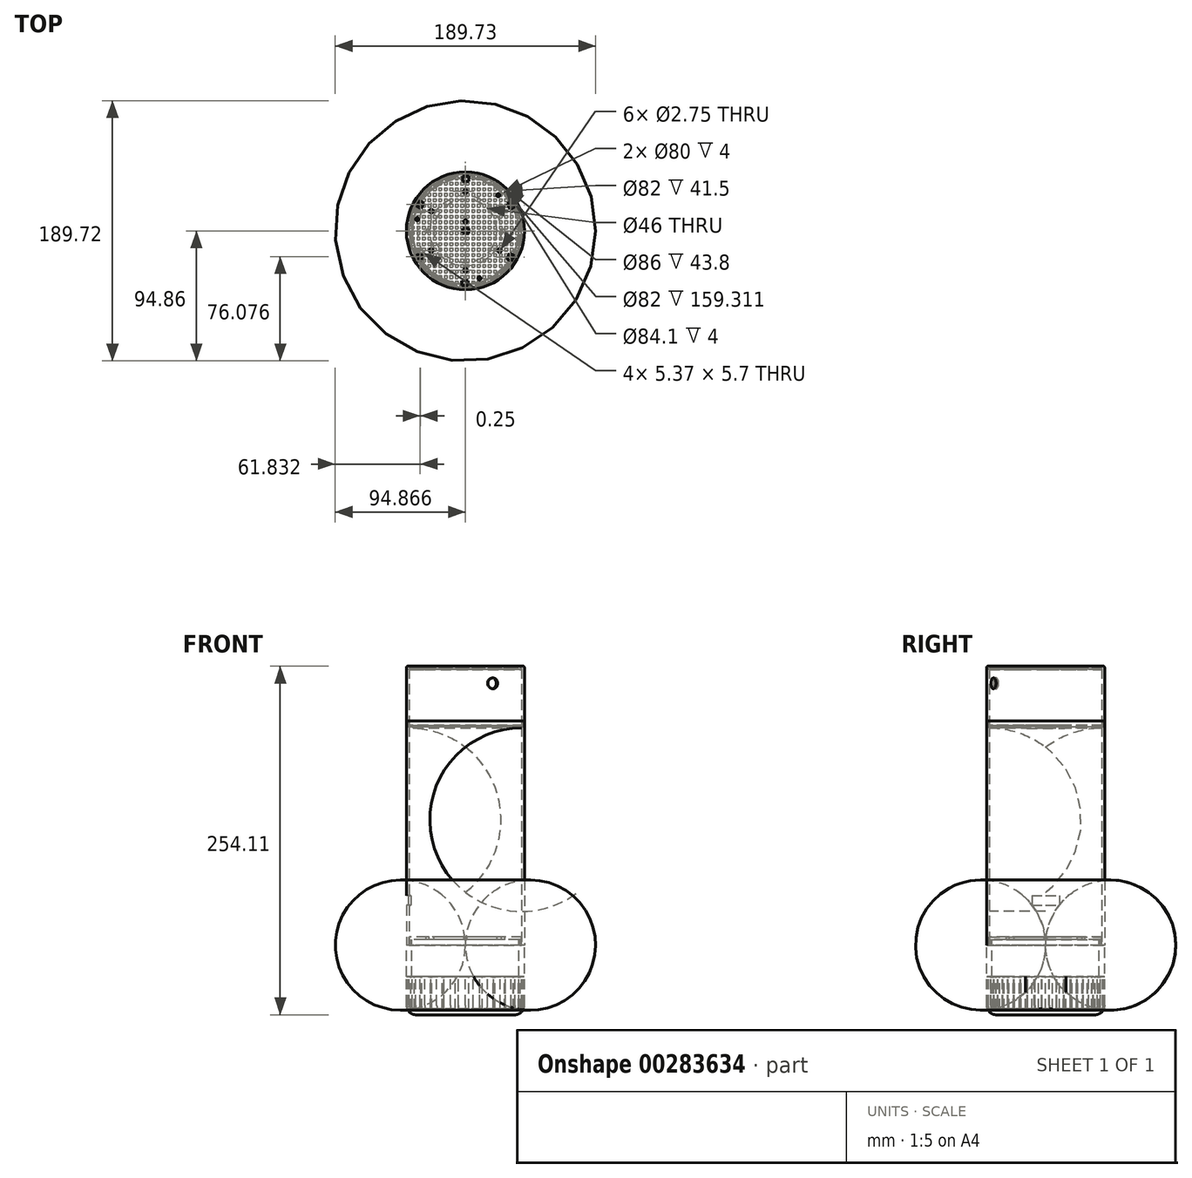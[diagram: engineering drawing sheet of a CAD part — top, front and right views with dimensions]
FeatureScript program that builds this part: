
annotation { "Feature Type Name" : "Feature", "Feature Type Description" : "" }
export const myFeature = defineFeature(function(context is Context, id is Id, definition is map)
    precondition{}
    {
        {
            var Q0;
            Q0=qCreatedBy(makeId("Front.planeOp"),FACE);
            var sketch = newSketch(context, id + "F0", { "sketchPlane" : qUnion([Q0])});
            skLineSegment(sketch, "E0", {"start": v(-50.53, -12.24) * mm, "end": v(-47.53, -12.24) * mm});
            skLineSegment(sketch, "E1", {"start": v(-50.53, 151.07) * mm, "end": v(-50.53, -2.93) * mm});
            skLineSegment(sketch, "E2", {"start": v(-7.53, -12.24) * mm, "end": v(-7.53, -63.04) * mm});
            skLineSegment(sketch, "E3", {"start": v(-50.53, -12.24) * mm, "end": v(-50.53, -56.04) * mm});
            skLineSegment(sketch, "E4", {"start": v(-7.53, -63.04) * mm, "end": v(-37.53, -63.04) * mm});
            skPoint(sketch, "E5.visualSharp", {"position": v(-50.53, -63.04) * mm});
            skArc(sketch, "E5.filletArc", {"start": v(-50.53, -56.04) * mm, "mid": v(-48.48, -61) * mm, "end": v(-43.53, -63.04) * mm});
            skLineSegment(sketch, "E6", {"start": v(-40.53, -63.04) * mm, "end": v(-37.53, -63.04) * mm});
            skLineSegment(sketch, "E7", {"start": v(-7.53, -63.04) * mm, "end": v(-7.53, -61.54) * mm});
            skLineSegment(sketch, "E8", {"start": v(-47.53, -12.24) * mm, "end": v(-47.53, -54.54) * mm});
            skLineSegment(sketch, "E9", {"start": v(-7.53, -61.54) * mm, "end": v(-40.53, -61.54) * mm});
            skPoint(sketch, "E10", {"position": v(-50.53, -34.14) * mm});
            skLineSegment(sketch, "E11", {"start": v(-50.53, -34.14) * mm, "end": v(-50.53, -47.14) * mm, "construction": true});
            skPoint(sketch, "E12", {"position": v(-50.53, -47.14) * mm});
            skLineSegment(sketch, "E13", {"start": v(-7.53, -63.04) * mm, "end": v(-7.53, 112.76) * mm, "construction": true});
            skLineSegment(sketch, "E14", {"start": v(-7.53, -8.24) * mm, "end": v(-7.53, -6.24) * mm});
            skLineSegment(sketch, "E15", {"start": v(-7.53, -59.5) * mm, "end": v(-7.53, -52.5) * mm});
            skLineSegment(sketch, "E16", {"start": v(-43.53, -63.04) * mm, "end": v(-40.53, -63.04) * mm});
            skLineSegment(sketch, "E17", {"start": v(-50.53, 151.07) * mm, "end": v(-49.58, 151.07) * mm});
            skLineSegment(sketch, "E18", {"start": v(-49.58, 151.07) * mm, "end": v(-49.58, 147.07) * mm});
            skLineSegment(sketch, "E19", {"start": v(-49.53, 148.07) * mm, "end": v(-49.53, 151.07) * mm});
            skLineSegment(sketch, "E20", {"start": v(-49.53, 151.07) * mm, "end": v(-50.53, 151.07) * mm});
            skLineSegment(sketch, "E21", {"start": v(-49.53, 148.07) * mm, "end": v(-48.53, 148.07) * mm});
            skLineSegment(sketch, "E22", {"start": v(-48.53, 148.07) * mm, "end": v(-48.53, 151.07) * mm});
            skLineSegment(sketch, "E23", {"start": v(-50.53, 191.07) * mm, "end": v(-7.53, 191.07) * mm});
            skLineSegment(sketch, "E24", {"start": v(-7.53, 191.07) * mm, "end": v(-7.53, 189.57) * mm});
            skPoint(sketch, "E25", {"position": v(-50.53, 181.57) * mm});
            skPoint(sketch, "E26", {"position": v(-47.73, 181.57) * mm});
            skLineSegment(sketch, "E27", {"start": v(-48.53, 151.07) * mm, "end": v(-48.53, 189.57) * mm});
            skLineSegment(sketch, "E28", {"start": v(-7.53, 191.07) * mm, "end": v(-7.53, 112.76) * mm, "construction": true});
            skPoint(sketch, "E29.end.orphan", {"position": v(-50.53, -2.93) * mm});
            skLineSegment(sketch, "E30", {"start": v(-50.53, -2.93) * mm, "end": v(-50.53, -12.24) * mm});
            skLineSegment(sketch, "E31", {"start": v(-48.53, -6.24) * mm, "end": v(-48.53, -12.24) * mm});
            skLineSegment(sketch, "E32", {"start": v(-47.53, -12.24) * mm, "end": v(-46.53, -12.24) * mm});
            skLineSegment(sketch, "E33", {"start": v(-48.53, -12.24) * mm, "end": v(-48.48, -12.24) * mm});
            skLineSegment(sketch, "E34", {"start": v(-48.48, -12.24) * mm, "end": v(-48.48, -6.24) * mm});
            skLineSegment(sketch, "E35", {"start": v(-48.48, -6.24) * mm, "end": v(-47.53, -6.24) * mm});
            skLineSegment(sketch, "E36", {"start": v(-47.53, -6.24) * mm, "end": v(-47.53, -12.24) * mm});
            skLineSegment(sketch, "E37", {"start": v(-7.53, -6.24) * mm, "end": v(-48.48, -6.24) * mm});
            skLineSegment(sketch, "E38", {"start": v(-7.53, -8.24) * mm, "end": v(-47.53, -8.24) * mm});
            skLineSegment(sketch, "E39", {"start": v(-47.53, -12.24) * mm, "end": v(-47.48, -12.24) * mm});
            skLineSegment(sketch, "E40", {"start": v(-47.48, -12.24) * mm, "end": v(-47.48, -8.24) * mm});
            skLineSegment(sketch, "E41", {"start": v(-47.48, -8.24) * mm, "end": v(-46.53, -8.24) * mm});
            skLineSegment(sketch, "E42", {"start": v(-46.53, -8.24) * mm, "end": v(-46.53, -12.24) * mm});
            skLineSegment(sketch, "E43", {"start": v(-46.53, -12.24) * mm, "end": v(-46.53, -58.92) * mm});
            skArc(sketch, "E44", {"start": v(-46.53, -58.92) * mm, "mid": v(-43.86, -60.98) * mm, "end": v(-40.53, -61.54) * mm});
            skArc(sketch, "E45", {"start": v(-46.53, -58.92) * mm, "mid": v(-18.57, -42.66) * mm, "end": v(-7.53, -12.24) * mm});
            skLineSegment(sketch, "E46", {"start": v(-49.58, 147.07) * mm, "end": v(-50.53, 147.07) * mm, "construction": true});
            skLineSegment(sketch, "E47", {"start": v(-49.53, 148.07) * mm, "end": v(-49.53, 147.07) * mm});
            skLineSegment(sketch, "E48", {"start": v(-49.53, 147.07) * mm, "end": v(-7.53, 147.07) * mm});
            skLineSegment(sketch, "E49", {"start": v(-48.53, 148.07) * mm, "end": v(-7.53, 148.07) * mm});
            skLineSegment(sketch, "E50", {"start": v(-7.53, 148.07) * mm, "end": v(-7.53, 147.07) * mm});
            skLineSegment(sketch, "E51", {"start": v(-49.58, 147.07) * mm, "end": v(-48.53, 147.07) * mm});
            skLineSegment(sketch, "E52", {"start": v(-48.53, 147.07) * mm, "end": v(-48.53, -6.24) * mm});
            skLineSegment(sketch, "E53", {"start": v(-48.53, -6.24) * mm, "end": v(-47.53, -6.24) * mm, "construction": true});
            skLineSegment(sketch, "E54", {"start": v(-48.53, 147.07) * mm, "end": v(-48.48, 147.07) * mm});
            skLineSegment(sketch, "E55", {"start": v(-48.48, 147.07) * mm, "end": v(-48.48, 146.07) * mm});
            skLineSegment(sketch, "E56", {"start": v(-7.53, 147.07) * mm, "end": v(-7.53, 132.07) * mm});
            skLineSegment(sketch, "E57", {"start": v(-48.48, 146.07) * mm, "end": v(-7.53, 146.07) * mm, "construction": true});
            skArc(sketch, "E58", {"start": v(-7.53, 132.07) * mm, "mid": v(-26.85, 142.47) * mm, "end": v(-48.48, 146.07) * mm});
            skLineSegment(sketch, "E59", {"start": v(-48.48, -6.24) * mm, "end": v(-48.53, 10.54) * mm, "construction": true});
            skLineSegment(sketch, "E60", {"start": v(-48.48, -6.24) * mm, "end": v(-48.53, 23.76) * mm, "construction": true});
            skPoint(sketch, "E61", {"position": v(-48.53, 23.76) * mm});
            skLineSegment(sketch, "E62", {"start": v(-50.53, 151.07) * mm, "end": v(-50.53, 191.07) * mm});
            skLineSegment(sketch, "E63", {"start": v(-48.53, 148.07) * mm, "end": v(-48.53, 147.07) * mm, "construction": true});
            skLineSegment(sketch, "E64", {"start": v(-48.53, 189.57) * mm, "end": v(-7.53, 189.57) * mm});
            skSolve(sketch);
        }
        {
            var Q0;
            {var subQ1=sQuery(id+"F0.wireOp",EDGE,"E0");Q0=makeQuery(id+"F0.imprint","IMPRINT",FACE,{"disambiguationData":[TD([[makeQuery(id+"F0.imprint","IMPRINT",EDGE,{"derivedFrom":subQ1}),-1.0]])]});}
            var Q1;
            Q1=makeQuery(id+"F0.imprint","IMPRINT",FACE,{"disambiguationData":[TD([[makeQuery(id+"F0.imprint","IMPRINT",EDGE,{"derivedFrom":sQuery(id+"F0.wireOp",EDGE,"E2")}),-1.0]])]});
            var Q2;
            Q2=makeQuery(id+"F0.imprint","IMPRINT",FACE,{"disambiguationData":[TD([[makeQuery(id+"F0.imprint","IMPRINT",EDGE,{"derivedFrom":sQuery(id+"F0.wireOp",EDGE,"E32")}),1.0]])]});
            var Q3;
            Q3=sQuery(id+"F0.wireOp",EDGE,"E2");
            revolve(context, id + "F1", {"entities" : qUnion([Q0, Q1, Q2]), "axis" : qUnion([Q3]), "revolveType" : RevolveType.FULL});
        }
        {
            var Q0;
            Q0=sQuery(id+"F0.wireOp",EDGE,"E3");
            var Q1;
            Q1=sQuery(id+"F0.wireOp",VERTEX,"E12");
            cPlane(context, id + "F2", {"entities" : qUnion([Q0, Q1]), "cplaneType" : CPlaneType.LINE_POINT, "offset" : 0 * mm, "width" : 150 * mm, "height" : 150 * mm});
        }
        {
            var Q0;
            Q0=qCreatedBy(id+"F2.planeOp",FACE);
            var sketch = newSketch(context, id + "F3", { "sketchPlane" : qUnion([Q0])});
            skLineSegment(sketch, "E65", {"start": v(-50.53, 0) * mm, "end": v(-46.03, 0) * mm, "construction": true});
            skLineSegment(sketch, "E66", {"start": v(-46.03, 0) * mm, "end": v(-46.03, 2.5) * mm, "construction": true});
            skLineSegment(sketch, "E67", {"start": v(-46.03, 2.5) * mm, "end": v(-50.53, 2.5) * mm});
            skLineSegment(sketch, "E68", {"start": v(-50.53, 2.5) * mm, "end": v(-50.53, -2.5) * mm});
            skLineSegment(sketch, "E69", {"start": v(-50.53, -2.5) * mm, "end": v(-46.03, -2.5) * mm});
            skLineSegment(sketch, "E70", {"start": v(-46.03, -2.5) * mm, "end": v(-46.03, 2.5) * mm});
            skLineSegment(sketch, "E71", {"start": v(-46.03, -6.5) * mm, "end": v(-46.03, -2.5) * mm});
            skLineSegment(sketch, "E72.MirrorCS", {"start": v(-46.03, 6.5) * mm, "end": v(-46.03, 2.5) * mm});
            skLineSegment(sketch, "E73", {"start": v(-46.03, -2.5) * mm, "end": v(-47.13, -2.5) * mm, "construction": true});
            skLineSegment(sketch, "E74", {"start": v(-47.13, -2.5) * mm, "end": v(-47.13, -5.3) * mm, "construction": true});
            skArc(sketch, "E75", {"start": v(-47.13, -5.3) * mm, "mid": v(-48.33, -3.3) * mm, "end": v(-50.53, -2.5) * mm});
            skArc(sketch, "E76", {"start": v(-47.13, -5.3) * mm, "mid": v(-46.82, -6.11) * mm, "end": v(-46.03, -6.5) * mm});
            skArc(sketch, "E77.MirrorCS", {"start": v(-47.13, 5.3) * mm, "mid": v(-48.33, 3.3) * mm, "end": v(-50.53, 2.5) * mm});
            skArc(sketch, "E78.MirrorCS", {"start": v(-47.13, 5.3) * mm, "mid": v(-46.82, 6.11) * mm, "end": v(-46.03, 6.5) * mm});
            skSolve(sketch);
        }
        {
            var Q0;
            Q0=qSketchRegion(id+"F3",true);
            extrude(context, id + "F4", {"entities" : qUnion([Q0]), "endBound" : BoundingType.SYMMETRIC, "depth" : 23.8 * mm});
        }
        {
            var Q0;
            Q0=makeQuery(id+"F4.opExtrude","SWEPT_BODY",BODY,{"disambiguationData":[OSD([sQuery(id+"F3.wireOp",EDGE,"E67"),sQuery(id+"F3.wireOp",EDGE,"E68"),sQuery(id+"F3.wireOp",EDGE,"E69"),sQuery(id+"F3.wireOp",EDGE,"E70")])]});
            var Q1;
            Q1=sQuery(id+"F0.wireOp",EDGE,"E2");
            circularPattern(context, id + "F5", {"operationType" : NewBodyOperationType.REMOVE, "entities" : qUnion([Q0]), "axis" : qUnion([Q1]), "angle" : 360 * degree, "instanceCount" : 25, "equalSpace" : true});
        }
        {
            var Q0;
            {var subQ4=sQuery(id+"F0.wireOp",EDGE,"E34");Q0=makeQuery(id+"F0.imprint","IMPRINT",FACE,{"disambiguationData":[TD([[makeQuery(id+"F0.imprint","IMPRINT",EDGE,{"derivedFrom":subQ4}),-1.0]])]});}
            var Q1;
            {var subQ1=sQuery(id+"F0.wireOp",EDGE,"E14");Q1=makeQuery(id+"F0.imprint","IMPRINT",FACE,{"disambiguationData":[TD([[makeQuery(id+"F0.imprint","IMPRINT",EDGE,{"derivedFrom":subQ1}),1.0]])]});}
            var Q2;
            Q2=sQuery(id+"F0.wireOp",EDGE,"E2");
            revolve(context, id + "F6", {"entities" : qUnion([Q0, Q1]), "axis" : qUnion([Q2]), "revolveType" : RevolveType.FULL});
        }
        {
            var Q0;
            {var subQ1=sQuery(id+"F0.wireOp",EDGE,"E1");Q0=makeQuery(id+"F0.imprint","IMPRINT",FACE,{"disambiguationData":[TD([[makeQuery(id+"F0.imprint","IMPRINT",EDGE,{"derivedFrom":subQ1}),1.0]])]});}
            var Q1;
            Q1=sQuery(id+"F0.wireOp",EDGE,"E13");
            revolve(context, id + "F7", {"entities" : qUnion([Q0]), "axis" : qUnion([Q1]), "revolveType" : RevolveType.FULL});
        }
        {
            var Q0;
            Q0=makeQuery(id+"F0.imprint","IMPRINT",FACE,{"disambiguationData":[TD([[makeQuery(id+"F0.imprint","IMPRINT",EDGE,{"derivedFrom":sQuery(id+"F0.wireOp",EDGE,"E21")}),-1.0]])]});
            var Q1;
            Q1=makeQuery(id+"F0.imprint","IMPRINT",FACE,{"disambiguationData":[TD([[makeQuery(id+"F0.imprint","IMPRINT",EDGE,{"derivedFrom":sQuery(id+"F0.wireOp",EDGE,"E48")}),-1.0]])]});
            var Q2;
            Q2=sQuery(id+"F0.wireOp",EDGE,"E56");
            revolve(context, id + "F8", {"entities" : qUnion([Q0, Q1]), "axis" : qUnion([Q2]), "revolveType" : RevolveType.FULL});
        }
        {
            var Q0;
            {var subQ5=sQuery(id+"F0.wireOp",EDGE,"E19");Q0=makeQuery(id+"F0.imprint","IMPRINT",FACE,{"disambiguationData":[TD([[makeQuery(id+"F0.imprint","IMPRINT",EDGE,{"derivedFrom":subQ5}),-1.0]])]});}
            var Q1;
            Q1=sQuery(id+"F0.wireOp",EDGE,"E13");
            revolve(context, id + "F9", {"entities" : qUnion([Q0]), "axis" : qUnion([Q1]), "revolveType" : RevolveType.FULL});
        }
        {
            var Q0;
            Q0=makeQuery(id+"F9.opRevolve","SWEPT_EDGE",EDGE,{"disambiguationData":[OSD([sQuery(id+"F0.wireOp",EDGE,"f6rtj6dZ-6JDe-umgd-hrW0-nHuk5Vi6zJmO"),sQuery(id+"F0.wireOp",EDGE,"E23")])]});
            fillet(context, id + "F10", {"entities" : qUnion([Q0]), "radius" : 1 * mm, "tangentPropagation" : true, "allowEdgeOverflow" : false});
        }
        {
            var Q0;
            Q0=makeQuery(id+"F9.opRevolve","SWEPT_FACE",FACE,{"disambiguationData":[OSD([sQuery(id+"F0.wireOp",EDGE,"E23")])]});
            var sketch = newSketch(context, id + "F11", { "sketchPlane" : qUnion([Q0])});
            skPoint(sketch, "E79", {"position": v(-7.53, 0) * mm});
            skCircle(sketch, "E80", {"center": v(-7.53, 0) * mm, "radius": 40 * mm, "construction": true});
            skLineSegment(sketch, "E81", {"start": v(-7.53, 0) * mm, "end": v(-7.53, -40) * mm, "construction": true});
            skLineSegment(sketch, "E82.1.0", {"start": v(-7.53, 0) * mm, "end": v(27.1, -20) * mm, "construction": true});
            skLineSegment(sketch, "E82.2.0", {"start": v(-7.53, 0) * mm, "end": v(27.1, 20) * mm, "construction": true});
            skLineSegment(sketch, "E82.3.0", {"start": v(-7.53, 0) * mm, "end": v(-7.53, 40) * mm, "construction": true});
            skLineSegment(sketch, "E82.4.0", {"start": v(-7.53, 0) * mm, "end": v(-42.18, 20) * mm, "construction": true});
            skLineSegment(sketch, "E82.5.0", {"start": v(-7.53, 0) * mm, "end": v(-42.18, -20) * mm, "construction": true});
            skLineSegment(sketch, "E83", {"start": v(-7.53, -40) * mm, "end": v(-7.53, -38) * mm, "construction": true});
            skPoint(sketch, "E84", {"position": v(-7.53, -38) * mm});
            skLineSegment(sketch, "E85", {"start": v(-7.53, -38) * mm, "end": v(-5.53, -38) * mm, "construction": true});
            skLineSegment(sketch, "E86", {"start": v(-7.53, -38) * mm, "end": v(-10.03, -38) * mm, "construction": true});
            skLineSegment(sketch, "E87", {"start": v(-7.53, -38) * mm, "end": v(-7.53, -39.8) * mm, "construction": true});
            skLineSegment(sketch, "E88", {"start": v(-7.53, -38) * mm, "end": v(-7.53, -36.2) * mm, "construction": true});
            skLineSegment(sketch, "E89", {"start": v(-7.53, -36.2) * mm, "end": v(-5.53, -36.2) * mm});
            skLineSegment(sketch, "E90", {"start": v(-5.53, -36.2) * mm, "end": v(-5.53, -39.8) * mm});
            skLineSegment(sketch, "E91", {"start": v(-5.53, -39.8) * mm, "end": v(-10.03, -39.8) * mm});
            skLineSegment(sketch, "E92", {"start": v(-10.03, -39.8) * mm, "end": v(-10.03, -36.2) * mm});
            skLineSegment(sketch, "E93", {"start": v(-10.03, -36.2) * mm, "end": v(-7.53, -36.2) * mm});
            skLineSegment(sketch, "E94", {"start": v(-7.53, -38) * mm, "end": v(-7.53, -28.7) * mm, "construction": true});
            skCircle(sketch, "E95", {"center": v(-7.53, -28.7) * mm, "radius": 1.37 * mm});
            skCircle(sketch, "E96.1.0", {"center": v(17.32, -14.35) * mm, "radius": 1.37 * mm});
            skLineSegment(sketch, "E96.1.1", {"start": v(23.82, -18.1) * mm, "end": v(24.82, -16.37) * mm});
            skLineSegment(sketch, "E96.1.2", {"start": v(22.57, -20.27) * mm, "end": v(23.82, -18.1) * mm});
            skLineSegment(sketch, "E96.1.3", {"start": v(25.68, -22.07) * mm, "end": v(22.57, -20.27) * mm});
            skLineSegment(sketch, "E96.1.4", {"start": v(24.82, -16.37) * mm, "end": v(27.93, -18.17) * mm});
            skLineSegment(sketch, "E96.1.5", {"start": v(27.93, -18.17) * mm, "end": v(25.68, -22.07) * mm});
            skCircle(sketch, "E96.2.0", {"center": v(17.32, 14.35) * mm, "radius": 1.37 * mm});
            skLineSegment(sketch, "E96.2.1", {"start": v(23.82, 18.1) * mm, "end": v(22.82, 19.83) * mm});
            skLineSegment(sketch, "E96.2.2", {"start": v(25.07, 15.93) * mm, "end": v(23.82, 18.1) * mm});
            skLineSegment(sketch, "E96.2.3", {"start": v(28.18, 17.73) * mm, "end": v(25.07, 15.93) * mm});
            skLineSegment(sketch, "E96.2.4", {"start": v(22.82, 19.83) * mm, "end": v(25.93, 21.63) * mm});
            skLineSegment(sketch, "E96.2.5", {"start": v(25.93, 21.63) * mm, "end": v(28.18, 17.73) * mm});
            skCircle(sketch, "E96.3.0", {"center": v(-7.53, 28.7) * mm, "radius": 1.37 * mm});
            skLineSegment(sketch, "E96.3.1", {"start": v(-7.53, 36.2) * mm, "end": v(-9.53, 36.2) * mm});
            skLineSegment(sketch, "E96.3.2", {"start": v(-5.03, 36.2) * mm, "end": v(-7.53, 36.2) * mm});
            skLineSegment(sketch, "E96.3.3", {"start": v(-5.03, 39.8) * mm, "end": v(-5.03, 36.2) * mm});
            skLineSegment(sketch, "E96.3.4", {"start": v(-9.53, 36.2) * mm, "end": v(-9.53, 39.8) * mm});
            skLineSegment(sketch, "E96.3.5", {"start": v(-9.53, 39.8) * mm, "end": v(-5.03, 39.8) * mm});
            skCircle(sketch, "E96.4.0", {"center": v(-32.39, 14.35) * mm, "radius": 1.37 * mm});
            skLineSegment(sketch, "E96.4.1", {"start": v(-38.88, 18.1) * mm, "end": v(-39.88, 16.37) * mm});
            skLineSegment(sketch, "E96.4.2", {"start": v(-37.63, 20.27) * mm, "end": v(-38.88, 18.1) * mm});
            skLineSegment(sketch, "E96.4.3", {"start": v(-40.75, 22.07) * mm, "end": v(-37.63, 20.27) * mm});
            skLineSegment(sketch, "E96.4.4", {"start": v(-39.88, 16.37) * mm, "end": v(-43, 18.17) * mm});
            skLineSegment(sketch, "E96.4.5", {"start": v(-43, 18.17) * mm, "end": v(-40.75, 22.07) * mm});
            skCircle(sketch, "E96.5.0", {"center": v(-32.39, -14.35) * mm, "radius": 1.37 * mm});
            skLineSegment(sketch, "E96.5.1", {"start": v(-38.88, -18.1) * mm, "end": v(-37.88, -19.83) * mm});
            skLineSegment(sketch, "E96.5.2", {"start": v(-40.13, -15.93) * mm, "end": v(-38.88, -18.1) * mm});
            skLineSegment(sketch, "E96.5.3", {"start": v(-43.25, -17.73) * mm, "end": v(-40.13, -15.93) * mm});
            skLineSegment(sketch, "E96.5.4", {"start": v(-37.88, -19.83) * mm, "end": v(-41, -21.63) * mm});
            skLineSegment(sketch, "E96.5.5", {"start": v(-41, -21.63) * mm, "end": v(-43.25, -17.73) * mm});
            skLineSegment(sketch, "E97", {"start": v(-7.53, 0) * mm, "end": v(-7.53, 1.8) * mm, "construction": true});
            skLineSegment(sketch, "E98", {"start": v(-7.53, 1.8) * mm, "end": v(-9.53, 1.8) * mm, "construction": true});
            skLineSegment(sketch, "E99.bottom", {"start": v(-9.53, 1.8) * mm, "end": v(-5.03, 1.8) * mm});
            skLineSegment(sketch, "E99.top", {"start": v(-9.53, -1.8) * mm, "end": v(-5.03, -1.8) * mm});
            skLineSegment(sketch, "E99.left", {"start": v(-9.53, 1.8) * mm, "end": v(-9.53, -1.8) * mm});
            skLineSegment(sketch, "E99.right", {"start": v(-5.03, 1.8) * mm, "end": v(-5.03, -1.8) * mm});
            skLineSegment(sketch, "E100", {"start": v(-7.53, 0) * mm, "end": v(-7.53, 6.8) * mm, "construction": true});
            skCircle(sketch, "E101", {"center": v(-7.53, 6.8) * mm, "radius": 1.25 * mm});
            skLineSegment(sketch, "E102", {"start": v(-7.53, -38) * mm, "end": v(2.64, -34.68) * mm, "construction": true});
            skLineSegment(sketch, "E103", {"start": v(2.64, -38.68) * mm, "end": v(2.64, -34.68) * mm, "construction": true});
            skCircle(sketch, "E104", {"center": v(2.64, -34.68) * mm, "radius": 1.15 * mm});
            skCircle(sketch, "E105.1.0", {"center": v(16.43, 25.99) * mm, "radius": 1.15 * mm});
            skCircle(sketch, "E105.2.0", {"center": v(-42.66, 8.53) * mm, "radius": 1.15 * mm});
            skLineSegment(sketch, "E106", {"start": v(2.64, -34.68) * mm, "end": v(25.68, -22.07) * mm, "construction": true});
            skLineSegment(sketch, "E107", {"start": v(2.64, -34.68) * mm, "end": v(9.66, -30.84) * mm, "construction": true});
            skLineSegment(sketch, "E108", {"start": v(9.66, -30.84) * mm, "end": v(13.35, -37.59) * mm, "construction": true});
            skPoint(sketch, "E109", {"position": v(13.35, -37.59) * mm});
            skCircle(sketch, "E110.0", {"center": v(-7.53, 0) * mm, "radius": 41 * mm, "construction": true});
            skSolve(sketch);
        }
        {
            var Q0;
            Q0 = qSketchRegion(id + "F11", true);
            extrude(context, id + "F12", {"entities" : qUnion([Q0]), "operationType" : NewBodyOperationType.REMOVE, "endBound" : BoundingType.UP_TO_NEXT, "oppositeDirection" : true, "depth" : 25 * mm});
        }
        {
            var Q0;
            Q0=sQuery(id+"F11.wireOp",VERTEX,"E109");
            var Q1;
            Q1=sQuery(id+"F11.wireOp",EDGE,"E108");
            cPlane(context, id + "F13", {"entities" : qUnion([Q0, Q1]), "cplaneType" : CPlaneType.LINE_POINT, "offset" : 25 * mm, "width" : 150 * mm, "height" : 150 * mm});
        }
        {
            var Q0;
            Q0=qCreatedBy(id+"F13.planeOp",FACE);
            var sketch = newSketch(context, id + "F14", { "sketchPlane" : qUnion([Q0])});
            skLineSegment(sketch, "E111", {"start": v(-7.34, 191.07) * mm, "end": v(-7.34, 178.57) * mm, "construction": true});
            skCircle(sketch, "E112", {"center": v(-7.34, 178.57) * mm, "radius": 4 * mm});
            skLineSegment(sketch, "E113", {"start": v(-48.6, 191.07) * mm, "end": v(35.4, 191.07) * mm});
            skSolve(sketch);
        }
        {
            var Q0;
            Q0 = qSketchRegion(id + "F14", true);
            extrude(context, id + "F15", {"entities" : qUnion([Q0]), "operationType" : NewBodyOperationType.REMOVE, "endBound" : BoundingType.SYMMETRIC, "oppositeDirection" : true, "depth" : 7 * mm});
        }
        {
            var Q0;
            Q0=makeQuery(id+"F8.opRevolve","SWEPT_FACE",FACE,{"disambiguationData":[OSD([sQuery(id+"F0.wireOp",EDGE,"E21"),sQuery(id+"F0.wireOp",EDGE,"E49")])]});
            var sketch = newSketch(context, id + "F16", { "sketchPlane" : qUnion([Q0])});
            skCircle(sketch, "E114.0", {"center": v(-7.53, 0) * mm, "radius": 42 * mm, "construction": true});
            skLineSegment(sketch, "E115", {"start": v(-49.53, 0) * mm, "end": v(-48.48, 0) * mm, "construction": true});
            skCircle(sketch, "E116.0", {"center": v(-7.53, 0) * mm, "radius": 40.95 * mm});
            skLineSegment(sketch, "E117", {"start": v(-48.48, 0) * mm, "end": v(-45.74, 14.75) * mm, "construction": true});
            skLineSegment(sketch, "E118.MirrorCS", {"start": v(-48.48, 0) * mm, "end": v(-45.74, -14.75) * mm, "construction": true});
            skCircle(sketch, "E119.0", {"center": v(-7.53, 0) * mm, "radius": 34.95 * mm});
            skLineSegment(sketch, "E120", {"start": v(-45.74, 14.75) * mm, "end": v(-39.72, 13.63) * mm});
            skLineSegment(sketch, "E121.MirrorCS", {"start": v(-45.74, -14.75) * mm, "end": v(-39.72, -13.63) * mm});
            skSolve(sketch);
        }
        {
            var Q0;
            {var subQ0=sQuery(id+"F16.wireOp",EDGE,"E120");Q0=makeQuery(id+"F16.imprint","IMPRINT",FACE,{"disambiguationData":[TD([[makeQuery(id+"F16.imprint","IMPRINT",EDGE,{"derivedFrom":subQ0}),-1.0]])]});}
            extrude(context, id + "F17", {"entities" : qUnion([Q0]), "operationType" : NewBodyOperationType.REMOVE, "endBound" : BoundingType.UP_TO_NEXT, "oppositeDirection" : true, "depth" : 25 * mm});
        }
        {
            var Q0;
            Q0=sQuery(id+"F0.wireOp",EDGE,"E52");
            cPlane(context, id + "F18", {"entities" : qUnion([Q0]), "cplaneType" : CPlaneType.LINE_ANGLE, "offset" : 25 * mm, "angle" : 0 * degree, "width" : 150 * mm, "height" : 150 * mm});
        }
        {
            var Q0;
            Q0=qCreatedBy(id+"F18.planeOp",FACE);
            var sketch = newSketch(context, id + "F19", { "sketchPlane" : qUnion([Q0])});
            skPoint(sketch, "E122.0", {"position": v(0, 23.76) * mm});
            skLineSegment(sketch, "E123", {"start": v(0, 23.76) * mm, "end": v(10, 23.76) * mm});
            skLineSegment(sketch, "E124", {"start": v(10, 23.76) * mm, "end": v(-10, 23.76) * mm});
            skPoint(sketch, "E124.endSnap0", {"position": v(5, 23.76) * mm});
            skLineSegment(sketch, "E125", {"start": v(-10, 23.76) * mm, "end": v(-10, 16.76) * mm});
            skLineSegment(sketch, "E126", {"start": v(-10, 16.76) * mm, "end": v(10, 16.76) * mm});
            skLineSegment(sketch, "E127", {"start": v(10, 16.76) * mm, "end": v(10, 23.76) * mm});
            skSolve(sketch);
        }
        {
            var Q0;
            Q0 = qSketchRegion(id + "F19", true);
            extrude(context, id + "F20", {"entities" : qUnion([Q0]), "operationType" : NewBodyOperationType.REMOVE, "endBound" : BoundingType.SYMMETRIC, "oppositeDirection" : true, "depth" : 5 * mm});
        }
        {
            var Q0;
            Q0=makeQuery(id+"F9.opRevolve","SWEPT_FACE",FACE,{"disambiguationData":[OSD([sQuery(id+"F0.wireOp",EDGE,"E64")])]});
            var sketch = newSketch(context, id + "F21", { "sketchPlane" : qUnion([Q0])});
            skCircle(sketch, "E128.0", {"center": v(-7.53, 0) * mm, "radius": 41 * mm, "construction": true});
            skCircle(sketch, "E129.0", {"center": v(-7.53, 0) * mm, "radius": 40.98 * mm});
            skLineSegment(sketch, "E130.0", {"start": v(-5.53, 39.8) * mm, "end": v(-5.53, 36.2) * mm});
            skLineSegment(sketch, "E131.0", {"start": v(-10.03, 39.8) * mm, "end": v(-5.53, 39.8) * mm});
            skLineSegment(sketch, "E132.0", {"start": v(-10.03, 36.2) * mm, "end": v(-10.03, 39.8) * mm});
            skLineSegment(sketch, "E133.0", {"start": v(-5.53, 36.2) * mm, "end": v(-10.03, 36.2) * mm});
            skCircle(sketch, "E134.0", {"center": v(2.64, 34.68) * mm, "radius": 1.15 * mm});
            skCircle(sketch, "E135.0", {"center": v(17.32, 14.35) * mm, "radius": 1.37 * mm});
            skCircle(sketch, "E136.0", {"center": v(17.32, -14.35) * mm, "radius": 1.37 * mm});
            skCircle(sketch, "E137.0", {"center": v(-7.53, -28.7) * mm, "radius": 1.37 * mm});
            skCircle(sketch, "E138.0", {"center": v(-32.39, -14.35) * mm, "radius": 1.37 * mm});
            skCircle(sketch, "E139.0", {"center": v(-42.66, -8.53) * mm, "radius": 1.15 * mm});
            skCircle(sketch, "E140.0", {"center": v(-32.39, 14.35) * mm, "radius": 1.37 * mm});
            skCircle(sketch, "E141.0", {"center": v(-7.53, 28.7) * mm, "radius": 1.37 * mm});
            skCircle(sketch, "E142.0", {"center": v(-7.53, -6.8) * mm, "radius": 1.25 * mm});
            skCircle(sketch, "E143.0", {"center": v(16.43, -25.99) * mm, "radius": 1.15 * mm});
            skLineSegment(sketch, "E144.0", {"start": v(22.57, 20.27) * mm, "end": v(25.68, 22.07) * mm});
            skLineSegment(sketch, "E145.0", {"start": v(25.68, 22.07) * mm, "end": v(27.93, 18.17) * mm});
            skLineSegment(sketch, "E146.0", {"start": v(27.93, 18.17) * mm, "end": v(24.82, 16.37) * mm});
            skLineSegment(sketch, "E147.0", {"start": v(24.82, 16.37) * mm, "end": v(22.57, 20.27) * mm});
            skLineSegment(sketch, "E148.0", {"start": v(25.07, -15.93) * mm, "end": v(28.18, -17.73) * mm});
            skLineSegment(sketch, "E149.0", {"start": v(28.18, -17.73) * mm, "end": v(25.93, -21.63) * mm});
            skLineSegment(sketch, "E150.0", {"start": v(25.93, -21.63) * mm, "end": v(22.82, -19.83) * mm});
            skLineSegment(sketch, "E151.0", {"start": v(22.82, -19.83) * mm, "end": v(25.07, -15.93) * mm});
            skLineSegment(sketch, "E152.0", {"start": v(-5.03, -36.2) * mm, "end": v(-5.03, -39.8) * mm});
            skLineSegment(sketch, "E153.0", {"start": v(-9.53, -36.2) * mm, "end": v(-5.03, -36.2) * mm});
            skLineSegment(sketch, "E154.0", {"start": v(-9.53, -39.8) * mm, "end": v(-9.53, -36.2) * mm});
            skLineSegment(sketch, "E155.0", {"start": v(-5.03, -39.8) * mm, "end": v(-9.53, -39.8) * mm});
            skLineSegment(sketch, "E156.0", {"start": v(-39.88, -16.37) * mm, "end": v(-37.63, -20.27) * mm});
            skLineSegment(sketch, "E157.0", {"start": v(-37.63, -20.27) * mm, "end": v(-40.75, -22.07) * mm});
            skLineSegment(sketch, "E158.0", {"start": v(-40.75, -22.07) * mm, "end": v(-43, -18.17) * mm});
            skLineSegment(sketch, "E159.0", {"start": v(-43, -18.17) * mm, "end": v(-39.88, -16.37) * mm});
            skLineSegment(sketch, "E160.0", {"start": v(-41, 21.63) * mm, "end": v(-37.88, 19.83) * mm});
            skLineSegment(sketch, "E161.0", {"start": v(-37.88, 19.83) * mm, "end": v(-40.13, 15.93) * mm});
            skLineSegment(sketch, "E162.0", {"start": v(-40.13, 15.93) * mm, "end": v(-43.25, 17.73) * mm});
            skLineSegment(sketch, "E163.0", {"start": v(-43.25, 17.73) * mm, "end": v(-41, 21.63) * mm});
            skLineSegment(sketch, "E164.0", {"start": v(-5.03, 1.8) * mm, "end": v(-5.03, -1.8) * mm});
            skLineSegment(sketch, "E165.0", {"start": v(-5.03, -1.8) * mm, "end": v(-9.53, -1.8) * mm});
            skLineSegment(sketch, "E166.0", {"start": v(-5.03, 1.8) * mm, "end": v(-9.53, 1.8) * mm});
            skLineSegment(sketch, "E167.0", {"start": v(-9.53, 1.8) * mm, "end": v(-9.53, -1.8) * mm});
            skSolve(sketch);
        }
        {
            var Q0;
            Q0 = qSketchRegion(id + "F21", true);
            var Q1;
            Q1=makeQuery(id+"F21.imprint","IMPRINT",FACE,{"disambiguationData":[TD([[makeQuery(id+"F21.imprint","IMPRINT",EDGE,{"derivedFrom":sQuery(id+"F21.wireOp",EDGE,"6cf842b4-8cee-4f3a-be1a-66a8b3b2ef9b.0")}),1.0]])]});
            extrude(context, id + "F22", {"entities" : qUnion([Q0, Q1]), "depth" : 1 * mm});
        }
        {
            var Q0;
            Q0=makeQuery(id+"F22.opExtrude","CAP_FACE",FACE,{"disambiguationData":[OSD([sQuery(id+"F21.wireOp",EDGE,"E129.0"),sQuery(id+"F21.wireOp",EDGE,"E130.0"),sQuery(id+"F21.wireOp",EDGE,"E131.0"),sQuery(id+"F21.wireOp",EDGE,"E132.0"),sQuery(id+"F21.wireOp",EDGE,"E133.0"),sQuery(id+"F21.wireOp",EDGE,"E134.0"),sQuery(id+"F21.wireOp",EDGE,"E135.0"),sQuery(id+"F21.wireOp",EDGE,"E136.0"),sQuery(id+"F21.wireOp",EDGE,"E137.0"),sQuery(id+"F21.wireOp",EDGE,"E138.0"),sQuery(id+"F21.wireOp",EDGE,"E139.0"),sQuery(id+"F21.wireOp",EDGE,"E140.0"),sQuery(id+"F21.wireOp",EDGE,"E141.0"),sQuery(id+"F21.wireOp",EDGE,"E142.0"),sQuery(id+"F21.wireOp",EDGE,"E143.0"),sQuery(id+"F21.wireOp",EDGE,"E144.0"),sQuery(id+"F21.wireOp",EDGE,"E145.0"),sQuery(id+"F21.wireOp",EDGE,"E146.0"),sQuery(id+"F21.wireOp",EDGE,"E147.0"),sQuery(id+"F21.wireOp",EDGE,"E148.0"),sQuery(id+"F21.wireOp",EDGE,"E149.0"),sQuery(id+"F21.wireOp",EDGE,"E150.0"),sQuery(id+"F21.wireOp",EDGE,"E151.0"),sQuery(id+"F21.wireOp",EDGE,"E152.0"),sQuery(id+"F21.wireOp",EDGE,"E153.0"),sQuery(id+"F21.wireOp",EDGE,"E154.0"),sQuery(id+"F21.wireOp",EDGE,"E155.0"),sQuery(id+"F21.wireOp",EDGE,"E156.0"),sQuery(id+"F21.wireOp",EDGE,"E157.0"),sQuery(id+"F21.wireOp",EDGE,"E158.0"),sQuery(id+"F21.wireOp",EDGE,"E159.0"),sQuery(id+"F21.wireOp",EDGE,"E160.0"),sQuery(id+"F21.wireOp",EDGE,"E161.0"),sQuery(id+"F21.wireOp",EDGE,"E162.0"),sQuery(id+"F21.wireOp",EDGE,"E163.0"),sQuery(id+"F21.wireOp",EDGE,"E164.0"),sQuery(id+"F21.wireOp",EDGE,"E165.0"),sQuery(id+"F21.wireOp",EDGE,"E166.0"),sQuery(id+"F21.wireOp",EDGE,"E167.0")])],"isStart":true});
            var sketch = newSketch(context, id + "F23", { "sketchPlane" : qUnion([Q0])});
            skLineSegment(sketch, "E168.0", {"start": v(22.57, -20.27) * mm, "end": v(25.68, -22.07) * mm});
            skLineSegment(sketch, "E169.0", {"start": v(25.68, -22.07) * mm, "end": v(27.93, -18.17) * mm});
            skLineSegment(sketch, "E170.0", {"start": v(27.93, -18.17) * mm, "end": v(24.82, -16.37) * mm});
            skLineSegment(sketch, "E171.0", {"start": v(24.82, -16.37) * mm, "end": v(22.57, -20.27) * mm});
            skCircle(sketch, "E172.0", {"center": v(-7.53, -28.7) * mm, "radius": 1.37 * mm});
            skLineSegment(sketch, "E173.0", {"start": v(-5.53, -36.2) * mm, "end": v(-10.03, -36.2) * mm});
            skLineSegment(sketch, "E174.0", {"start": v(-5.53, -39.8) * mm, "end": v(-5.53, -36.2) * mm});
            skLineSegment(sketch, "E175.0", {"start": v(-10.03, -39.8) * mm, "end": v(-5.53, -39.8) * mm});
            skPoint(sketch, "E176.0", {"position": v(-10.03, -38) * mm});
            skLineSegment(sketch, "E177.0", {"start": v(-10.03, -36.2) * mm, "end": v(-10.03, -39.8) * mm});
            skLineSegment(sketch, "E178.0", {"start": v(-41, -21.63) * mm, "end": v(-37.88, -19.83) * mm});
            skLineSegment(sketch, "E179.0", {"start": v(-43.25, -17.73) * mm, "end": v(-41, -21.63) * mm});
            skLineSegment(sketch, "E180.0", {"start": v(-40.13, -15.93) * mm, "end": v(-43.25, -17.73) * mm});
            skLineSegment(sketch, "E181.0", {"start": v(-37.88, -19.83) * mm, "end": v(-40.13, -15.93) * mm});
            skLineSegment(sketch, "E182.0", {"start": v(-43, 18.17) * mm, "end": v(-39.88, 16.37) * mm});
            skLineSegment(sketch, "E183.0", {"start": v(-39.88, 16.37) * mm, "end": v(-37.63, 20.27) * mm});
            skLineSegment(sketch, "E184.0", {"start": v(-37.63, 20.27) * mm, "end": v(-40.75, 22.07) * mm});
            skLineSegment(sketch, "E185.0", {"start": v(-40.75, 22.07) * mm, "end": v(-43, 18.17) * mm});
            skLineSegment(sketch, "E186.0", {"start": v(-9.53, 36.2) * mm, "end": v(-5.03, 36.2) * mm});
            skLineSegment(sketch, "E187.0", {"start": v(-9.53, 39.8) * mm, "end": v(-9.53, 36.2) * mm});
            skLineSegment(sketch, "E188.0", {"start": v(-5.03, 39.8) * mm, "end": v(-9.53, 39.8) * mm});
            skLineSegment(sketch, "E189.0", {"start": v(-5.03, 36.2) * mm, "end": v(-5.03, 39.8) * mm});
            skLineSegment(sketch, "E190.0", {"start": v(25.07, 15.93) * mm, "end": v(28.18, 17.73) * mm});
            skLineSegment(sketch, "E191.0", {"start": v(22.82, 19.83) * mm, "end": v(25.07, 15.93) * mm});
            skLineSegment(sketch, "E192.0", {"start": v(25.93, 21.63) * mm, "end": v(22.82, 19.83) * mm});
            skLineSegment(sketch, "E193.0", {"start": v(28.18, 17.73) * mm, "end": v(25.93, 21.63) * mm});
            skLineSegment(sketch, "E194.0", {"start": v(-5.03, -1.8) * mm, "end": v(-9.53, -1.8) * mm});
            skLineSegment(sketch, "E195.0", {"start": v(-5.03, -1.8) * mm, "end": v(-5.03, 1.8) * mm});
            skLineSegment(sketch, "E196.0", {"start": v(-5.03, 1.8) * mm, "end": v(-9.53, 1.8) * mm});
            skLineSegment(sketch, "E197.0", {"start": v(-9.53, -1.8) * mm, "end": v(-9.53, 1.8) * mm});
            skCircle(sketch, "E198.0", {"center": v(2.64, -34.68) * mm, "radius": 1.15 * mm});
            skCircle(sketch, "E199.0", {"center": v(-32.39, -14.35) * mm, "radius": 1.37 * mm});
            skCircle(sketch, "E200.0", {"center": v(-42.66, 8.53) * mm, "radius": 1.15 * mm});
            skCircle(sketch, "E201.0", {"center": v(-7.53, 6.8) * mm, "radius": 1.25 * mm});
            skCircle(sketch, "E202.0", {"center": v(-32.39, 14.35) * mm, "radius": 1.37 * mm});
            skCircle(sketch, "E203.0", {"center": v(-7.53, 28.7) * mm, "radius": 1.37 * mm});
            skCircle(sketch, "E204.0", {"center": v(16.43, 25.99) * mm, "radius": 1.15 * mm});
            skCircle(sketch, "E205.0", {"center": v(17.32, 14.35) * mm, "radius": 1.37 * mm});
            skCircle(sketch, "E206.0", {"center": v(17.32, -14.35) * mm, "radius": 1.37 * mm});
            skLineSegment(sketch, "E207.bottom", {"start": v(-50.95, 43.44) * mm, "end": v(-48.95, 43.44) * mm});
            skLineSegment(sketch, "E207.top", {"start": v(-50.95, 41.44) * mm, "end": v(-48.95, 41.44) * mm});
            skLineSegment(sketch, "E207.left", {"start": v(-50.95, 43.44) * mm, "end": v(-50.95, 41.44) * mm});
            skLineSegment(sketch, "E207.right", {"start": v(-48.95, 43.44) * mm, "end": v(-48.95, 41.44) * mm});
            skLineSegment(sketch, "E208.0.1.0", {"start": v(-50.95, 39.44) * mm, "end": v(-48.95, 39.44) * mm});
            skLineSegment(sketch, "E208.0.1.1", {"start": v(-50.95, 39.44) * mm, "end": v(-50.95, 37.44) * mm});
            skLineSegment(sketch, "E208.0.1.2", {"start": v(-50.95, 37.44) * mm, "end": v(-48.95, 37.44) * mm});
            skLineSegment(sketch, "E208.0.1.3", {"start": v(-48.95, 39.44) * mm, "end": v(-48.95, 37.44) * mm});
            skLineSegment(sketch, "E208.0.2.0", {"start": v(-50.95, 35.44) * mm, "end": v(-48.95, 35.44) * mm});
            skLineSegment(sketch, "E208.0.2.1", {"start": v(-50.95, 35.44) * mm, "end": v(-50.95, 33.44) * mm});
            skLineSegment(sketch, "E208.0.2.2", {"start": v(-50.95, 33.44) * mm, "end": v(-48.95, 33.44) * mm});
            skLineSegment(sketch, "E208.0.2.3", {"start": v(-48.95, 35.44) * mm, "end": v(-48.95, 33.44) * mm});
            skLineSegment(sketch, "E208.0.3.0", {"start": v(-50.95, 31.44) * mm, "end": v(-48.95, 31.44) * mm});
            skLineSegment(sketch, "E208.0.3.1", {"start": v(-50.95, 31.44) * mm, "end": v(-50.95, 29.44) * mm});
            skLineSegment(sketch, "E208.0.3.2", {"start": v(-50.95, 29.44) * mm, "end": v(-48.95, 29.44) * mm});
            skLineSegment(sketch, "E208.0.3.3", {"start": v(-48.95, 31.44) * mm, "end": v(-48.95, 29.44) * mm});
            skLineSegment(sketch, "E208.0.4.0", {"start": v(-50.95, 27.44) * mm, "end": v(-48.95, 27.44) * mm});
            skLineSegment(sketch, "E208.0.4.1", {"start": v(-50.95, 27.44) * mm, "end": v(-50.95, 25.44) * mm});
            skLineSegment(sketch, "E208.0.4.2", {"start": v(-50.95, 25.44) * mm, "end": v(-48.95, 25.44) * mm});
            skLineSegment(sketch, "E208.0.4.3", {"start": v(-48.95, 27.44) * mm, "end": v(-48.95, 25.44) * mm});
            skLineSegment(sketch, "E208.0.5.0", {"start": v(-50.95, 23.44) * mm, "end": v(-48.95, 23.44) * mm});
            skLineSegment(sketch, "E208.0.5.1", {"start": v(-50.95, 23.44) * mm, "end": v(-50.95, 21.44) * mm});
            skLineSegment(sketch, "E208.0.5.2", {"start": v(-50.95, 21.44) * mm, "end": v(-48.95, 21.44) * mm});
            skLineSegment(sketch, "E208.0.5.3", {"start": v(-48.95, 23.44) * mm, "end": v(-48.95, 21.44) * mm});
            skLineSegment(sketch, "E208.0.6.0", {"start": v(-50.95, 19.44) * mm, "end": v(-48.95, 19.44) * mm});
            skLineSegment(sketch, "E208.0.6.1", {"start": v(-50.95, 19.44) * mm, "end": v(-50.95, 17.44) * mm});
            skLineSegment(sketch, "E208.0.6.2", {"start": v(-50.95, 17.44) * mm, "end": v(-48.95, 17.44) * mm});
            skLineSegment(sketch, "E208.0.6.3", {"start": v(-48.95, 19.44) * mm, "end": v(-48.95, 17.44) * mm});
            skLineSegment(sketch, "E208.0.7.0", {"start": v(-50.95, 15.44) * mm, "end": v(-48.95, 15.44) * mm});
            skLineSegment(sketch, "E208.0.7.1", {"start": v(-50.95, 15.44) * mm, "end": v(-50.95, 13.44) * mm});
            skLineSegment(sketch, "E208.0.7.2", {"start": v(-50.95, 13.44) * mm, "end": v(-48.95, 13.44) * mm});
            skLineSegment(sketch, "E208.0.7.3", {"start": v(-48.95, 15.44) * mm, "end": v(-48.95, 13.44) * mm});
            skLineSegment(sketch, "E208.0.8.0", {"start": v(-50.95, 11.44) * mm, "end": v(-48.95, 11.44) * mm});
            skLineSegment(sketch, "E208.0.8.1", {"start": v(-50.95, 11.44) * mm, "end": v(-50.95, 9.44) * mm});
            skLineSegment(sketch, "E208.0.8.2", {"start": v(-50.95, 9.44) * mm, "end": v(-48.95, 9.44) * mm});
            skLineSegment(sketch, "E208.0.8.3", {"start": v(-48.95, 11.44) * mm, "end": v(-48.95, 9.44) * mm});
            skLineSegment(sketch, "E208.0.9.0", {"start": v(-50.95, 7.44) * mm, "end": v(-48.95, 7.44) * mm});
            skLineSegment(sketch, "E208.0.9.1", {"start": v(-50.95, 7.44) * mm, "end": v(-50.95, 5.44) * mm});
            skLineSegment(sketch, "E208.0.9.2", {"start": v(-50.95, 5.44) * mm, "end": v(-48.95, 5.44) * mm});
            skLineSegment(sketch, "E208.0.9.3", {"start": v(-48.95, 7.44) * mm, "end": v(-48.95, 5.44) * mm});
            skLineSegment(sketch, "E208.0.10.0", {"start": v(-50.95, 3.44) * mm, "end": v(-48.95, 3.44) * mm});
            skLineSegment(sketch, "E208.0.10.1", {"start": v(-50.95, 3.44) * mm, "end": v(-50.95, 1.44) * mm});
            skLineSegment(sketch, "E208.0.10.2", {"start": v(-50.95, 1.44) * mm, "end": v(-48.95, 1.44) * mm});
            skLineSegment(sketch, "E208.0.10.3", {"start": v(-48.95, 3.44) * mm, "end": v(-48.95, 1.44) * mm});
            skLineSegment(sketch, "E208.0.11.0", {"start": v(-50.95, -0.56) * mm, "end": v(-48.95, -0.56) * mm});
            skLineSegment(sketch, "E208.0.11.1", {"start": v(-50.95, -0.56) * mm, "end": v(-50.95, -2.56) * mm});
            skLineSegment(sketch, "E208.0.11.2", {"start": v(-50.95, -2.56) * mm, "end": v(-48.95, -2.56) * mm});
            skLineSegment(sketch, "E208.0.11.3", {"start": v(-48.95, -0.56) * mm, "end": v(-48.95, -2.56) * mm});
            skLineSegment(sketch, "E208.0.12.0", {"start": v(-50.95, -4.56) * mm, "end": v(-48.95, -4.56) * mm});
            skLineSegment(sketch, "E208.0.12.1", {"start": v(-50.95, -4.56) * mm, "end": v(-50.95, -6.56) * mm});
            skLineSegment(sketch, "E208.0.12.2", {"start": v(-50.95, -6.56) * mm, "end": v(-48.95, -6.56) * mm});
            skLineSegment(sketch, "E208.0.12.3", {"start": v(-48.95, -4.56) * mm, "end": v(-48.95, -6.56) * mm});
            skLineSegment(sketch, "E208.0.13.0", {"start": v(-50.95, -8.56) * mm, "end": v(-48.95, -8.56) * mm});
            skLineSegment(sketch, "E208.0.13.1", {"start": v(-50.95, -8.56) * mm, "end": v(-50.95, -10.56) * mm});
            skLineSegment(sketch, "E208.0.13.2", {"start": v(-50.95, -10.56) * mm, "end": v(-48.95, -10.56) * mm});
            skLineSegment(sketch, "E208.0.13.3", {"start": v(-48.95, -8.56) * mm, "end": v(-48.95, -10.56) * mm});
            skLineSegment(sketch, "E208.0.14.0", {"start": v(-50.95, -12.56) * mm, "end": v(-48.95, -12.56) * mm});
            skLineSegment(sketch, "E208.0.14.1", {"start": v(-50.95, -12.56) * mm, "end": v(-50.95, -14.56) * mm});
            skLineSegment(sketch, "E208.0.14.2", {"start": v(-50.95, -14.56) * mm, "end": v(-48.95, -14.56) * mm});
            skLineSegment(sketch, "E208.0.14.3", {"start": v(-48.95, -12.56) * mm, "end": v(-48.95, -14.56) * mm});
            skLineSegment(sketch, "E208.0.15.0", {"start": v(-50.95, -16.56) * mm, "end": v(-48.95, -16.56) * mm});
            skLineSegment(sketch, "E208.0.15.1", {"start": v(-50.95, -16.56) * mm, "end": v(-50.95, -18.56) * mm});
            skLineSegment(sketch, "E208.0.15.2", {"start": v(-50.95, -18.56) * mm, "end": v(-48.95, -18.56) * mm});
            skLineSegment(sketch, "E208.0.15.3", {"start": v(-48.95, -16.56) * mm, "end": v(-48.95, -18.56) * mm});
            skLineSegment(sketch, "E208.0.16.0", {"start": v(-50.95, -20.56) * mm, "end": v(-48.95, -20.56) * mm});
            skLineSegment(sketch, "E208.0.16.1", {"start": v(-50.95, -20.56) * mm, "end": v(-50.95, -22.56) * mm});
            skLineSegment(sketch, "E208.0.16.2", {"start": v(-50.95, -22.56) * mm, "end": v(-48.95, -22.56) * mm});
            skLineSegment(sketch, "E208.0.16.3", {"start": v(-48.95, -20.56) * mm, "end": v(-48.95, -22.56) * mm});
            skLineSegment(sketch, "E208.0.17.0", {"start": v(-50.95, -24.56) * mm, "end": v(-48.95, -24.56) * mm});
            skLineSegment(sketch, "E208.0.17.1", {"start": v(-50.95, -24.56) * mm, "end": v(-50.95, -26.56) * mm});
            skLineSegment(sketch, "E208.0.17.2", {"start": v(-50.95, -26.56) * mm, "end": v(-48.95, -26.56) * mm});
            skLineSegment(sketch, "E208.0.17.3", {"start": v(-48.95, -24.56) * mm, "end": v(-48.95, -26.56) * mm});
            skLineSegment(sketch, "E208.0.18.0", {"start": v(-50.95, -28.56) * mm, "end": v(-48.95, -28.56) * mm});
            skLineSegment(sketch, "E208.0.18.1", {"start": v(-50.95, -28.56) * mm, "end": v(-50.95, -30.56) * mm});
            skLineSegment(sketch, "E208.0.18.2", {"start": v(-50.95, -30.56) * mm, "end": v(-48.95, -30.56) * mm});
            skLineSegment(sketch, "E208.0.18.3", {"start": v(-48.95, -28.56) * mm, "end": v(-48.95, -30.56) * mm});
            skLineSegment(sketch, "E208.0.19.0", {"start": v(-50.95, -32.56) * mm, "end": v(-48.95, -32.56) * mm});
            skLineSegment(sketch, "E208.0.19.1", {"start": v(-50.95, -32.56) * mm, "end": v(-50.95, -34.56) * mm});
            skLineSegment(sketch, "E208.0.19.2", {"start": v(-50.95, -34.56) * mm, "end": v(-48.95, -34.56) * mm});
            skLineSegment(sketch, "E208.0.19.3", {"start": v(-48.95, -32.56) * mm, "end": v(-48.95, -34.56) * mm});
            skLineSegment(sketch, "E208.0.20.0", {"start": v(-50.95, -36.56) * mm, "end": v(-48.95, -36.56) * mm});
            skLineSegment(sketch, "E208.0.20.1", {"start": v(-50.95, -36.56) * mm, "end": v(-50.95, -38.56) * mm});
            skLineSegment(sketch, "E208.0.20.2", {"start": v(-50.95, -38.56) * mm, "end": v(-48.95, -38.56) * mm});
            skLineSegment(sketch, "E208.0.20.3", {"start": v(-48.95, -36.56) * mm, "end": v(-48.95, -38.56) * mm});
            skLineSegment(sketch, "E208.0.21.0", {"start": v(-50.95, -40.56) * mm, "end": v(-48.95, -40.56) * mm});
            skLineSegment(sketch, "E208.0.21.1", {"start": v(-50.95, -40.56) * mm, "end": v(-50.95, -42.56) * mm});
            skLineSegment(sketch, "E208.0.21.2", {"start": v(-50.95, -42.56) * mm, "end": v(-48.95, -42.56) * mm});
            skLineSegment(sketch, "E208.0.21.3", {"start": v(-48.95, -40.56) * mm, "end": v(-48.95, -42.56) * mm});
            skLineSegment(sketch, "E208.1.0.0", {"start": v(-46.95, 43.44) * mm, "end": v(-44.95, 43.44) * mm});
            skLineSegment(sketch, "E208.1.0.1", {"start": v(-46.95, 43.44) * mm, "end": v(-46.95, 41.44) * mm});
            skLineSegment(sketch, "E208.1.0.2", {"start": v(-46.95, 41.44) * mm, "end": v(-44.95, 41.44) * mm});
            skLineSegment(sketch, "E208.1.0.3", {"start": v(-44.95, 43.44) * mm, "end": v(-44.95, 41.44) * mm});
            skLineSegment(sketch, "E208.1.1.0", {"start": v(-46.95, 39.44) * mm, "end": v(-44.95, 39.44) * mm});
            skLineSegment(sketch, "E208.1.1.1", {"start": v(-46.95, 39.44) * mm, "end": v(-46.95, 37.44) * mm});
            skLineSegment(sketch, "E208.1.1.2", {"start": v(-46.95, 37.44) * mm, "end": v(-44.95, 37.44) * mm});
            skLineSegment(sketch, "E208.1.1.3", {"start": v(-44.95, 39.44) * mm, "end": v(-44.95, 37.44) * mm});
            skLineSegment(sketch, "E208.1.2.0", {"start": v(-46.95, 35.44) * mm, "end": v(-44.95, 35.44) * mm});
            skLineSegment(sketch, "E208.1.2.1", {"start": v(-46.95, 35.44) * mm, "end": v(-46.95, 33.44) * mm});
            skLineSegment(sketch, "E208.1.2.2", {"start": v(-46.95, 33.44) * mm, "end": v(-44.95, 33.44) * mm});
            skLineSegment(sketch, "E208.1.2.3", {"start": v(-44.95, 35.44) * mm, "end": v(-44.95, 33.44) * mm});
            skLineSegment(sketch, "E208.1.3.0", {"start": v(-46.95, 31.44) * mm, "end": v(-44.95, 31.44) * mm});
            skLineSegment(sketch, "E208.1.3.1", {"start": v(-46.95, 31.44) * mm, "end": v(-46.95, 29.44) * mm});
            skLineSegment(sketch, "E208.1.3.2", {"start": v(-46.95, 29.44) * mm, "end": v(-44.95, 29.44) * mm});
            skLineSegment(sketch, "E208.1.3.3", {"start": v(-44.95, 31.44) * mm, "end": v(-44.95, 29.44) * mm});
            skLineSegment(sketch, "E208.1.4.0", {"start": v(-46.95, 27.44) * mm, "end": v(-44.95, 27.44) * mm});
            skLineSegment(sketch, "E208.1.4.1", {"start": v(-46.95, 27.44) * mm, "end": v(-46.95, 25.44) * mm});
            skLineSegment(sketch, "E208.1.4.2", {"start": v(-46.95, 25.44) * mm, "end": v(-44.95, 25.44) * mm});
            skLineSegment(sketch, "E208.1.4.3", {"start": v(-44.95, 27.44) * mm, "end": v(-44.95, 25.44) * mm});
            skLineSegment(sketch, "E208.1.5.0", {"start": v(-46.95, 23.44) * mm, "end": v(-44.95, 23.44) * mm});
            skLineSegment(sketch, "E208.1.5.1", {"start": v(-46.95, 23.44) * mm, "end": v(-46.95, 21.44) * mm});
            skLineSegment(sketch, "E208.1.5.2", {"start": v(-46.95, 21.44) * mm, "end": v(-44.95, 21.44) * mm});
            skLineSegment(sketch, "E208.1.5.3", {"start": v(-44.95, 23.44) * mm, "end": v(-44.95, 21.44) * mm});
            skLineSegment(sketch, "E208.1.6.0", {"start": v(-46.95, 19.44) * mm, "end": v(-44.95, 19.44) * mm});
            skLineSegment(sketch, "E208.1.6.1", {"start": v(-46.95, 19.44) * mm, "end": v(-46.95, 17.44) * mm});
            skLineSegment(sketch, "E208.1.6.2", {"start": v(-46.95, 17.44) * mm, "end": v(-44.95, 17.44) * mm});
            skLineSegment(sketch, "E208.1.6.3", {"start": v(-44.95, 19.44) * mm, "end": v(-44.95, 17.44) * mm});
            skLineSegment(sketch, "E208.1.7.0", {"start": v(-46.95, 15.44) * mm, "end": v(-44.95, 15.44) * mm});
            skLineSegment(sketch, "E208.1.7.1", {"start": v(-46.95, 15.44) * mm, "end": v(-46.95, 13.44) * mm});
            skLineSegment(sketch, "E208.1.7.2", {"start": v(-46.95, 13.44) * mm, "end": v(-44.95, 13.44) * mm});
            skLineSegment(sketch, "E208.1.7.3", {"start": v(-44.95, 15.44) * mm, "end": v(-44.95, 13.44) * mm});
            skLineSegment(sketch, "E208.1.8.0", {"start": v(-46.95, 11.44) * mm, "end": v(-44.95, 11.44) * mm});
            skLineSegment(sketch, "E208.1.8.1", {"start": v(-46.95, 11.44) * mm, "end": v(-46.95, 9.44) * mm});
            skLineSegment(sketch, "E208.1.8.2", {"start": v(-46.95, 9.44) * mm, "end": v(-44.95, 9.44) * mm});
            skLineSegment(sketch, "E208.1.8.3", {"start": v(-44.95, 11.44) * mm, "end": v(-44.95, 9.44) * mm});
            skLineSegment(sketch, "E208.1.9.0", {"start": v(-46.95, 7.44) * mm, "end": v(-44.95, 7.44) * mm});
            skLineSegment(sketch, "E208.1.9.1", {"start": v(-46.95, 7.44) * mm, "end": v(-46.95, 5.44) * mm});
            skLineSegment(sketch, "E208.1.9.2", {"start": v(-46.95, 5.44) * mm, "end": v(-44.95, 5.44) * mm});
            skLineSegment(sketch, "E208.1.9.3", {"start": v(-44.95, 7.44) * mm, "end": v(-44.95, 5.44) * mm});
            skLineSegment(sketch, "E208.1.10.0", {"start": v(-46.95, 3.44) * mm, "end": v(-44.95, 3.44) * mm});
            skLineSegment(sketch, "E208.1.10.1", {"start": v(-46.95, 3.44) * mm, "end": v(-46.95, 1.44) * mm});
            skLineSegment(sketch, "E208.1.10.2", {"start": v(-46.95, 1.44) * mm, "end": v(-44.95, 1.44) * mm});
            skLineSegment(sketch, "E208.1.10.3", {"start": v(-44.95, 3.44) * mm, "end": v(-44.95, 1.44) * mm});
            skLineSegment(sketch, "E208.1.11.0", {"start": v(-46.95, -0.56) * mm, "end": v(-44.95, -0.56) * mm});
            skLineSegment(sketch, "E208.1.11.1", {"start": v(-46.95, -0.56) * mm, "end": v(-46.95, -2.56) * mm});
            skLineSegment(sketch, "E208.1.11.2", {"start": v(-46.95, -2.56) * mm, "end": v(-44.95, -2.56) * mm});
            skLineSegment(sketch, "E208.1.11.3", {"start": v(-44.95, -0.56) * mm, "end": v(-44.95, -2.56) * mm});
            skLineSegment(sketch, "E208.1.12.0", {"start": v(-46.95, -4.56) * mm, "end": v(-44.95, -4.56) * mm});
            skLineSegment(sketch, "E208.1.12.1", {"start": v(-46.95, -4.56) * mm, "end": v(-46.95, -6.56) * mm});
            skLineSegment(sketch, "E208.1.12.2", {"start": v(-46.95, -6.56) * mm, "end": v(-44.95, -6.56) * mm});
            skLineSegment(sketch, "E208.1.12.3", {"start": v(-44.95, -4.56) * mm, "end": v(-44.95, -6.56) * mm});
            skLineSegment(sketch, "E208.1.13.0", {"start": v(-46.95, -8.56) * mm, "end": v(-44.95, -8.56) * mm});
            skLineSegment(sketch, "E208.1.13.1", {"start": v(-46.95, -8.56) * mm, "end": v(-46.95, -10.56) * mm});
            skLineSegment(sketch, "E208.1.13.2", {"start": v(-46.95, -10.56) * mm, "end": v(-44.95, -10.56) * mm});
            skLineSegment(sketch, "E208.1.13.3", {"start": v(-44.95, -8.56) * mm, "end": v(-44.95, -10.56) * mm});
            skLineSegment(sketch, "E208.1.14.0", {"start": v(-46.95, -12.56) * mm, "end": v(-44.95, -12.56) * mm});
            skLineSegment(sketch, "E208.1.14.1", {"start": v(-46.95, -12.56) * mm, "end": v(-46.95, -14.56) * mm});
            skLineSegment(sketch, "E208.1.14.2", {"start": v(-46.95, -14.56) * mm, "end": v(-44.95, -14.56) * mm});
            skLineSegment(sketch, "E208.1.14.3", {"start": v(-44.95, -12.56) * mm, "end": v(-44.95, -14.56) * mm});
            skLineSegment(sketch, "E208.1.15.0", {"start": v(-46.95, -16.56) * mm, "end": v(-44.95, -16.56) * mm});
            skLineSegment(sketch, "E208.1.15.1", {"start": v(-46.95, -16.56) * mm, "end": v(-46.95, -18.56) * mm});
            skLineSegment(sketch, "E208.1.15.2", {"start": v(-46.95, -18.56) * mm, "end": v(-44.95, -18.56) * mm});
            skLineSegment(sketch, "E208.1.15.3", {"start": v(-44.95, -16.56) * mm, "end": v(-44.95, -18.56) * mm});
            skLineSegment(sketch, "E208.1.16.0", {"start": v(-46.95, -20.56) * mm, "end": v(-44.95, -20.56) * mm});
            skLineSegment(sketch, "E208.1.16.1", {"start": v(-46.95, -20.56) * mm, "end": v(-46.95, -22.56) * mm});
            skLineSegment(sketch, "E208.1.16.2", {"start": v(-46.95, -22.56) * mm, "end": v(-44.95, -22.56) * mm});
            skLineSegment(sketch, "E208.1.16.3", {"start": v(-44.95, -20.56) * mm, "end": v(-44.95, -22.56) * mm});
            skLineSegment(sketch, "E208.1.17.0", {"start": v(-46.95, -24.56) * mm, "end": v(-44.95, -24.56) * mm});
            skLineSegment(sketch, "E208.1.17.1", {"start": v(-46.95, -24.56) * mm, "end": v(-46.95, -26.56) * mm});
            skLineSegment(sketch, "E208.1.17.2", {"start": v(-46.95, -26.56) * mm, "end": v(-44.95, -26.56) * mm});
            skLineSegment(sketch, "E208.1.17.3", {"start": v(-44.95, -24.56) * mm, "end": v(-44.95, -26.56) * mm});
            skLineSegment(sketch, "E208.1.18.0", {"start": v(-46.95, -28.56) * mm, "end": v(-44.95, -28.56) * mm});
            skLineSegment(sketch, "E208.1.18.1", {"start": v(-46.95, -28.56) * mm, "end": v(-46.95, -30.56) * mm});
            skLineSegment(sketch, "E208.1.18.2", {"start": v(-46.95, -30.56) * mm, "end": v(-44.95, -30.56) * mm});
            skLineSegment(sketch, "E208.1.18.3", {"start": v(-44.95, -28.56) * mm, "end": v(-44.95, -30.56) * mm});
            skLineSegment(sketch, "E208.1.19.0", {"start": v(-46.95, -32.56) * mm, "end": v(-44.95, -32.56) * mm});
            skLineSegment(sketch, "E208.1.19.1", {"start": v(-46.95, -32.56) * mm, "end": v(-46.95, -34.56) * mm});
            skLineSegment(sketch, "E208.1.19.2", {"start": v(-46.95, -34.56) * mm, "end": v(-44.95, -34.56) * mm});
            skLineSegment(sketch, "E208.1.19.3", {"start": v(-44.95, -32.56) * mm, "end": v(-44.95, -34.56) * mm});
            skLineSegment(sketch, "E208.1.20.0", {"start": v(-46.95, -36.56) * mm, "end": v(-44.95, -36.56) * mm});
            skLineSegment(sketch, "E208.1.20.1", {"start": v(-46.95, -36.56) * mm, "end": v(-46.95, -38.56) * mm});
            skLineSegment(sketch, "E208.1.20.2", {"start": v(-46.95, -38.56) * mm, "end": v(-44.95, -38.56) * mm});
            skLineSegment(sketch, "E208.1.20.3", {"start": v(-44.95, -36.56) * mm, "end": v(-44.95, -38.56) * mm});
            skLineSegment(sketch, "E208.1.21.0", {"start": v(-46.95, -40.56) * mm, "end": v(-44.95, -40.56) * mm});
            skLineSegment(sketch, "E208.1.21.1", {"start": v(-46.95, -40.56) * mm, "end": v(-46.95, -42.56) * mm});
            skLineSegment(sketch, "E208.1.21.2", {"start": v(-46.95, -42.56) * mm, "end": v(-44.95, -42.56) * mm});
            skLineSegment(sketch, "E208.1.21.3", {"start": v(-44.95, -40.56) * mm, "end": v(-44.95, -42.56) * mm});
            skLineSegment(sketch, "E208.2.0.0", {"start": v(-42.95, 43.44) * mm, "end": v(-40.95, 43.44) * mm});
            skLineSegment(sketch, "E208.2.0.1", {"start": v(-42.95, 43.44) * mm, "end": v(-42.95, 41.44) * mm});
            skLineSegment(sketch, "E208.2.0.2", {"start": v(-42.95, 41.44) * mm, "end": v(-40.95, 41.44) * mm});
            skLineSegment(sketch, "E208.2.0.3", {"start": v(-40.95, 43.44) * mm, "end": v(-40.95, 41.44) * mm});
            skLineSegment(sketch, "E208.2.1.0", {"start": v(-42.95, 39.44) * mm, "end": v(-40.95, 39.44) * mm});
            skLineSegment(sketch, "E208.2.1.1", {"start": v(-42.95, 39.44) * mm, "end": v(-42.95, 37.44) * mm});
            skLineSegment(sketch, "E208.2.1.2", {"start": v(-42.95, 37.44) * mm, "end": v(-40.95, 37.44) * mm});
            skLineSegment(sketch, "E208.2.1.3", {"start": v(-40.95, 39.44) * mm, "end": v(-40.95, 37.44) * mm});
            skLineSegment(sketch, "E208.2.2.0", {"start": v(-42.95, 35.44) * mm, "end": v(-40.95, 35.44) * mm});
            skLineSegment(sketch, "E208.2.2.1", {"start": v(-42.95, 35.44) * mm, "end": v(-42.95, 33.44) * mm});
            skLineSegment(sketch, "E208.2.2.2", {"start": v(-42.95, 33.44) * mm, "end": v(-40.95, 33.44) * mm});
            skLineSegment(sketch, "E208.2.2.3", {"start": v(-40.95, 35.44) * mm, "end": v(-40.95, 33.44) * mm});
            skLineSegment(sketch, "E208.2.3.0", {"start": v(-42.95, 31.44) * mm, "end": v(-40.95, 31.44) * mm});
            skLineSegment(sketch, "E208.2.3.1", {"start": v(-42.95, 31.44) * mm, "end": v(-42.95, 29.44) * mm});
            skLineSegment(sketch, "E208.2.3.2", {"start": v(-42.95, 29.44) * mm, "end": v(-40.95, 29.44) * mm});
            skLineSegment(sketch, "E208.2.3.3", {"start": v(-40.95, 31.44) * mm, "end": v(-40.95, 29.44) * mm});
            skLineSegment(sketch, "E208.2.4.0", {"start": v(-42.95, 27.44) * mm, "end": v(-40.95, 27.44) * mm});
            skLineSegment(sketch, "E208.2.4.1", {"start": v(-42.95, 27.44) * mm, "end": v(-42.95, 25.44) * mm});
            skLineSegment(sketch, "E208.2.4.2", {"start": v(-42.95, 25.44) * mm, "end": v(-40.95, 25.44) * mm});
            skLineSegment(sketch, "E208.2.4.3", {"start": v(-40.95, 27.44) * mm, "end": v(-40.95, 25.44) * mm});
            skLineSegment(sketch, "E208.2.5.0", {"start": v(-42.95, 23.44) * mm, "end": v(-40.95, 23.44) * mm});
            skLineSegment(sketch, "E208.2.5.1", {"start": v(-42.95, 23.44) * mm, "end": v(-42.95, 21.44) * mm});
            skLineSegment(sketch, "E208.2.5.2", {"start": v(-42.95, 21.44) * mm, "end": v(-40.95, 21.44) * mm});
            skLineSegment(sketch, "E208.2.5.3", {"start": v(-40.95, 23.44) * mm, "end": v(-40.95, 21.44) * mm});
            skLineSegment(sketch, "E208.2.6.0", {"start": v(-42.95, 19.44) * mm, "end": v(-40.95, 19.44) * mm});
            skLineSegment(sketch, "E208.2.6.1", {"start": v(-42.95, 19.44) * mm, "end": v(-42.95, 17.44) * mm});
            skLineSegment(sketch, "E208.2.6.2", {"start": v(-42.95, 17.44) * mm, "end": v(-40.95, 17.44) * mm});
            skLineSegment(sketch, "E208.2.6.3", {"start": v(-40.95, 19.44) * mm, "end": v(-40.95, 17.44) * mm});
            skLineSegment(sketch, "E208.2.7.0", {"start": v(-42.95, 15.44) * mm, "end": v(-40.95, 15.44) * mm});
            skLineSegment(sketch, "E208.2.7.1", {"start": v(-42.95, 15.44) * mm, "end": v(-42.95, 13.44) * mm});
            skLineSegment(sketch, "E208.2.7.2", {"start": v(-42.95, 13.44) * mm, "end": v(-40.95, 13.44) * mm});
            skLineSegment(sketch, "E208.2.7.3", {"start": v(-40.95, 15.44) * mm, "end": v(-40.95, 13.44) * mm});
            skLineSegment(sketch, "E208.2.8.0", {"start": v(-42.95, 11.44) * mm, "end": v(-40.95, 11.44) * mm});
            skLineSegment(sketch, "E208.2.8.1", {"start": v(-42.95, 11.44) * mm, "end": v(-42.95, 9.44) * mm});
            skLineSegment(sketch, "E208.2.8.2", {"start": v(-42.95, 9.44) * mm, "end": v(-40.95, 9.44) * mm});
            skLineSegment(sketch, "E208.2.8.3", {"start": v(-40.95, 11.44) * mm, "end": v(-40.95, 9.44) * mm});
            skLineSegment(sketch, "E208.2.9.0", {"start": v(-42.95, 7.44) * mm, "end": v(-40.95, 7.44) * mm});
            skLineSegment(sketch, "E208.2.9.1", {"start": v(-42.95, 7.44) * mm, "end": v(-42.95, 5.44) * mm});
            skLineSegment(sketch, "E208.2.9.2", {"start": v(-42.95, 5.44) * mm, "end": v(-40.95, 5.44) * mm});
            skLineSegment(sketch, "E208.2.9.3", {"start": v(-40.95, 7.44) * mm, "end": v(-40.95, 5.44) * mm});
            skLineSegment(sketch, "E208.2.10.0", {"start": v(-42.95, 3.44) * mm, "end": v(-40.95, 3.44) * mm});
            skLineSegment(sketch, "E208.2.10.1", {"start": v(-42.95, 3.44) * mm, "end": v(-42.95, 1.44) * mm});
            skLineSegment(sketch, "E208.2.10.2", {"start": v(-42.95, 1.44) * mm, "end": v(-40.95, 1.44) * mm});
            skLineSegment(sketch, "E208.2.10.3", {"start": v(-40.95, 3.44) * mm, "end": v(-40.95, 1.44) * mm});
            skLineSegment(sketch, "E208.2.11.0", {"start": v(-42.95, -0.56) * mm, "end": v(-40.95, -0.56) * mm});
            skLineSegment(sketch, "E208.2.11.1", {"start": v(-42.95, -0.56) * mm, "end": v(-42.95, -2.56) * mm});
            skLineSegment(sketch, "E208.2.11.2", {"start": v(-42.95, -2.56) * mm, "end": v(-40.95, -2.56) * mm});
            skLineSegment(sketch, "E208.2.11.3", {"start": v(-40.95, -0.56) * mm, "end": v(-40.95, -2.56) * mm});
            skLineSegment(sketch, "E208.2.12.0", {"start": v(-42.95, -4.56) * mm, "end": v(-40.95, -4.56) * mm});
            skLineSegment(sketch, "E208.2.12.1", {"start": v(-42.95, -4.56) * mm, "end": v(-42.95, -6.56) * mm});
            skLineSegment(sketch, "E208.2.12.2", {"start": v(-42.95, -6.56) * mm, "end": v(-40.95, -6.56) * mm});
            skLineSegment(sketch, "E208.2.12.3", {"start": v(-40.95, -4.56) * mm, "end": v(-40.95, -6.56) * mm});
            skLineSegment(sketch, "E208.2.13.0", {"start": v(-42.95, -8.56) * mm, "end": v(-40.95, -8.56) * mm});
            skLineSegment(sketch, "E208.2.13.1", {"start": v(-42.95, -8.56) * mm, "end": v(-42.95, -10.56) * mm});
            skLineSegment(sketch, "E208.2.13.2", {"start": v(-42.95, -10.56) * mm, "end": v(-40.95, -10.56) * mm});
            skLineSegment(sketch, "E208.2.13.3", {"start": v(-40.95, -8.56) * mm, "end": v(-40.95, -10.56) * mm});
            skLineSegment(sketch, "E208.2.14.0", {"start": v(-42.95, -12.56) * mm, "end": v(-40.95, -12.56) * mm});
            skLineSegment(sketch, "E208.2.14.1", {"start": v(-42.95, -12.56) * mm, "end": v(-42.95, -14.56) * mm});
            skLineSegment(sketch, "E208.2.14.2", {"start": v(-42.95, -14.56) * mm, "end": v(-40.95, -14.56) * mm});
            skLineSegment(sketch, "E208.2.14.3", {"start": v(-40.95, -12.56) * mm, "end": v(-40.95, -14.56) * mm});
            skLineSegment(sketch, "E208.2.15.0", {"start": v(-42.95, -16.56) * mm, "end": v(-40.95, -16.56) * mm});
            skLineSegment(sketch, "E208.2.15.1", {"start": v(-42.95, -16.56) * mm, "end": v(-42.95, -18.56) * mm});
            skLineSegment(sketch, "E208.2.15.2", {"start": v(-42.95, -18.56) * mm, "end": v(-40.95, -18.56) * mm});
            skLineSegment(sketch, "E208.2.15.3", {"start": v(-40.95, -16.56) * mm, "end": v(-40.95, -18.56) * mm});
            skLineSegment(sketch, "E208.2.16.0", {"start": v(-42.95, -20.56) * mm, "end": v(-40.95, -20.56) * mm});
            skLineSegment(sketch, "E208.2.16.1", {"start": v(-42.95, -20.56) * mm, "end": v(-42.95, -22.56) * mm});
            skLineSegment(sketch, "E208.2.16.2", {"start": v(-42.95, -22.56) * mm, "end": v(-40.95, -22.56) * mm});
            skLineSegment(sketch, "E208.2.16.3", {"start": v(-40.95, -20.56) * mm, "end": v(-40.95, -22.56) * mm});
            skLineSegment(sketch, "E208.2.17.0", {"start": v(-42.95, -24.56) * mm, "end": v(-40.95, -24.56) * mm});
            skLineSegment(sketch, "E208.2.17.1", {"start": v(-42.95, -24.56) * mm, "end": v(-42.95, -26.56) * mm});
            skLineSegment(sketch, "E208.2.17.2", {"start": v(-42.95, -26.56) * mm, "end": v(-40.95, -26.56) * mm});
            skLineSegment(sketch, "E208.2.17.3", {"start": v(-40.95, -24.56) * mm, "end": v(-40.95, -26.56) * mm});
            skLineSegment(sketch, "E208.2.18.0", {"start": v(-42.95, -28.56) * mm, "end": v(-40.95, -28.56) * mm});
            skLineSegment(sketch, "E208.2.18.1", {"start": v(-42.95, -28.56) * mm, "end": v(-42.95, -30.56) * mm});
            skLineSegment(sketch, "E208.2.18.2", {"start": v(-42.95, -30.56) * mm, "end": v(-40.95, -30.56) * mm});
            skLineSegment(sketch, "E208.2.18.3", {"start": v(-40.95, -28.56) * mm, "end": v(-40.95, -30.56) * mm});
            skLineSegment(sketch, "E208.2.19.0", {"start": v(-42.95, -32.56) * mm, "end": v(-40.95, -32.56) * mm});
            skLineSegment(sketch, "E208.2.19.1", {"start": v(-42.95, -32.56) * mm, "end": v(-42.95, -34.56) * mm});
            skLineSegment(sketch, "E208.2.19.2", {"start": v(-42.95, -34.56) * mm, "end": v(-40.95, -34.56) * mm});
            skLineSegment(sketch, "E208.2.19.3", {"start": v(-40.95, -32.56) * mm, "end": v(-40.95, -34.56) * mm});
            skLineSegment(sketch, "E208.2.20.0", {"start": v(-42.95, -36.56) * mm, "end": v(-40.95, -36.56) * mm});
            skLineSegment(sketch, "E208.2.20.1", {"start": v(-42.95, -36.56) * mm, "end": v(-42.95, -38.56) * mm});
            skLineSegment(sketch, "E208.2.20.2", {"start": v(-42.95, -38.56) * mm, "end": v(-40.95, -38.56) * mm});
            skLineSegment(sketch, "E208.2.20.3", {"start": v(-40.95, -36.56) * mm, "end": v(-40.95, -38.56) * mm});
            skLineSegment(sketch, "E208.2.21.0", {"start": v(-42.95, -40.56) * mm, "end": v(-40.95, -40.56) * mm});
            skLineSegment(sketch, "E208.2.21.1", {"start": v(-42.95, -40.56) * mm, "end": v(-42.95, -42.56) * mm});
            skLineSegment(sketch, "E208.2.21.2", {"start": v(-42.95, -42.56) * mm, "end": v(-40.95, -42.56) * mm});
            skLineSegment(sketch, "E208.2.21.3", {"start": v(-40.95, -40.56) * mm, "end": v(-40.95, -42.56) * mm});
            skLineSegment(sketch, "E208.3.0.0", {"start": v(-38.95, 43.44) * mm, "end": v(-36.95, 43.44) * mm});
            skLineSegment(sketch, "E208.3.0.1", {"start": v(-38.95, 43.44) * mm, "end": v(-38.95, 41.44) * mm});
            skLineSegment(sketch, "E208.3.0.2", {"start": v(-38.95, 41.44) * mm, "end": v(-36.95, 41.44) * mm});
            skLineSegment(sketch, "E208.3.0.3", {"start": v(-36.95, 43.44) * mm, "end": v(-36.95, 41.44) * mm});
            skLineSegment(sketch, "E208.3.1.0", {"start": v(-38.95, 39.44) * mm, "end": v(-36.95, 39.44) * mm});
            skLineSegment(sketch, "E208.3.1.1", {"start": v(-38.95, 39.44) * mm, "end": v(-38.95, 37.44) * mm});
            skLineSegment(sketch, "E208.3.1.2", {"start": v(-38.95, 37.44) * mm, "end": v(-36.95, 37.44) * mm});
            skLineSegment(sketch, "E208.3.1.3", {"start": v(-36.95, 39.44) * mm, "end": v(-36.95, 37.44) * mm});
            skLineSegment(sketch, "E208.3.2.0", {"start": v(-38.95, 35.44) * mm, "end": v(-36.95, 35.44) * mm});
            skLineSegment(sketch, "E208.3.2.1", {"start": v(-38.95, 35.44) * mm, "end": v(-38.95, 33.44) * mm});
            skLineSegment(sketch, "E208.3.2.2", {"start": v(-38.95, 33.44) * mm, "end": v(-36.95, 33.44) * mm});
            skLineSegment(sketch, "E208.3.2.3", {"start": v(-36.95, 35.44) * mm, "end": v(-36.95, 33.44) * mm});
            skLineSegment(sketch, "E208.3.3.0", {"start": v(-38.95, 31.44) * mm, "end": v(-36.95, 31.44) * mm});
            skLineSegment(sketch, "E208.3.3.1", {"start": v(-38.95, 31.44) * mm, "end": v(-38.95, 29.44) * mm});
            skLineSegment(sketch, "E208.3.3.2", {"start": v(-38.95, 29.44) * mm, "end": v(-36.95, 29.44) * mm});
            skLineSegment(sketch, "E208.3.3.3", {"start": v(-36.95, 31.44) * mm, "end": v(-36.95, 29.44) * mm});
            skLineSegment(sketch, "E208.3.4.0", {"start": v(-38.95, 27.44) * mm, "end": v(-36.95, 27.44) * mm});
            skLineSegment(sketch, "E208.3.4.1", {"start": v(-38.95, 27.44) * mm, "end": v(-38.95, 25.44) * mm});
            skLineSegment(sketch, "E208.3.4.2", {"start": v(-38.95, 25.44) * mm, "end": v(-36.95, 25.44) * mm});
            skLineSegment(sketch, "E208.3.4.3", {"start": v(-36.95, 27.44) * mm, "end": v(-36.95, 25.44) * mm});
            skLineSegment(sketch, "E208.3.5.0", {"start": v(-38.95, 23.44) * mm, "end": v(-36.95, 23.44) * mm});
            skLineSegment(sketch, "E208.3.5.1", {"start": v(-38.95, 23.44) * mm, "end": v(-38.95, 21.44) * mm});
            skLineSegment(sketch, "E208.3.5.2", {"start": v(-38.95, 21.44) * mm, "end": v(-36.95, 21.44) * mm});
            skLineSegment(sketch, "E208.3.5.3", {"start": v(-36.95, 23.44) * mm, "end": v(-36.95, 21.44) * mm});
            skLineSegment(sketch, "E208.3.6.0", {"start": v(-38.95, 19.44) * mm, "end": v(-36.95, 19.44) * mm});
            skLineSegment(sketch, "E208.3.6.1", {"start": v(-38.95, 19.44) * mm, "end": v(-38.95, 17.44) * mm});
            skLineSegment(sketch, "E208.3.6.2", {"start": v(-38.95, 17.44) * mm, "end": v(-36.95, 17.44) * mm});
            skLineSegment(sketch, "E208.3.6.3", {"start": v(-36.95, 19.44) * mm, "end": v(-36.95, 17.44) * mm});
            skLineSegment(sketch, "E208.3.7.0", {"start": v(-38.95, 15.44) * mm, "end": v(-36.95, 15.44) * mm});
            skLineSegment(sketch, "E208.3.7.1", {"start": v(-38.95, 15.44) * mm, "end": v(-38.95, 13.44) * mm});
            skLineSegment(sketch, "E208.3.7.2", {"start": v(-38.95, 13.44) * mm, "end": v(-36.95, 13.44) * mm});
            skLineSegment(sketch, "E208.3.7.3", {"start": v(-36.95, 15.44) * mm, "end": v(-36.95, 13.44) * mm});
            skLineSegment(sketch, "E208.3.8.0", {"start": v(-38.95, 11.44) * mm, "end": v(-36.95, 11.44) * mm});
            skLineSegment(sketch, "E208.3.8.1", {"start": v(-38.95, 11.44) * mm, "end": v(-38.95, 9.44) * mm});
            skLineSegment(sketch, "E208.3.8.2", {"start": v(-38.95, 9.44) * mm, "end": v(-36.95, 9.44) * mm});
            skLineSegment(sketch, "E208.3.8.3", {"start": v(-36.95, 11.44) * mm, "end": v(-36.95, 9.44) * mm});
            skLineSegment(sketch, "E208.3.9.0", {"start": v(-38.95, 7.44) * mm, "end": v(-36.95, 7.44) * mm});
            skLineSegment(sketch, "E208.3.9.1", {"start": v(-38.95, 7.44) * mm, "end": v(-38.95, 5.44) * mm});
            skLineSegment(sketch, "E208.3.9.2", {"start": v(-38.95, 5.44) * mm, "end": v(-36.95, 5.44) * mm});
            skLineSegment(sketch, "E208.3.9.3", {"start": v(-36.95, 7.44) * mm, "end": v(-36.95, 5.44) * mm});
            skLineSegment(sketch, "E208.3.10.0", {"start": v(-38.95, 3.44) * mm, "end": v(-36.95, 3.44) * mm});
            skLineSegment(sketch, "E208.3.10.1", {"start": v(-38.95, 3.44) * mm, "end": v(-38.95, 1.44) * mm});
            skLineSegment(sketch, "E208.3.10.2", {"start": v(-38.95, 1.44) * mm, "end": v(-36.95, 1.44) * mm});
            skLineSegment(sketch, "E208.3.10.3", {"start": v(-36.95, 3.44) * mm, "end": v(-36.95, 1.44) * mm});
            skLineSegment(sketch, "E208.3.11.0", {"start": v(-38.95, -0.56) * mm, "end": v(-36.95, -0.56) * mm});
            skLineSegment(sketch, "E208.3.11.1", {"start": v(-38.95, -0.56) * mm, "end": v(-38.95, -2.56) * mm});
            skLineSegment(sketch, "E208.3.11.2", {"start": v(-38.95, -2.56) * mm, "end": v(-36.95, -2.56) * mm});
            skLineSegment(sketch, "E208.3.11.3", {"start": v(-36.95, -0.56) * mm, "end": v(-36.95, -2.56) * mm});
            skLineSegment(sketch, "E208.3.12.0", {"start": v(-38.95, -4.56) * mm, "end": v(-36.95, -4.56) * mm});
            skLineSegment(sketch, "E208.3.12.1", {"start": v(-38.95, -4.56) * mm, "end": v(-38.95, -6.56) * mm});
            skLineSegment(sketch, "E208.3.12.2", {"start": v(-38.95, -6.56) * mm, "end": v(-36.95, -6.56) * mm});
            skLineSegment(sketch, "E208.3.12.3", {"start": v(-36.95, -4.56) * mm, "end": v(-36.95, -6.56) * mm});
            skLineSegment(sketch, "E208.3.13.0", {"start": v(-38.95, -8.56) * mm, "end": v(-36.95, -8.56) * mm});
            skLineSegment(sketch, "E208.3.13.1", {"start": v(-38.95, -8.56) * mm, "end": v(-38.95, -10.56) * mm});
            skLineSegment(sketch, "E208.3.13.2", {"start": v(-38.95, -10.56) * mm, "end": v(-36.95, -10.56) * mm});
            skLineSegment(sketch, "E208.3.13.3", {"start": v(-36.95, -8.56) * mm, "end": v(-36.95, -10.56) * mm});
            skLineSegment(sketch, "E208.3.14.0", {"start": v(-38.95, -12.56) * mm, "end": v(-36.95, -12.56) * mm});
            skLineSegment(sketch, "E208.3.14.1", {"start": v(-38.95, -12.56) * mm, "end": v(-38.95, -14.56) * mm});
            skLineSegment(sketch, "E208.3.14.2", {"start": v(-38.95, -14.56) * mm, "end": v(-36.95, -14.56) * mm});
            skLineSegment(sketch, "E208.3.14.3", {"start": v(-36.95, -12.56) * mm, "end": v(-36.95, -14.56) * mm});
            skLineSegment(sketch, "E208.3.15.0", {"start": v(-38.95, -16.56) * mm, "end": v(-36.95, -16.56) * mm});
            skLineSegment(sketch, "E208.3.15.1", {"start": v(-38.95, -16.56) * mm, "end": v(-38.95, -18.56) * mm});
            skLineSegment(sketch, "E208.3.15.2", {"start": v(-38.95, -18.56) * mm, "end": v(-36.95, -18.56) * mm});
            skLineSegment(sketch, "E208.3.15.3", {"start": v(-36.95, -16.56) * mm, "end": v(-36.95, -18.56) * mm});
            skLineSegment(sketch, "E208.3.16.0", {"start": v(-38.95, -20.56) * mm, "end": v(-36.95, -20.56) * mm});
            skLineSegment(sketch, "E208.3.16.1", {"start": v(-38.95, -20.56) * mm, "end": v(-38.95, -22.56) * mm});
            skLineSegment(sketch, "E208.3.16.2", {"start": v(-38.95, -22.56) * mm, "end": v(-36.95, -22.56) * mm});
            skLineSegment(sketch, "E208.3.16.3", {"start": v(-36.95, -20.56) * mm, "end": v(-36.95, -22.56) * mm});
            skLineSegment(sketch, "E208.3.17.0", {"start": v(-38.95, -24.56) * mm, "end": v(-36.95, -24.56) * mm});
            skLineSegment(sketch, "E208.3.17.1", {"start": v(-38.95, -24.56) * mm, "end": v(-38.95, -26.56) * mm});
            skLineSegment(sketch, "E208.3.17.2", {"start": v(-38.95, -26.56) * mm, "end": v(-36.95, -26.56) * mm});
            skLineSegment(sketch, "E208.3.17.3", {"start": v(-36.95, -24.56) * mm, "end": v(-36.95, -26.56) * mm});
            skLineSegment(sketch, "E208.3.18.0", {"start": v(-38.95, -28.56) * mm, "end": v(-36.95, -28.56) * mm});
            skLineSegment(sketch, "E208.3.18.1", {"start": v(-38.95, -28.56) * mm, "end": v(-38.95, -30.56) * mm});
            skLineSegment(sketch, "E208.3.18.2", {"start": v(-38.95, -30.56) * mm, "end": v(-36.95, -30.56) * mm});
            skLineSegment(sketch, "E208.3.18.3", {"start": v(-36.95, -28.56) * mm, "end": v(-36.95, -30.56) * mm});
            skLineSegment(sketch, "E208.3.19.0", {"start": v(-38.95, -32.56) * mm, "end": v(-36.95, -32.56) * mm});
            skLineSegment(sketch, "E208.3.19.1", {"start": v(-38.95, -32.56) * mm, "end": v(-38.95, -34.56) * mm});
            skLineSegment(sketch, "E208.3.19.2", {"start": v(-38.95, -34.56) * mm, "end": v(-36.95, -34.56) * mm});
            skLineSegment(sketch, "E208.3.19.3", {"start": v(-36.95, -32.56) * mm, "end": v(-36.95, -34.56) * mm});
            skLineSegment(sketch, "E208.3.20.0", {"start": v(-38.95, -36.56) * mm, "end": v(-36.95, -36.56) * mm});
            skLineSegment(sketch, "E208.3.20.1", {"start": v(-38.95, -36.56) * mm, "end": v(-38.95, -38.56) * mm});
            skLineSegment(sketch, "E208.3.20.2", {"start": v(-38.95, -38.56) * mm, "end": v(-36.95, -38.56) * mm});
            skLineSegment(sketch, "E208.3.20.3", {"start": v(-36.95, -36.56) * mm, "end": v(-36.95, -38.56) * mm});
            skLineSegment(sketch, "E208.3.21.0", {"start": v(-38.95, -40.56) * mm, "end": v(-36.95, -40.56) * mm});
            skLineSegment(sketch, "E208.3.21.1", {"start": v(-38.95, -40.56) * mm, "end": v(-38.95, -42.56) * mm});
            skLineSegment(sketch, "E208.3.21.2", {"start": v(-38.95, -42.56) * mm, "end": v(-36.95, -42.56) * mm});
            skLineSegment(sketch, "E208.3.21.3", {"start": v(-36.95, -40.56) * mm, "end": v(-36.95, -42.56) * mm});
            skLineSegment(sketch, "E208.4.0.0", {"start": v(-34.95, 43.44) * mm, "end": v(-32.95, 43.44) * mm});
            skLineSegment(sketch, "E208.4.0.1", {"start": v(-34.95, 43.44) * mm, "end": v(-34.95, 41.44) * mm});
            skLineSegment(sketch, "E208.4.0.2", {"start": v(-34.95, 41.44) * mm, "end": v(-32.95, 41.44) * mm});
            skLineSegment(sketch, "E208.4.0.3", {"start": v(-32.95, 43.44) * mm, "end": v(-32.95, 41.44) * mm});
            skLineSegment(sketch, "E208.4.1.0", {"start": v(-34.95, 39.44) * mm, "end": v(-32.95, 39.44) * mm});
            skLineSegment(sketch, "E208.4.1.1", {"start": v(-34.95, 39.44) * mm, "end": v(-34.95, 37.44) * mm});
            skLineSegment(sketch, "E208.4.1.2", {"start": v(-34.95, 37.44) * mm, "end": v(-32.95, 37.44) * mm});
            skLineSegment(sketch, "E208.4.1.3", {"start": v(-32.95, 39.44) * mm, "end": v(-32.95, 37.44) * mm});
            skLineSegment(sketch, "E208.4.2.0", {"start": v(-34.95, 35.44) * mm, "end": v(-32.95, 35.44) * mm});
            skLineSegment(sketch, "E208.4.2.1", {"start": v(-34.95, 35.44) * mm, "end": v(-34.95, 33.44) * mm});
            skLineSegment(sketch, "E208.4.2.2", {"start": v(-34.95, 33.44) * mm, "end": v(-32.95, 33.44) * mm});
            skLineSegment(sketch, "E208.4.2.3", {"start": v(-32.95, 35.44) * mm, "end": v(-32.95, 33.44) * mm});
            skLineSegment(sketch, "E208.4.3.0", {"start": v(-34.95, 31.44) * mm, "end": v(-32.95, 31.44) * mm});
            skLineSegment(sketch, "E208.4.3.1", {"start": v(-34.95, 31.44) * mm, "end": v(-34.95, 29.44) * mm});
            skLineSegment(sketch, "E208.4.3.2", {"start": v(-34.95, 29.44) * mm, "end": v(-32.95, 29.44) * mm});
            skLineSegment(sketch, "E208.4.3.3", {"start": v(-32.95, 31.44) * mm, "end": v(-32.95, 29.44) * mm});
            skLineSegment(sketch, "E208.4.4.0", {"start": v(-34.95, 27.44) * mm, "end": v(-32.95, 27.44) * mm});
            skLineSegment(sketch, "E208.4.4.1", {"start": v(-34.95, 27.44) * mm, "end": v(-34.95, 25.44) * mm});
            skLineSegment(sketch, "E208.4.4.2", {"start": v(-34.95, 25.44) * mm, "end": v(-32.95, 25.44) * mm});
            skLineSegment(sketch, "E208.4.4.3", {"start": v(-32.95, 27.44) * mm, "end": v(-32.95, 25.44) * mm});
            skLineSegment(sketch, "E208.4.5.0", {"start": v(-34.95, 23.44) * mm, "end": v(-32.95, 23.44) * mm});
            skLineSegment(sketch, "E208.4.5.1", {"start": v(-34.95, 23.44) * mm, "end": v(-34.95, 21.44) * mm});
            skLineSegment(sketch, "E208.4.5.2", {"start": v(-34.95, 21.44) * mm, "end": v(-32.95, 21.44) * mm});
            skLineSegment(sketch, "E208.4.5.3", {"start": v(-32.95, 23.44) * mm, "end": v(-32.95, 21.44) * mm});
            skLineSegment(sketch, "E208.4.6.0", {"start": v(-34.95, 19.44) * mm, "end": v(-32.95, 19.44) * mm});
            skLineSegment(sketch, "E208.4.6.1", {"start": v(-34.95, 19.44) * mm, "end": v(-34.95, 17.44) * mm});
            skLineSegment(sketch, "E208.4.6.2", {"start": v(-34.95, 17.44) * mm, "end": v(-32.95, 17.44) * mm});
            skLineSegment(sketch, "E208.4.6.3", {"start": v(-32.95, 19.44) * mm, "end": v(-32.95, 17.44) * mm});
            skLineSegment(sketch, "E208.4.7.0", {"start": v(-34.95, 15.44) * mm, "end": v(-32.95, 15.44) * mm});
            skLineSegment(sketch, "E208.4.7.1", {"start": v(-34.95, 15.44) * mm, "end": v(-34.95, 13.44) * mm});
            skLineSegment(sketch, "E208.4.7.2", {"start": v(-34.95, 13.44) * mm, "end": v(-32.95, 13.44) * mm});
            skLineSegment(sketch, "E208.4.7.3", {"start": v(-32.95, 15.44) * mm, "end": v(-32.95, 13.44) * mm});
            skLineSegment(sketch, "E208.4.8.0", {"start": v(-34.95, 11.44) * mm, "end": v(-32.95, 11.44) * mm});
            skLineSegment(sketch, "E208.4.8.1", {"start": v(-34.95, 11.44) * mm, "end": v(-34.95, 9.44) * mm});
            skLineSegment(sketch, "E208.4.8.2", {"start": v(-34.95, 9.44) * mm, "end": v(-32.95, 9.44) * mm});
            skLineSegment(sketch, "E208.4.8.3", {"start": v(-32.95, 11.44) * mm, "end": v(-32.95, 9.44) * mm});
            skLineSegment(sketch, "E208.4.9.0", {"start": v(-34.95, 7.44) * mm, "end": v(-32.95, 7.44) * mm});
            skLineSegment(sketch, "E208.4.9.1", {"start": v(-34.95, 7.44) * mm, "end": v(-34.95, 5.44) * mm});
            skLineSegment(sketch, "E208.4.9.2", {"start": v(-34.95, 5.44) * mm, "end": v(-32.95, 5.44) * mm});
            skLineSegment(sketch, "E208.4.9.3", {"start": v(-32.95, 7.44) * mm, "end": v(-32.95, 5.44) * mm});
            skLineSegment(sketch, "E208.4.10.0", {"start": v(-34.95, 3.44) * mm, "end": v(-32.95, 3.44) * mm});
            skLineSegment(sketch, "E208.4.10.1", {"start": v(-34.95, 3.44) * mm, "end": v(-34.95, 1.44) * mm});
            skLineSegment(sketch, "E208.4.10.2", {"start": v(-34.95, 1.44) * mm, "end": v(-32.95, 1.44) * mm});
            skLineSegment(sketch, "E208.4.10.3", {"start": v(-32.95, 3.44) * mm, "end": v(-32.95, 1.44) * mm});
            skLineSegment(sketch, "E208.4.11.0", {"start": v(-34.95, -0.56) * mm, "end": v(-32.95, -0.56) * mm});
            skLineSegment(sketch, "E208.4.11.1", {"start": v(-34.95, -0.56) * mm, "end": v(-34.95, -2.56) * mm});
            skLineSegment(sketch, "E208.4.11.2", {"start": v(-34.95, -2.56) * mm, "end": v(-32.95, -2.56) * mm});
            skLineSegment(sketch, "E208.4.11.3", {"start": v(-32.95, -0.56) * mm, "end": v(-32.95, -2.56) * mm});
            skLineSegment(sketch, "E208.4.12.0", {"start": v(-34.95, -4.56) * mm, "end": v(-32.95, -4.56) * mm});
            skLineSegment(sketch, "E208.4.12.1", {"start": v(-34.95, -4.56) * mm, "end": v(-34.95, -6.56) * mm});
            skLineSegment(sketch, "E208.4.12.2", {"start": v(-34.95, -6.56) * mm, "end": v(-32.95, -6.56) * mm});
            skLineSegment(sketch, "E208.4.12.3", {"start": v(-32.95, -4.56) * mm, "end": v(-32.95, -6.56) * mm});
            skLineSegment(sketch, "E208.4.13.0", {"start": v(-34.95, -8.56) * mm, "end": v(-32.95, -8.56) * mm});
            skLineSegment(sketch, "E208.4.13.1", {"start": v(-34.95, -8.56) * mm, "end": v(-34.95, -10.56) * mm});
            skLineSegment(sketch, "E208.4.13.2", {"start": v(-34.95, -10.56) * mm, "end": v(-32.95, -10.56) * mm});
            skLineSegment(sketch, "E208.4.13.3", {"start": v(-32.95, -8.56) * mm, "end": v(-32.95, -10.56) * mm});
            skLineSegment(sketch, "E208.4.14.0", {"start": v(-34.95, -12.56) * mm, "end": v(-32.95, -12.56) * mm});
            skLineSegment(sketch, "E208.4.14.1", {"start": v(-34.95, -12.56) * mm, "end": v(-34.95, -14.56) * mm});
            skLineSegment(sketch, "E208.4.14.2", {"start": v(-34.95, -14.56) * mm, "end": v(-32.95, -14.56) * mm});
            skLineSegment(sketch, "E208.4.14.3", {"start": v(-32.95, -12.56) * mm, "end": v(-32.95, -14.56) * mm});
            skLineSegment(sketch, "E208.4.15.0", {"start": v(-34.95, -16.56) * mm, "end": v(-32.95, -16.56) * mm});
            skLineSegment(sketch, "E208.4.15.1", {"start": v(-34.95, -16.56) * mm, "end": v(-34.95, -18.56) * mm});
            skLineSegment(sketch, "E208.4.15.2", {"start": v(-34.95, -18.56) * mm, "end": v(-32.95, -18.56) * mm});
            skLineSegment(sketch, "E208.4.15.3", {"start": v(-32.95, -16.56) * mm, "end": v(-32.95, -18.56) * mm});
            skLineSegment(sketch, "E208.4.16.0", {"start": v(-34.95, -20.56) * mm, "end": v(-32.95, -20.56) * mm});
            skLineSegment(sketch, "E208.4.16.1", {"start": v(-34.95, -20.56) * mm, "end": v(-34.95, -22.56) * mm});
            skLineSegment(sketch, "E208.4.16.2", {"start": v(-34.95, -22.56) * mm, "end": v(-32.95, -22.56) * mm});
            skLineSegment(sketch, "E208.4.16.3", {"start": v(-32.95, -20.56) * mm, "end": v(-32.95, -22.56) * mm});
            skLineSegment(sketch, "E208.4.17.0", {"start": v(-34.95, -24.56) * mm, "end": v(-32.95, -24.56) * mm});
            skLineSegment(sketch, "E208.4.17.1", {"start": v(-34.95, -24.56) * mm, "end": v(-34.95, -26.56) * mm});
            skLineSegment(sketch, "E208.4.17.2", {"start": v(-34.95, -26.56) * mm, "end": v(-32.95, -26.56) * mm});
            skLineSegment(sketch, "E208.4.17.3", {"start": v(-32.95, -24.56) * mm, "end": v(-32.95, -26.56) * mm});
            skLineSegment(sketch, "E208.4.18.0", {"start": v(-34.95, -28.56) * mm, "end": v(-32.95, -28.56) * mm});
            skLineSegment(sketch, "E208.4.18.1", {"start": v(-34.95, -28.56) * mm, "end": v(-34.95, -30.56) * mm});
            skLineSegment(sketch, "E208.4.18.2", {"start": v(-34.95, -30.56) * mm, "end": v(-32.95, -30.56) * mm});
            skLineSegment(sketch, "E208.4.18.3", {"start": v(-32.95, -28.56) * mm, "end": v(-32.95, -30.56) * mm});
            skLineSegment(sketch, "E208.4.19.0", {"start": v(-34.95, -32.56) * mm, "end": v(-32.95, -32.56) * mm});
            skLineSegment(sketch, "E208.4.19.1", {"start": v(-34.95, -32.56) * mm, "end": v(-34.95, -34.56) * mm});
            skLineSegment(sketch, "E208.4.19.2", {"start": v(-34.95, -34.56) * mm, "end": v(-32.95, -34.56) * mm});
            skLineSegment(sketch, "E208.4.19.3", {"start": v(-32.95, -32.56) * mm, "end": v(-32.95, -34.56) * mm});
            skLineSegment(sketch, "E208.4.20.0", {"start": v(-34.95, -36.56) * mm, "end": v(-32.95, -36.56) * mm});
            skLineSegment(sketch, "E208.4.20.1", {"start": v(-34.95, -36.56) * mm, "end": v(-34.95, -38.56) * mm});
            skLineSegment(sketch, "E208.4.20.2", {"start": v(-34.95, -38.56) * mm, "end": v(-32.95, -38.56) * mm});
            skLineSegment(sketch, "E208.4.20.3", {"start": v(-32.95, -36.56) * mm, "end": v(-32.95, -38.56) * mm});
            skLineSegment(sketch, "E208.4.21.0", {"start": v(-34.95, -40.56) * mm, "end": v(-32.95, -40.56) * mm});
            skLineSegment(sketch, "E208.4.21.1", {"start": v(-34.95, -40.56) * mm, "end": v(-34.95, -42.56) * mm});
            skLineSegment(sketch, "E208.4.21.2", {"start": v(-34.95, -42.56) * mm, "end": v(-32.95, -42.56) * mm});
            skLineSegment(sketch, "E208.4.21.3", {"start": v(-32.95, -40.56) * mm, "end": v(-32.95, -42.56) * mm});
            skLineSegment(sketch, "E208.5.0.0", {"start": v(-30.95, 43.44) * mm, "end": v(-28.95, 43.44) * mm});
            skLineSegment(sketch, "E208.5.0.1", {"start": v(-30.95, 43.44) * mm, "end": v(-30.95, 41.44) * mm});
            skLineSegment(sketch, "E208.5.0.2", {"start": v(-30.95, 41.44) * mm, "end": v(-28.95, 41.44) * mm});
            skLineSegment(sketch, "E208.5.0.3", {"start": v(-28.95, 43.44) * mm, "end": v(-28.95, 41.44) * mm});
            skLineSegment(sketch, "E208.5.1.0", {"start": v(-30.95, 39.44) * mm, "end": v(-28.95, 39.44) * mm});
            skLineSegment(sketch, "E208.5.1.1", {"start": v(-30.95, 39.44) * mm, "end": v(-30.95, 37.44) * mm});
            skLineSegment(sketch, "E208.5.1.2", {"start": v(-30.95, 37.44) * mm, "end": v(-28.95, 37.44) * mm});
            skLineSegment(sketch, "E208.5.1.3", {"start": v(-28.95, 39.44) * mm, "end": v(-28.95, 37.44) * mm});
            skLineSegment(sketch, "E208.5.2.0", {"start": v(-30.95, 35.44) * mm, "end": v(-28.95, 35.44) * mm});
            skLineSegment(sketch, "E208.5.2.1", {"start": v(-30.95, 35.44) * mm, "end": v(-30.95, 33.44) * mm});
            skLineSegment(sketch, "E208.5.2.2", {"start": v(-30.95, 33.44) * mm, "end": v(-28.95, 33.44) * mm});
            skLineSegment(sketch, "E208.5.2.3", {"start": v(-28.95, 35.44) * mm, "end": v(-28.95, 33.44) * mm});
            skLineSegment(sketch, "E208.5.3.0", {"start": v(-30.95, 31.44) * mm, "end": v(-28.95, 31.44) * mm});
            skLineSegment(sketch, "E208.5.3.1", {"start": v(-30.95, 31.44) * mm, "end": v(-30.95, 29.44) * mm});
            skLineSegment(sketch, "E208.5.3.2", {"start": v(-30.95, 29.44) * mm, "end": v(-28.95, 29.44) * mm});
            skLineSegment(sketch, "E208.5.3.3", {"start": v(-28.95, 31.44) * mm, "end": v(-28.95, 29.44) * mm});
            skLineSegment(sketch, "E208.5.4.0", {"start": v(-30.95, 27.44) * mm, "end": v(-28.95, 27.44) * mm});
            skLineSegment(sketch, "E208.5.4.1", {"start": v(-30.95, 27.44) * mm, "end": v(-30.95, 25.44) * mm});
            skLineSegment(sketch, "E208.5.4.2", {"start": v(-30.95, 25.44) * mm, "end": v(-28.95, 25.44) * mm});
            skLineSegment(sketch, "E208.5.4.3", {"start": v(-28.95, 27.44) * mm, "end": v(-28.95, 25.44) * mm});
            skLineSegment(sketch, "E208.5.5.0", {"start": v(-30.95, 23.44) * mm, "end": v(-28.95, 23.44) * mm});
            skLineSegment(sketch, "E208.5.5.1", {"start": v(-30.95, 23.44) * mm, "end": v(-30.95, 21.44) * mm});
            skLineSegment(sketch, "E208.5.5.2", {"start": v(-30.95, 21.44) * mm, "end": v(-28.95, 21.44) * mm});
            skLineSegment(sketch, "E208.5.5.3", {"start": v(-28.95, 23.44) * mm, "end": v(-28.95, 21.44) * mm});
            skLineSegment(sketch, "E208.5.6.0", {"start": v(-30.95, 19.44) * mm, "end": v(-28.95, 19.44) * mm});
            skLineSegment(sketch, "E208.5.6.1", {"start": v(-30.95, 19.44) * mm, "end": v(-30.95, 17.44) * mm});
            skLineSegment(sketch, "E208.5.6.2", {"start": v(-30.95, 17.44) * mm, "end": v(-28.95, 17.44) * mm});
            skLineSegment(sketch, "E208.5.6.3", {"start": v(-28.95, 19.44) * mm, "end": v(-28.95, 17.44) * mm});
            skLineSegment(sketch, "E208.5.7.0", {"start": v(-30.95, 15.44) * mm, "end": v(-28.95, 15.44) * mm});
            skLineSegment(sketch, "E208.5.7.1", {"start": v(-30.95, 15.44) * mm, "end": v(-30.95, 13.44) * mm});
            skLineSegment(sketch, "E208.5.7.2", {"start": v(-30.95, 13.44) * mm, "end": v(-28.95, 13.44) * mm});
            skLineSegment(sketch, "E208.5.7.3", {"start": v(-28.95, 15.44) * mm, "end": v(-28.95, 13.44) * mm});
            skLineSegment(sketch, "E208.5.8.0", {"start": v(-30.95, 11.44) * mm, "end": v(-28.95, 11.44) * mm});
            skLineSegment(sketch, "E208.5.8.1", {"start": v(-30.95, 11.44) * mm, "end": v(-30.95, 9.44) * mm});
            skLineSegment(sketch, "E208.5.8.2", {"start": v(-30.95, 9.44) * mm, "end": v(-28.95, 9.44) * mm});
            skLineSegment(sketch, "E208.5.8.3", {"start": v(-28.95, 11.44) * mm, "end": v(-28.95, 9.44) * mm});
            skLineSegment(sketch, "E208.5.9.0", {"start": v(-30.95, 7.44) * mm, "end": v(-28.95, 7.44) * mm});
            skLineSegment(sketch, "E208.5.9.1", {"start": v(-30.95, 7.44) * mm, "end": v(-30.95, 5.44) * mm});
            skLineSegment(sketch, "E208.5.9.2", {"start": v(-30.95, 5.44) * mm, "end": v(-28.95, 5.44) * mm});
            skLineSegment(sketch, "E208.5.9.3", {"start": v(-28.95, 7.44) * mm, "end": v(-28.95, 5.44) * mm});
            skLineSegment(sketch, "E208.5.10.0", {"start": v(-30.95, 3.44) * mm, "end": v(-28.95, 3.44) * mm});
            skLineSegment(sketch, "E208.5.10.1", {"start": v(-30.95, 3.44) * mm, "end": v(-30.95, 1.44) * mm});
            skLineSegment(sketch, "E208.5.10.2", {"start": v(-30.95, 1.44) * mm, "end": v(-28.95, 1.44) * mm});
            skLineSegment(sketch, "E208.5.10.3", {"start": v(-28.95, 3.44) * mm, "end": v(-28.95, 1.44) * mm});
            skLineSegment(sketch, "E208.5.11.0", {"start": v(-30.95, -0.56) * mm, "end": v(-28.95, -0.56) * mm});
            skLineSegment(sketch, "E208.5.11.1", {"start": v(-30.95, -0.56) * mm, "end": v(-30.95, -2.56) * mm});
            skLineSegment(sketch, "E208.5.11.2", {"start": v(-30.95, -2.56) * mm, "end": v(-28.95, -2.56) * mm});
            skLineSegment(sketch, "E208.5.11.3", {"start": v(-28.95, -0.56) * mm, "end": v(-28.95, -2.56) * mm});
            skLineSegment(sketch, "E208.5.12.0", {"start": v(-30.95, -4.56) * mm, "end": v(-28.95, -4.56) * mm});
            skLineSegment(sketch, "E208.5.12.1", {"start": v(-30.95, -4.56) * mm, "end": v(-30.95, -6.56) * mm});
            skLineSegment(sketch, "E208.5.12.2", {"start": v(-30.95, -6.56) * mm, "end": v(-28.95, -6.56) * mm});
            skLineSegment(sketch, "E208.5.12.3", {"start": v(-28.95, -4.56) * mm, "end": v(-28.95, -6.56) * mm});
            skLineSegment(sketch, "E208.5.13.0", {"start": v(-30.95, -8.56) * mm, "end": v(-28.95, -8.56) * mm});
            skLineSegment(sketch, "E208.5.13.1", {"start": v(-30.95, -8.56) * mm, "end": v(-30.95, -10.56) * mm});
            skLineSegment(sketch, "E208.5.13.2", {"start": v(-30.95, -10.56) * mm, "end": v(-28.95, -10.56) * mm});
            skLineSegment(sketch, "E208.5.13.3", {"start": v(-28.95, -8.56) * mm, "end": v(-28.95, -10.56) * mm});
            skLineSegment(sketch, "E208.5.14.0", {"start": v(-30.95, -12.56) * mm, "end": v(-28.95, -12.56) * mm});
            skLineSegment(sketch, "E208.5.14.1", {"start": v(-30.95, -12.56) * mm, "end": v(-30.95, -14.56) * mm});
            skLineSegment(sketch, "E208.5.14.2", {"start": v(-30.95, -14.56) * mm, "end": v(-28.95, -14.56) * mm});
            skLineSegment(sketch, "E208.5.14.3", {"start": v(-28.95, -12.56) * mm, "end": v(-28.95, -14.56) * mm});
            skLineSegment(sketch, "E208.5.15.0", {"start": v(-30.95, -16.56) * mm, "end": v(-28.95, -16.56) * mm});
            skLineSegment(sketch, "E208.5.15.1", {"start": v(-30.95, -16.56) * mm, "end": v(-30.95, -18.56) * mm});
            skLineSegment(sketch, "E208.5.15.2", {"start": v(-30.95, -18.56) * mm, "end": v(-28.95, -18.56) * mm});
            skLineSegment(sketch, "E208.5.15.3", {"start": v(-28.95, -16.56) * mm, "end": v(-28.95, -18.56) * mm});
            skLineSegment(sketch, "E208.5.16.0", {"start": v(-30.95, -20.56) * mm, "end": v(-28.95, -20.56) * mm});
            skLineSegment(sketch, "E208.5.16.1", {"start": v(-30.95, -20.56) * mm, "end": v(-30.95, -22.56) * mm});
            skLineSegment(sketch, "E208.5.16.2", {"start": v(-30.95, -22.56) * mm, "end": v(-28.95, -22.56) * mm});
            skLineSegment(sketch, "E208.5.16.3", {"start": v(-28.95, -20.56) * mm, "end": v(-28.95, -22.56) * mm});
            skLineSegment(sketch, "E208.5.17.0", {"start": v(-30.95, -24.56) * mm, "end": v(-28.95, -24.56) * mm});
            skLineSegment(sketch, "E208.5.17.1", {"start": v(-30.95, -24.56) * mm, "end": v(-30.95, -26.56) * mm});
            skLineSegment(sketch, "E208.5.17.2", {"start": v(-30.95, -26.56) * mm, "end": v(-28.95, -26.56) * mm});
            skLineSegment(sketch, "E208.5.17.3", {"start": v(-28.95, -24.56) * mm, "end": v(-28.95, -26.56) * mm});
            skLineSegment(sketch, "E208.5.18.0", {"start": v(-30.95, -28.56) * mm, "end": v(-28.95, -28.56) * mm});
            skLineSegment(sketch, "E208.5.18.1", {"start": v(-30.95, -28.56) * mm, "end": v(-30.95, -30.56) * mm});
            skLineSegment(sketch, "E208.5.18.2", {"start": v(-30.95, -30.56) * mm, "end": v(-28.95, -30.56) * mm});
            skLineSegment(sketch, "E208.5.18.3", {"start": v(-28.95, -28.56) * mm, "end": v(-28.95, -30.56) * mm});
            skLineSegment(sketch, "E208.5.19.0", {"start": v(-30.95, -32.56) * mm, "end": v(-28.95, -32.56) * mm});
            skLineSegment(sketch, "E208.5.19.1", {"start": v(-30.95, -32.56) * mm, "end": v(-30.95, -34.56) * mm});
            skLineSegment(sketch, "E208.5.19.2", {"start": v(-30.95, -34.56) * mm, "end": v(-28.95, -34.56) * mm});
            skLineSegment(sketch, "E208.5.19.3", {"start": v(-28.95, -32.56) * mm, "end": v(-28.95, -34.56) * mm});
            skLineSegment(sketch, "E208.5.20.0", {"start": v(-30.95, -36.56) * mm, "end": v(-28.95, -36.56) * mm});
            skLineSegment(sketch, "E208.5.20.1", {"start": v(-30.95, -36.56) * mm, "end": v(-30.95, -38.56) * mm});
            skLineSegment(sketch, "E208.5.20.2", {"start": v(-30.95, -38.56) * mm, "end": v(-28.95, -38.56) * mm});
            skLineSegment(sketch, "E208.5.20.3", {"start": v(-28.95, -36.56) * mm, "end": v(-28.95, -38.56) * mm});
            skLineSegment(sketch, "E208.5.21.0", {"start": v(-30.95, -40.56) * mm, "end": v(-28.95, -40.56) * mm});
            skLineSegment(sketch, "E208.5.21.1", {"start": v(-30.95, -40.56) * mm, "end": v(-30.95, -42.56) * mm});
            skLineSegment(sketch, "E208.5.21.2", {"start": v(-30.95, -42.56) * mm, "end": v(-28.95, -42.56) * mm});
            skLineSegment(sketch, "E208.5.21.3", {"start": v(-28.95, -40.56) * mm, "end": v(-28.95, -42.56) * mm});
            skLineSegment(sketch, "E208.6.0.0", {"start": v(-26.95, 43.44) * mm, "end": v(-24.95, 43.44) * mm});
            skLineSegment(sketch, "E208.6.0.1", {"start": v(-26.95, 43.44) * mm, "end": v(-26.95, 41.44) * mm});
            skLineSegment(sketch, "E208.6.0.2", {"start": v(-26.95, 41.44) * mm, "end": v(-24.95, 41.44) * mm});
            skLineSegment(sketch, "E208.6.0.3", {"start": v(-24.95, 43.44) * mm, "end": v(-24.95, 41.44) * mm});
            skLineSegment(sketch, "E208.6.1.0", {"start": v(-26.95, 39.44) * mm, "end": v(-24.95, 39.44) * mm});
            skLineSegment(sketch, "E208.6.1.1", {"start": v(-26.95, 39.44) * mm, "end": v(-26.95, 37.44) * mm});
            skLineSegment(sketch, "E208.6.1.2", {"start": v(-26.95, 37.44) * mm, "end": v(-24.95, 37.44) * mm});
            skLineSegment(sketch, "E208.6.1.3", {"start": v(-24.95, 39.44) * mm, "end": v(-24.95, 37.44) * mm});
            skLineSegment(sketch, "E208.6.2.0", {"start": v(-26.95, 35.44) * mm, "end": v(-24.95, 35.44) * mm});
            skLineSegment(sketch, "E208.6.2.1", {"start": v(-26.95, 35.44) * mm, "end": v(-26.95, 33.44) * mm});
            skLineSegment(sketch, "E208.6.2.2", {"start": v(-26.95, 33.44) * mm, "end": v(-24.95, 33.44) * mm});
            skLineSegment(sketch, "E208.6.2.3", {"start": v(-24.95, 35.44) * mm, "end": v(-24.95, 33.44) * mm});
            skLineSegment(sketch, "E208.6.3.0", {"start": v(-26.95, 31.44) * mm, "end": v(-24.95, 31.44) * mm});
            skLineSegment(sketch, "E208.6.3.1", {"start": v(-26.95, 31.44) * mm, "end": v(-26.95, 29.44) * mm});
            skLineSegment(sketch, "E208.6.3.2", {"start": v(-26.95, 29.44) * mm, "end": v(-24.95, 29.44) * mm});
            skLineSegment(sketch, "E208.6.3.3", {"start": v(-24.95, 31.44) * mm, "end": v(-24.95, 29.44) * mm});
            skLineSegment(sketch, "E208.6.4.0", {"start": v(-26.95, 27.44) * mm, "end": v(-24.95, 27.44) * mm});
            skLineSegment(sketch, "E208.6.4.1", {"start": v(-26.95, 27.44) * mm, "end": v(-26.95, 25.44) * mm});
            skLineSegment(sketch, "E208.6.4.2", {"start": v(-26.95, 25.44) * mm, "end": v(-24.95, 25.44) * mm});
            skLineSegment(sketch, "E208.6.4.3", {"start": v(-24.95, 27.44) * mm, "end": v(-24.95, 25.44) * mm});
            skLineSegment(sketch, "E208.6.5.0", {"start": v(-26.95, 23.44) * mm, "end": v(-24.95, 23.44) * mm});
            skLineSegment(sketch, "E208.6.5.1", {"start": v(-26.95, 23.44) * mm, "end": v(-26.95, 21.44) * mm});
            skLineSegment(sketch, "E208.6.5.2", {"start": v(-26.95, 21.44) * mm, "end": v(-24.95, 21.44) * mm});
            skLineSegment(sketch, "E208.6.5.3", {"start": v(-24.95, 23.44) * mm, "end": v(-24.95, 21.44) * mm});
            skLineSegment(sketch, "E208.6.6.0", {"start": v(-26.95, 19.44) * mm, "end": v(-24.95, 19.44) * mm});
            skLineSegment(sketch, "E208.6.6.1", {"start": v(-26.95, 19.44) * mm, "end": v(-26.95, 17.44) * mm});
            skLineSegment(sketch, "E208.6.6.2", {"start": v(-26.95, 17.44) * mm, "end": v(-24.95, 17.44) * mm});
            skLineSegment(sketch, "E208.6.6.3", {"start": v(-24.95, 19.44) * mm, "end": v(-24.95, 17.44) * mm});
            skLineSegment(sketch, "E208.6.7.0", {"start": v(-26.95, 15.44) * mm, "end": v(-24.95, 15.44) * mm});
            skLineSegment(sketch, "E208.6.7.1", {"start": v(-26.95, 15.44) * mm, "end": v(-26.95, 13.44) * mm});
            skLineSegment(sketch, "E208.6.7.2", {"start": v(-26.95, 13.44) * mm, "end": v(-24.95, 13.44) * mm});
            skLineSegment(sketch, "E208.6.7.3", {"start": v(-24.95, 15.44) * mm, "end": v(-24.95, 13.44) * mm});
            skLineSegment(sketch, "E208.6.8.0", {"start": v(-26.95, 11.44) * mm, "end": v(-24.95, 11.44) * mm});
            skLineSegment(sketch, "E208.6.8.1", {"start": v(-26.95, 11.44) * mm, "end": v(-26.95, 9.44) * mm});
            skLineSegment(sketch, "E208.6.8.2", {"start": v(-26.95, 9.44) * mm, "end": v(-24.95, 9.44) * mm});
            skLineSegment(sketch, "E208.6.8.3", {"start": v(-24.95, 11.44) * mm, "end": v(-24.95, 9.44) * mm});
            skLineSegment(sketch, "E208.6.9.0", {"start": v(-26.95, 7.44) * mm, "end": v(-24.95, 7.44) * mm});
            skLineSegment(sketch, "E208.6.9.1", {"start": v(-26.95, 7.44) * mm, "end": v(-26.95, 5.44) * mm});
            skLineSegment(sketch, "E208.6.9.2", {"start": v(-26.95, 5.44) * mm, "end": v(-24.95, 5.44) * mm});
            skLineSegment(sketch, "E208.6.9.3", {"start": v(-24.95, 7.44) * mm, "end": v(-24.95, 5.44) * mm});
            skLineSegment(sketch, "E208.6.10.0", {"start": v(-26.95, 3.44) * mm, "end": v(-24.95, 3.44) * mm});
            skLineSegment(sketch, "E208.6.10.1", {"start": v(-26.95, 3.44) * mm, "end": v(-26.95, 1.44) * mm});
            skLineSegment(sketch, "E208.6.10.2", {"start": v(-26.95, 1.44) * mm, "end": v(-24.95, 1.44) * mm});
            skLineSegment(sketch, "E208.6.10.3", {"start": v(-24.95, 3.44) * mm, "end": v(-24.95, 1.44) * mm});
            skLineSegment(sketch, "E208.6.11.0", {"start": v(-26.95, -0.56) * mm, "end": v(-24.95, -0.56) * mm});
            skLineSegment(sketch, "E208.6.11.1", {"start": v(-26.95, -0.56) * mm, "end": v(-26.95, -2.56) * mm});
            skLineSegment(sketch, "E208.6.11.2", {"start": v(-26.95, -2.56) * mm, "end": v(-24.95, -2.56) * mm});
            skLineSegment(sketch, "E208.6.11.3", {"start": v(-24.95, -0.56) * mm, "end": v(-24.95, -2.56) * mm});
            skLineSegment(sketch, "E208.6.12.0", {"start": v(-26.95, -4.56) * mm, "end": v(-24.95, -4.56) * mm});
            skLineSegment(sketch, "E208.6.12.1", {"start": v(-26.95, -4.56) * mm, "end": v(-26.95, -6.56) * mm});
            skLineSegment(sketch, "E208.6.12.2", {"start": v(-26.95, -6.56) * mm, "end": v(-24.95, -6.56) * mm});
            skLineSegment(sketch, "E208.6.12.3", {"start": v(-24.95, -4.56) * mm, "end": v(-24.95, -6.56) * mm});
            skLineSegment(sketch, "E208.6.13.0", {"start": v(-26.95, -8.56) * mm, "end": v(-24.95, -8.56) * mm});
            skLineSegment(sketch, "E208.6.13.1", {"start": v(-26.95, -8.56) * mm, "end": v(-26.95, -10.56) * mm});
            skLineSegment(sketch, "E208.6.13.2", {"start": v(-26.95, -10.56) * mm, "end": v(-24.95, -10.56) * mm});
            skLineSegment(sketch, "E208.6.13.3", {"start": v(-24.95, -8.56) * mm, "end": v(-24.95, -10.56) * mm});
            skLineSegment(sketch, "E208.6.14.0", {"start": v(-26.95, -12.56) * mm, "end": v(-24.95, -12.56) * mm});
            skLineSegment(sketch, "E208.6.14.1", {"start": v(-26.95, -12.56) * mm, "end": v(-26.95, -14.56) * mm});
            skLineSegment(sketch, "E208.6.14.2", {"start": v(-26.95, -14.56) * mm, "end": v(-24.95, -14.56) * mm});
            skLineSegment(sketch, "E208.6.14.3", {"start": v(-24.95, -12.56) * mm, "end": v(-24.95, -14.56) * mm});
            skLineSegment(sketch, "E208.6.15.0", {"start": v(-26.95, -16.56) * mm, "end": v(-24.95, -16.56) * mm});
            skLineSegment(sketch, "E208.6.15.1", {"start": v(-26.95, -16.56) * mm, "end": v(-26.95, -18.56) * mm});
            skLineSegment(sketch, "E208.6.15.2", {"start": v(-26.95, -18.56) * mm, "end": v(-24.95, -18.56) * mm});
            skLineSegment(sketch, "E208.6.15.3", {"start": v(-24.95, -16.56) * mm, "end": v(-24.95, -18.56) * mm});
            skLineSegment(sketch, "E208.6.16.0", {"start": v(-26.95, -20.56) * mm, "end": v(-24.95, -20.56) * mm});
            skLineSegment(sketch, "E208.6.16.1", {"start": v(-26.95, -20.56) * mm, "end": v(-26.95, -22.56) * mm});
            skLineSegment(sketch, "E208.6.16.2", {"start": v(-26.95, -22.56) * mm, "end": v(-24.95, -22.56) * mm});
            skLineSegment(sketch, "E208.6.16.3", {"start": v(-24.95, -20.56) * mm, "end": v(-24.95, -22.56) * mm});
            skLineSegment(sketch, "E208.6.17.0", {"start": v(-26.95, -24.56) * mm, "end": v(-24.95, -24.56) * mm});
            skLineSegment(sketch, "E208.6.17.1", {"start": v(-26.95, -24.56) * mm, "end": v(-26.95, -26.56) * mm});
            skLineSegment(sketch, "E208.6.17.2", {"start": v(-26.95, -26.56) * mm, "end": v(-24.95, -26.56) * mm});
            skLineSegment(sketch, "E208.6.17.3", {"start": v(-24.95, -24.56) * mm, "end": v(-24.95, -26.56) * mm});
            skLineSegment(sketch, "E208.6.18.0", {"start": v(-26.95, -28.56) * mm, "end": v(-24.95, -28.56) * mm});
            skLineSegment(sketch, "E208.6.18.1", {"start": v(-26.95, -28.56) * mm, "end": v(-26.95, -30.56) * mm});
            skLineSegment(sketch, "E208.6.18.2", {"start": v(-26.95, -30.56) * mm, "end": v(-24.95, -30.56) * mm});
            skLineSegment(sketch, "E208.6.18.3", {"start": v(-24.95, -28.56) * mm, "end": v(-24.95, -30.56) * mm});
            skLineSegment(sketch, "E208.6.19.0", {"start": v(-26.95, -32.56) * mm, "end": v(-24.95, -32.56) * mm});
            skLineSegment(sketch, "E208.6.19.1", {"start": v(-26.95, -32.56) * mm, "end": v(-26.95, -34.56) * mm});
            skLineSegment(sketch, "E208.6.19.2", {"start": v(-26.95, -34.56) * mm, "end": v(-24.95, -34.56) * mm});
            skLineSegment(sketch, "E208.6.19.3", {"start": v(-24.95, -32.56) * mm, "end": v(-24.95, -34.56) * mm});
            skLineSegment(sketch, "E208.6.20.0", {"start": v(-26.95, -36.56) * mm, "end": v(-24.95, -36.56) * mm});
            skLineSegment(sketch, "E208.6.20.1", {"start": v(-26.95, -36.56) * mm, "end": v(-26.95, -38.56) * mm});
            skLineSegment(sketch, "E208.6.20.2", {"start": v(-26.95, -38.56) * mm, "end": v(-24.95, -38.56) * mm});
            skLineSegment(sketch, "E208.6.20.3", {"start": v(-24.95, -36.56) * mm, "end": v(-24.95, -38.56) * mm});
            skLineSegment(sketch, "E208.6.21.0", {"start": v(-26.95, -40.56) * mm, "end": v(-24.95, -40.56) * mm});
            skLineSegment(sketch, "E208.6.21.1", {"start": v(-26.95, -40.56) * mm, "end": v(-26.95, -42.56) * mm});
            skLineSegment(sketch, "E208.6.21.2", {"start": v(-26.95, -42.56) * mm, "end": v(-24.95, -42.56) * mm});
            skLineSegment(sketch, "E208.6.21.3", {"start": v(-24.95, -40.56) * mm, "end": v(-24.95, -42.56) * mm});
            skLineSegment(sketch, "E208.7.0.0", {"start": v(-22.95, 43.44) * mm, "end": v(-20.95, 43.44) * mm});
            skLineSegment(sketch, "E208.7.0.1", {"start": v(-22.95, 43.44) * mm, "end": v(-22.95, 41.44) * mm});
            skLineSegment(sketch, "E208.7.0.2", {"start": v(-22.95, 41.44) * mm, "end": v(-20.95, 41.44) * mm});
            skLineSegment(sketch, "E208.7.0.3", {"start": v(-20.95, 43.44) * mm, "end": v(-20.95, 41.44) * mm});
            skLineSegment(sketch, "E208.7.1.0", {"start": v(-22.95, 39.44) * mm, "end": v(-20.95, 39.44) * mm});
            skLineSegment(sketch, "E208.7.1.1", {"start": v(-22.95, 39.44) * mm, "end": v(-22.95, 37.44) * mm});
            skLineSegment(sketch, "E208.7.1.2", {"start": v(-22.95, 37.44) * mm, "end": v(-20.95, 37.44) * mm});
            skLineSegment(sketch, "E208.7.1.3", {"start": v(-20.95, 39.44) * mm, "end": v(-20.95, 37.44) * mm});
            skLineSegment(sketch, "E208.7.2.0", {"start": v(-22.95, 35.44) * mm, "end": v(-20.95, 35.44) * mm});
            skLineSegment(sketch, "E208.7.2.1", {"start": v(-22.95, 35.44) * mm, "end": v(-22.95, 33.44) * mm});
            skLineSegment(sketch, "E208.7.2.2", {"start": v(-22.95, 33.44) * mm, "end": v(-20.95, 33.44) * mm});
            skLineSegment(sketch, "E208.7.2.3", {"start": v(-20.95, 35.44) * mm, "end": v(-20.95, 33.44) * mm});
            skLineSegment(sketch, "E208.7.3.0", {"start": v(-22.95, 31.44) * mm, "end": v(-20.95, 31.44) * mm});
            skLineSegment(sketch, "E208.7.3.1", {"start": v(-22.95, 31.44) * mm, "end": v(-22.95, 29.44) * mm});
            skLineSegment(sketch, "E208.7.3.2", {"start": v(-22.95, 29.44) * mm, "end": v(-20.95, 29.44) * mm});
            skLineSegment(sketch, "E208.7.3.3", {"start": v(-20.95, 31.44) * mm, "end": v(-20.95, 29.44) * mm});
            skLineSegment(sketch, "E208.7.4.0", {"start": v(-22.95, 27.44) * mm, "end": v(-20.95, 27.44) * mm});
            skLineSegment(sketch, "E208.7.4.1", {"start": v(-22.95, 27.44) * mm, "end": v(-22.95, 25.44) * mm});
            skLineSegment(sketch, "E208.7.4.2", {"start": v(-22.95, 25.44) * mm, "end": v(-20.95, 25.44) * mm});
            skLineSegment(sketch, "E208.7.4.3", {"start": v(-20.95, 27.44) * mm, "end": v(-20.95, 25.44) * mm});
            skLineSegment(sketch, "E208.7.5.0", {"start": v(-22.95, 23.44) * mm, "end": v(-20.95, 23.44) * mm});
            skLineSegment(sketch, "E208.7.5.1", {"start": v(-22.95, 23.44) * mm, "end": v(-22.95, 21.44) * mm});
            skLineSegment(sketch, "E208.7.5.2", {"start": v(-22.95, 21.44) * mm, "end": v(-20.95, 21.44) * mm});
            skLineSegment(sketch, "E208.7.5.3", {"start": v(-20.95, 23.44) * mm, "end": v(-20.95, 21.44) * mm});
            skLineSegment(sketch, "E208.7.6.0", {"start": v(-22.95, 19.44) * mm, "end": v(-20.95, 19.44) * mm});
            skLineSegment(sketch, "E208.7.6.1", {"start": v(-22.95, 19.44) * mm, "end": v(-22.95, 17.44) * mm});
            skLineSegment(sketch, "E208.7.6.2", {"start": v(-22.95, 17.44) * mm, "end": v(-20.95, 17.44) * mm});
            skLineSegment(sketch, "E208.7.6.3", {"start": v(-20.95, 19.44) * mm, "end": v(-20.95, 17.44) * mm});
            skLineSegment(sketch, "E208.7.7.0", {"start": v(-22.95, 15.44) * mm, "end": v(-20.95, 15.44) * mm});
            skLineSegment(sketch, "E208.7.7.1", {"start": v(-22.95, 15.44) * mm, "end": v(-22.95, 13.44) * mm});
            skLineSegment(sketch, "E208.7.7.2", {"start": v(-22.95, 13.44) * mm, "end": v(-20.95, 13.44) * mm});
            skLineSegment(sketch, "E208.7.7.3", {"start": v(-20.95, 15.44) * mm, "end": v(-20.95, 13.44) * mm});
            skLineSegment(sketch, "E208.7.8.0", {"start": v(-22.95, 11.44) * mm, "end": v(-20.95, 11.44) * mm});
            skLineSegment(sketch, "E208.7.8.1", {"start": v(-22.95, 11.44) * mm, "end": v(-22.95, 9.44) * mm});
            skLineSegment(sketch, "E208.7.8.2", {"start": v(-22.95, 9.44) * mm, "end": v(-20.95, 9.44) * mm});
            skLineSegment(sketch, "E208.7.8.3", {"start": v(-20.95, 11.44) * mm, "end": v(-20.95, 9.44) * mm});
            skLineSegment(sketch, "E208.7.9.0", {"start": v(-22.95, 7.44) * mm, "end": v(-20.95, 7.44) * mm});
            skLineSegment(sketch, "E208.7.9.1", {"start": v(-22.95, 7.44) * mm, "end": v(-22.95, 5.44) * mm});
            skLineSegment(sketch, "E208.7.9.2", {"start": v(-22.95, 5.44) * mm, "end": v(-20.95, 5.44) * mm});
            skLineSegment(sketch, "E208.7.9.3", {"start": v(-20.95, 7.44) * mm, "end": v(-20.95, 5.44) * mm});
            skLineSegment(sketch, "E208.7.10.0", {"start": v(-22.95, 3.44) * mm, "end": v(-20.95, 3.44) * mm});
            skLineSegment(sketch, "E208.7.10.1", {"start": v(-22.95, 3.44) * mm, "end": v(-22.95, 1.44) * mm});
            skLineSegment(sketch, "E208.7.10.2", {"start": v(-22.95, 1.44) * mm, "end": v(-20.95, 1.44) * mm});
            skLineSegment(sketch, "E208.7.10.3", {"start": v(-20.95, 3.44) * mm, "end": v(-20.95, 1.44) * mm});
            skLineSegment(sketch, "E208.7.11.0", {"start": v(-22.95, -0.56) * mm, "end": v(-20.95, -0.56) * mm});
            skLineSegment(sketch, "E208.7.11.1", {"start": v(-22.95, -0.56) * mm, "end": v(-22.95, -2.56) * mm});
            skLineSegment(sketch, "E208.7.11.2", {"start": v(-22.95, -2.56) * mm, "end": v(-20.95, -2.56) * mm});
            skLineSegment(sketch, "E208.7.11.3", {"start": v(-20.95, -0.56) * mm, "end": v(-20.95, -2.56) * mm});
            skLineSegment(sketch, "E208.7.12.0", {"start": v(-22.95, -4.56) * mm, "end": v(-20.95, -4.56) * mm});
            skLineSegment(sketch, "E208.7.12.1", {"start": v(-22.95, -4.56) * mm, "end": v(-22.95, -6.56) * mm});
            skLineSegment(sketch, "E208.7.12.2", {"start": v(-22.95, -6.56) * mm, "end": v(-20.95, -6.56) * mm});
            skLineSegment(sketch, "E208.7.12.3", {"start": v(-20.95, -4.56) * mm, "end": v(-20.95, -6.56) * mm});
            skLineSegment(sketch, "E208.7.13.0", {"start": v(-22.95, -8.56) * mm, "end": v(-20.95, -8.56) * mm});
            skLineSegment(sketch, "E208.7.13.1", {"start": v(-22.95, -8.56) * mm, "end": v(-22.95, -10.56) * mm});
            skLineSegment(sketch, "E208.7.13.2", {"start": v(-22.95, -10.56) * mm, "end": v(-20.95, -10.56) * mm});
            skLineSegment(sketch, "E208.7.13.3", {"start": v(-20.95, -8.56) * mm, "end": v(-20.95, -10.56) * mm});
            skLineSegment(sketch, "E208.7.14.0", {"start": v(-22.95, -12.56) * mm, "end": v(-20.95, -12.56) * mm});
            skLineSegment(sketch, "E208.7.14.1", {"start": v(-22.95, -12.56) * mm, "end": v(-22.95, -14.56) * mm});
            skLineSegment(sketch, "E208.7.14.2", {"start": v(-22.95, -14.56) * mm, "end": v(-20.95, -14.56) * mm});
            skLineSegment(sketch, "E208.7.14.3", {"start": v(-20.95, -12.56) * mm, "end": v(-20.95, -14.56) * mm});
            skLineSegment(sketch, "E208.7.15.0", {"start": v(-22.95, -16.56) * mm, "end": v(-20.95, -16.56) * mm});
            skLineSegment(sketch, "E208.7.15.1", {"start": v(-22.95, -16.56) * mm, "end": v(-22.95, -18.56) * mm});
            skLineSegment(sketch, "E208.7.15.2", {"start": v(-22.95, -18.56) * mm, "end": v(-20.95, -18.56) * mm});
            skLineSegment(sketch, "E208.7.15.3", {"start": v(-20.95, -16.56) * mm, "end": v(-20.95, -18.56) * mm});
            skLineSegment(sketch, "E208.7.16.0", {"start": v(-22.95, -20.56) * mm, "end": v(-20.95, -20.56) * mm});
            skLineSegment(sketch, "E208.7.16.1", {"start": v(-22.95, -20.56) * mm, "end": v(-22.95, -22.56) * mm});
            skLineSegment(sketch, "E208.7.16.2", {"start": v(-22.95, -22.56) * mm, "end": v(-20.95, -22.56) * mm});
            skLineSegment(sketch, "E208.7.16.3", {"start": v(-20.95, -20.56) * mm, "end": v(-20.95, -22.56) * mm});
            skLineSegment(sketch, "E208.7.17.0", {"start": v(-22.95, -24.56) * mm, "end": v(-20.95, -24.56) * mm});
            skLineSegment(sketch, "E208.7.17.1", {"start": v(-22.95, -24.56) * mm, "end": v(-22.95, -26.56) * mm});
            skLineSegment(sketch, "E208.7.17.2", {"start": v(-22.95, -26.56) * mm, "end": v(-20.95, -26.56) * mm});
            skLineSegment(sketch, "E208.7.17.3", {"start": v(-20.95, -24.56) * mm, "end": v(-20.95, -26.56) * mm});
            skLineSegment(sketch, "E208.7.18.0", {"start": v(-22.95, -28.56) * mm, "end": v(-20.95, -28.56) * mm});
            skLineSegment(sketch, "E208.7.18.1", {"start": v(-22.95, -28.56) * mm, "end": v(-22.95, -30.56) * mm});
            skLineSegment(sketch, "E208.7.18.2", {"start": v(-22.95, -30.56) * mm, "end": v(-20.95, -30.56) * mm});
            skLineSegment(sketch, "E208.7.18.3", {"start": v(-20.95, -28.56) * mm, "end": v(-20.95, -30.56) * mm});
            skLineSegment(sketch, "E208.7.19.0", {"start": v(-22.95, -32.56) * mm, "end": v(-20.95, -32.56) * mm});
            skLineSegment(sketch, "E208.7.19.1", {"start": v(-22.95, -32.56) * mm, "end": v(-22.95, -34.56) * mm});
            skLineSegment(sketch, "E208.7.19.2", {"start": v(-22.95, -34.56) * mm, "end": v(-20.95, -34.56) * mm});
            skLineSegment(sketch, "E208.7.19.3", {"start": v(-20.95, -32.56) * mm, "end": v(-20.95, -34.56) * mm});
            skLineSegment(sketch, "E208.7.20.0", {"start": v(-22.95, -36.56) * mm, "end": v(-20.95, -36.56) * mm});
            skLineSegment(sketch, "E208.7.20.1", {"start": v(-22.95, -36.56) * mm, "end": v(-22.95, -38.56) * mm});
            skLineSegment(sketch, "E208.7.20.2", {"start": v(-22.95, -38.56) * mm, "end": v(-20.95, -38.56) * mm});
            skLineSegment(sketch, "E208.7.20.3", {"start": v(-20.95, -36.56) * mm, "end": v(-20.95, -38.56) * mm});
            skLineSegment(sketch, "E208.7.21.0", {"start": v(-22.95, -40.56) * mm, "end": v(-20.95, -40.56) * mm});
            skLineSegment(sketch, "E208.7.21.1", {"start": v(-22.95, -40.56) * mm, "end": v(-22.95, -42.56) * mm});
            skLineSegment(sketch, "E208.7.21.2", {"start": v(-22.95, -42.56) * mm, "end": v(-20.95, -42.56) * mm});
            skLineSegment(sketch, "E208.7.21.3", {"start": v(-20.95, -40.56) * mm, "end": v(-20.95, -42.56) * mm});
            skLineSegment(sketch, "E208.8.0.0", {"start": v(-18.95, 43.44) * mm, "end": v(-16.95, 43.44) * mm});
            skLineSegment(sketch, "E208.8.0.1", {"start": v(-18.95, 43.44) * mm, "end": v(-18.95, 41.44) * mm});
            skLineSegment(sketch, "E208.8.0.2", {"start": v(-18.95, 41.44) * mm, "end": v(-16.95, 41.44) * mm});
            skLineSegment(sketch, "E208.8.0.3", {"start": v(-16.95, 43.44) * mm, "end": v(-16.95, 41.44) * mm});
            skLineSegment(sketch, "E208.8.1.0", {"start": v(-18.95, 39.44) * mm, "end": v(-16.95, 39.44) * mm});
            skLineSegment(sketch, "E208.8.1.1", {"start": v(-18.95, 39.44) * mm, "end": v(-18.95, 37.44) * mm});
            skLineSegment(sketch, "E208.8.1.2", {"start": v(-18.95, 37.44) * mm, "end": v(-16.95, 37.44) * mm});
            skLineSegment(sketch, "E208.8.1.3", {"start": v(-16.95, 39.44) * mm, "end": v(-16.95, 37.44) * mm});
            skLineSegment(sketch, "E208.8.2.0", {"start": v(-18.95, 35.44) * mm, "end": v(-16.95, 35.44) * mm});
            skLineSegment(sketch, "E208.8.2.1", {"start": v(-18.95, 35.44) * mm, "end": v(-18.95, 33.44) * mm});
            skLineSegment(sketch, "E208.8.2.2", {"start": v(-18.95, 33.44) * mm, "end": v(-16.95, 33.44) * mm});
            skLineSegment(sketch, "E208.8.2.3", {"start": v(-16.95, 35.44) * mm, "end": v(-16.95, 33.44) * mm});
            skLineSegment(sketch, "E208.8.3.0", {"start": v(-18.95, 31.44) * mm, "end": v(-16.95, 31.44) * mm});
            skLineSegment(sketch, "E208.8.3.1", {"start": v(-18.95, 31.44) * mm, "end": v(-18.95, 29.44) * mm});
            skLineSegment(sketch, "E208.8.3.2", {"start": v(-18.95, 29.44) * mm, "end": v(-16.95, 29.44) * mm});
            skLineSegment(sketch, "E208.8.3.3", {"start": v(-16.95, 31.44) * mm, "end": v(-16.95, 29.44) * mm});
            skLineSegment(sketch, "E208.8.4.0", {"start": v(-18.95, 27.44) * mm, "end": v(-16.95, 27.44) * mm});
            skLineSegment(sketch, "E208.8.4.1", {"start": v(-18.95, 27.44) * mm, "end": v(-18.95, 25.44) * mm});
            skLineSegment(sketch, "E208.8.4.2", {"start": v(-18.95, 25.44) * mm, "end": v(-16.95, 25.44) * mm});
            skLineSegment(sketch, "E208.8.4.3", {"start": v(-16.95, 27.44) * mm, "end": v(-16.95, 25.44) * mm});
            skLineSegment(sketch, "E208.8.5.0", {"start": v(-18.95, 23.44) * mm, "end": v(-16.95, 23.44) * mm});
            skLineSegment(sketch, "E208.8.5.1", {"start": v(-18.95, 23.44) * mm, "end": v(-18.95, 21.44) * mm});
            skLineSegment(sketch, "E208.8.5.2", {"start": v(-18.95, 21.44) * mm, "end": v(-16.95, 21.44) * mm});
            skLineSegment(sketch, "E208.8.5.3", {"start": v(-16.95, 23.44) * mm, "end": v(-16.95, 21.44) * mm});
            skLineSegment(sketch, "E208.8.6.0", {"start": v(-18.95, 19.44) * mm, "end": v(-16.95, 19.44) * mm});
            skLineSegment(sketch, "E208.8.6.1", {"start": v(-18.95, 19.44) * mm, "end": v(-18.95, 17.44) * mm});
            skLineSegment(sketch, "E208.8.6.2", {"start": v(-18.95, 17.44) * mm, "end": v(-16.95, 17.44) * mm});
            skLineSegment(sketch, "E208.8.6.3", {"start": v(-16.95, 19.44) * mm, "end": v(-16.95, 17.44) * mm});
            skLineSegment(sketch, "E208.8.7.0", {"start": v(-18.95, 15.44) * mm, "end": v(-16.95, 15.44) * mm});
            skLineSegment(sketch, "E208.8.7.1", {"start": v(-18.95, 15.44) * mm, "end": v(-18.95, 13.44) * mm});
            skLineSegment(sketch, "E208.8.7.2", {"start": v(-18.95, 13.44) * mm, "end": v(-16.95, 13.44) * mm});
            skLineSegment(sketch, "E208.8.7.3", {"start": v(-16.95, 15.44) * mm, "end": v(-16.95, 13.44) * mm});
            skLineSegment(sketch, "E208.8.8.0", {"start": v(-18.95, 11.44) * mm, "end": v(-16.95, 11.44) * mm});
            skLineSegment(sketch, "E208.8.8.1", {"start": v(-18.95, 11.44) * mm, "end": v(-18.95, 9.44) * mm});
            skLineSegment(sketch, "E208.8.8.2", {"start": v(-18.95, 9.44) * mm, "end": v(-16.95, 9.44) * mm});
            skLineSegment(sketch, "E208.8.8.3", {"start": v(-16.95, 11.44) * mm, "end": v(-16.95, 9.44) * mm});
            skLineSegment(sketch, "E208.8.9.0", {"start": v(-18.95, 7.44) * mm, "end": v(-16.95, 7.44) * mm});
            skLineSegment(sketch, "E208.8.9.1", {"start": v(-18.95, 7.44) * mm, "end": v(-18.95, 5.44) * mm});
            skLineSegment(sketch, "E208.8.9.2", {"start": v(-18.95, 5.44) * mm, "end": v(-16.95, 5.44) * mm});
            skLineSegment(sketch, "E208.8.9.3", {"start": v(-16.95, 7.44) * mm, "end": v(-16.95, 5.44) * mm});
            skLineSegment(sketch, "E208.8.10.0", {"start": v(-18.95, 3.44) * mm, "end": v(-16.95, 3.44) * mm});
            skLineSegment(sketch, "E208.8.10.1", {"start": v(-18.95, 3.44) * mm, "end": v(-18.95, 1.44) * mm});
            skLineSegment(sketch, "E208.8.10.2", {"start": v(-18.95, 1.44) * mm, "end": v(-16.95, 1.44) * mm});
            skLineSegment(sketch, "E208.8.10.3", {"start": v(-16.95, 3.44) * mm, "end": v(-16.95, 1.44) * mm});
            skLineSegment(sketch, "E208.8.11.0", {"start": v(-18.95, -0.56) * mm, "end": v(-16.95, -0.56) * mm});
            skLineSegment(sketch, "E208.8.11.1", {"start": v(-18.95, -0.56) * mm, "end": v(-18.95, -2.56) * mm});
            skLineSegment(sketch, "E208.8.11.2", {"start": v(-18.95, -2.56) * mm, "end": v(-16.95, -2.56) * mm});
            skLineSegment(sketch, "E208.8.11.3", {"start": v(-16.95, -0.56) * mm, "end": v(-16.95, -2.56) * mm});
            skLineSegment(sketch, "E208.8.12.0", {"start": v(-18.95, -4.56) * mm, "end": v(-16.95, -4.56) * mm});
            skLineSegment(sketch, "E208.8.12.1", {"start": v(-18.95, -4.56) * mm, "end": v(-18.95, -6.56) * mm});
            skLineSegment(sketch, "E208.8.12.2", {"start": v(-18.95, -6.56) * mm, "end": v(-16.95, -6.56) * mm});
            skLineSegment(sketch, "E208.8.12.3", {"start": v(-16.95, -4.56) * mm, "end": v(-16.95, -6.56) * mm});
            skLineSegment(sketch, "E208.8.13.0", {"start": v(-18.95, -8.56) * mm, "end": v(-16.95, -8.56) * mm});
            skLineSegment(sketch, "E208.8.13.1", {"start": v(-18.95, -8.56) * mm, "end": v(-18.95, -10.56) * mm});
            skLineSegment(sketch, "E208.8.13.2", {"start": v(-18.95, -10.56) * mm, "end": v(-16.95, -10.56) * mm});
            skLineSegment(sketch, "E208.8.13.3", {"start": v(-16.95, -8.56) * mm, "end": v(-16.95, -10.56) * mm});
            skLineSegment(sketch, "E208.8.14.0", {"start": v(-18.95, -12.56) * mm, "end": v(-16.95, -12.56) * mm});
            skLineSegment(sketch, "E208.8.14.1", {"start": v(-18.95, -12.56) * mm, "end": v(-18.95, -14.56) * mm});
            skLineSegment(sketch, "E208.8.14.2", {"start": v(-18.95, -14.56) * mm, "end": v(-16.95, -14.56) * mm});
            skLineSegment(sketch, "E208.8.14.3", {"start": v(-16.95, -12.56) * mm, "end": v(-16.95, -14.56) * mm});
            skLineSegment(sketch, "E208.8.15.0", {"start": v(-18.95, -16.56) * mm, "end": v(-16.95, -16.56) * mm});
            skLineSegment(sketch, "E208.8.15.1", {"start": v(-18.95, -16.56) * mm, "end": v(-18.95, -18.56) * mm});
            skLineSegment(sketch, "E208.8.15.2", {"start": v(-18.95, -18.56) * mm, "end": v(-16.95, -18.56) * mm});
            skLineSegment(sketch, "E208.8.15.3", {"start": v(-16.95, -16.56) * mm, "end": v(-16.95, -18.56) * mm});
            skLineSegment(sketch, "E208.8.16.0", {"start": v(-18.95, -20.56) * mm, "end": v(-16.95, -20.56) * mm});
            skLineSegment(sketch, "E208.8.16.1", {"start": v(-18.95, -20.56) * mm, "end": v(-18.95, -22.56) * mm});
            skLineSegment(sketch, "E208.8.16.2", {"start": v(-18.95, -22.56) * mm, "end": v(-16.95, -22.56) * mm});
            skLineSegment(sketch, "E208.8.16.3", {"start": v(-16.95, -20.56) * mm, "end": v(-16.95, -22.56) * mm});
            skLineSegment(sketch, "E208.8.17.0", {"start": v(-18.95, -24.56) * mm, "end": v(-16.95, -24.56) * mm});
            skLineSegment(sketch, "E208.8.17.1", {"start": v(-18.95, -24.56) * mm, "end": v(-18.95, -26.56) * mm});
            skLineSegment(sketch, "E208.8.17.2", {"start": v(-18.95, -26.56) * mm, "end": v(-16.95, -26.56) * mm});
            skLineSegment(sketch, "E208.8.17.3", {"start": v(-16.95, -24.56) * mm, "end": v(-16.95, -26.56) * mm});
            skLineSegment(sketch, "E208.8.18.0", {"start": v(-18.95, -28.56) * mm, "end": v(-16.95, -28.56) * mm});
            skLineSegment(sketch, "E208.8.18.1", {"start": v(-18.95, -28.56) * mm, "end": v(-18.95, -30.56) * mm});
            skLineSegment(sketch, "E208.8.18.2", {"start": v(-18.95, -30.56) * mm, "end": v(-16.95, -30.56) * mm});
            skLineSegment(sketch, "E208.8.18.3", {"start": v(-16.95, -28.56) * mm, "end": v(-16.95, -30.56) * mm});
            skLineSegment(sketch, "E208.8.19.0", {"start": v(-18.95, -32.56) * mm, "end": v(-16.95, -32.56) * mm});
            skLineSegment(sketch, "E208.8.19.1", {"start": v(-18.95, -32.56) * mm, "end": v(-18.95, -34.56) * mm});
            skLineSegment(sketch, "E208.8.19.2", {"start": v(-18.95, -34.56) * mm, "end": v(-16.95, -34.56) * mm});
            skLineSegment(sketch, "E208.8.19.3", {"start": v(-16.95, -32.56) * mm, "end": v(-16.95, -34.56) * mm});
            skLineSegment(sketch, "E208.8.20.0", {"start": v(-18.95, -36.56) * mm, "end": v(-16.95, -36.56) * mm});
            skLineSegment(sketch, "E208.8.20.1", {"start": v(-18.95, -36.56) * mm, "end": v(-18.95, -38.56) * mm});
            skLineSegment(sketch, "E208.8.20.2", {"start": v(-18.95, -38.56) * mm, "end": v(-16.95, -38.56) * mm});
            skLineSegment(sketch, "E208.8.20.3", {"start": v(-16.95, -36.56) * mm, "end": v(-16.95, -38.56) * mm});
            skLineSegment(sketch, "E208.8.21.0", {"start": v(-18.95, -40.56) * mm, "end": v(-16.95, -40.56) * mm});
            skLineSegment(sketch, "E208.8.21.1", {"start": v(-18.95, -40.56) * mm, "end": v(-18.95, -42.56) * mm});
            skLineSegment(sketch, "E208.8.21.2", {"start": v(-18.95, -42.56) * mm, "end": v(-16.95, -42.56) * mm});
            skLineSegment(sketch, "E208.8.21.3", {"start": v(-16.95, -40.56) * mm, "end": v(-16.95, -42.56) * mm});
            skLineSegment(sketch, "E208.9.0.0", {"start": v(-14.95, 43.44) * mm, "end": v(-12.95, 43.44) * mm});
            skLineSegment(sketch, "E208.9.0.1", {"start": v(-14.95, 43.44) * mm, "end": v(-14.95, 41.44) * mm});
            skLineSegment(sketch, "E208.9.0.2", {"start": v(-14.95, 41.44) * mm, "end": v(-12.95, 41.44) * mm});
            skLineSegment(sketch, "E208.9.0.3", {"start": v(-12.95, 43.44) * mm, "end": v(-12.95, 41.44) * mm});
            skLineSegment(sketch, "E208.9.1.0", {"start": v(-14.95, 39.44) * mm, "end": v(-12.95, 39.44) * mm});
            skLineSegment(sketch, "E208.9.1.1", {"start": v(-14.95, 39.44) * mm, "end": v(-14.95, 37.44) * mm});
            skLineSegment(sketch, "E208.9.1.2", {"start": v(-14.95, 37.44) * mm, "end": v(-12.95, 37.44) * mm});
            skLineSegment(sketch, "E208.9.1.3", {"start": v(-12.95, 39.44) * mm, "end": v(-12.95, 37.44) * mm});
            skLineSegment(sketch, "E208.9.2.0", {"start": v(-14.95, 35.44) * mm, "end": v(-12.95, 35.44) * mm});
            skLineSegment(sketch, "E208.9.2.1", {"start": v(-14.95, 35.44) * mm, "end": v(-14.95, 33.44) * mm});
            skLineSegment(sketch, "E208.9.2.2", {"start": v(-14.95, 33.44) * mm, "end": v(-12.95, 33.44) * mm});
            skLineSegment(sketch, "E208.9.2.3", {"start": v(-12.95, 35.44) * mm, "end": v(-12.95, 33.44) * mm});
            skLineSegment(sketch, "E208.9.3.0", {"start": v(-14.95, 31.44) * mm, "end": v(-12.95, 31.44) * mm});
            skLineSegment(sketch, "E208.9.3.1", {"start": v(-14.95, 31.44) * mm, "end": v(-14.95, 29.44) * mm});
            skLineSegment(sketch, "E208.9.3.2", {"start": v(-14.95, 29.44) * mm, "end": v(-12.95, 29.44) * mm});
            skLineSegment(sketch, "E208.9.3.3", {"start": v(-12.95, 31.44) * mm, "end": v(-12.95, 29.44) * mm});
            skLineSegment(sketch, "E208.9.4.0", {"start": v(-14.95, 27.44) * mm, "end": v(-12.95, 27.44) * mm});
            skLineSegment(sketch, "E208.9.4.1", {"start": v(-14.95, 27.44) * mm, "end": v(-14.95, 25.44) * mm});
            skLineSegment(sketch, "E208.9.4.2", {"start": v(-14.95, 25.44) * mm, "end": v(-12.95, 25.44) * mm});
            skLineSegment(sketch, "E208.9.4.3", {"start": v(-12.95, 27.44) * mm, "end": v(-12.95, 25.44) * mm});
            skLineSegment(sketch, "E208.9.5.0", {"start": v(-14.95, 23.44) * mm, "end": v(-12.95, 23.44) * mm});
            skLineSegment(sketch, "E208.9.5.1", {"start": v(-14.95, 23.44) * mm, "end": v(-14.95, 21.44) * mm});
            skLineSegment(sketch, "E208.9.5.2", {"start": v(-14.95, 21.44) * mm, "end": v(-12.95, 21.44) * mm});
            skLineSegment(sketch, "E208.9.5.3", {"start": v(-12.95, 23.44) * mm, "end": v(-12.95, 21.44) * mm});
            skLineSegment(sketch, "E208.9.6.0", {"start": v(-14.95, 19.44) * mm, "end": v(-12.95, 19.44) * mm});
            skLineSegment(sketch, "E208.9.6.1", {"start": v(-14.95, 19.44) * mm, "end": v(-14.95, 17.44) * mm});
            skLineSegment(sketch, "E208.9.6.2", {"start": v(-14.95, 17.44) * mm, "end": v(-12.95, 17.44) * mm});
            skLineSegment(sketch, "E208.9.6.3", {"start": v(-12.95, 19.44) * mm, "end": v(-12.95, 17.44) * mm});
            skLineSegment(sketch, "E208.9.7.0", {"start": v(-14.95, 15.44) * mm, "end": v(-12.95, 15.44) * mm});
            skLineSegment(sketch, "E208.9.7.1", {"start": v(-14.95, 15.44) * mm, "end": v(-14.95, 13.44) * mm});
            skLineSegment(sketch, "E208.9.7.2", {"start": v(-14.95, 13.44) * mm, "end": v(-12.95, 13.44) * mm});
            skLineSegment(sketch, "E208.9.7.3", {"start": v(-12.95, 15.44) * mm, "end": v(-12.95, 13.44) * mm});
            skLineSegment(sketch, "E208.9.8.0", {"start": v(-14.95, 11.44) * mm, "end": v(-12.95, 11.44) * mm});
            skLineSegment(sketch, "E208.9.8.1", {"start": v(-14.95, 11.44) * mm, "end": v(-14.95, 9.44) * mm});
            skLineSegment(sketch, "E208.9.8.2", {"start": v(-14.95, 9.44) * mm, "end": v(-12.95, 9.44) * mm});
            skLineSegment(sketch, "E208.9.8.3", {"start": v(-12.95, 11.44) * mm, "end": v(-12.95, 9.44) * mm});
            skLineSegment(sketch, "E208.9.9.0", {"start": v(-14.95, 7.44) * mm, "end": v(-12.95, 7.44) * mm});
            skLineSegment(sketch, "E208.9.9.1", {"start": v(-14.95, 7.44) * mm, "end": v(-14.95, 5.44) * mm});
            skLineSegment(sketch, "E208.9.9.2", {"start": v(-14.95, 5.44) * mm, "end": v(-12.95, 5.44) * mm});
            skLineSegment(sketch, "E208.9.9.3", {"start": v(-12.95, 7.44) * mm, "end": v(-12.95, 5.44) * mm});
            skLineSegment(sketch, "E208.9.10.0", {"start": v(-14.95, 3.44) * mm, "end": v(-12.95, 3.44) * mm});
            skLineSegment(sketch, "E208.9.10.1", {"start": v(-14.95, 3.44) * mm, "end": v(-14.95, 1.44) * mm});
            skLineSegment(sketch, "E208.9.10.2", {"start": v(-14.95, 1.44) * mm, "end": v(-12.95, 1.44) * mm});
            skLineSegment(sketch, "E208.9.10.3", {"start": v(-12.95, 3.44) * mm, "end": v(-12.95, 1.44) * mm});
            skLineSegment(sketch, "E208.9.11.0", {"start": v(-14.95, -0.56) * mm, "end": v(-12.95, -0.56) * mm});
            skLineSegment(sketch, "E208.9.11.1", {"start": v(-14.95, -0.56) * mm, "end": v(-14.95, -2.56) * mm});
            skLineSegment(sketch, "E208.9.11.2", {"start": v(-14.95, -2.56) * mm, "end": v(-12.95, -2.56) * mm});
            skLineSegment(sketch, "E208.9.11.3", {"start": v(-12.95, -0.56) * mm, "end": v(-12.95, -2.56) * mm});
            skLineSegment(sketch, "E208.9.12.0", {"start": v(-14.95, -4.56) * mm, "end": v(-12.95, -4.56) * mm});
            skLineSegment(sketch, "E208.9.12.1", {"start": v(-14.95, -4.56) * mm, "end": v(-14.95, -6.56) * mm});
            skLineSegment(sketch, "E208.9.12.2", {"start": v(-14.95, -6.56) * mm, "end": v(-12.95, -6.56) * mm});
            skLineSegment(sketch, "E208.9.12.3", {"start": v(-12.95, -4.56) * mm, "end": v(-12.95, -6.56) * mm});
            skLineSegment(sketch, "E208.9.13.0", {"start": v(-14.95, -8.56) * mm, "end": v(-12.95, -8.56) * mm});
            skLineSegment(sketch, "E208.9.13.1", {"start": v(-14.95, -8.56) * mm, "end": v(-14.95, -10.56) * mm});
            skLineSegment(sketch, "E208.9.13.2", {"start": v(-14.95, -10.56) * mm, "end": v(-12.95, -10.56) * mm});
            skLineSegment(sketch, "E208.9.13.3", {"start": v(-12.95, -8.56) * mm, "end": v(-12.95, -10.56) * mm});
            skLineSegment(sketch, "E208.9.14.0", {"start": v(-14.95, -12.56) * mm, "end": v(-12.95, -12.56) * mm});
            skLineSegment(sketch, "E208.9.14.1", {"start": v(-14.95, -12.56) * mm, "end": v(-14.95, -14.56) * mm});
            skLineSegment(sketch, "E208.9.14.2", {"start": v(-14.95, -14.56) * mm, "end": v(-12.95, -14.56) * mm});
            skLineSegment(sketch, "E208.9.14.3", {"start": v(-12.95, -12.56) * mm, "end": v(-12.95, -14.56) * mm});
            skLineSegment(sketch, "E208.9.15.0", {"start": v(-14.95, -16.56) * mm, "end": v(-12.95, -16.56) * mm});
            skLineSegment(sketch, "E208.9.15.1", {"start": v(-14.95, -16.56) * mm, "end": v(-14.95, -18.56) * mm});
            skLineSegment(sketch, "E208.9.15.2", {"start": v(-14.95, -18.56) * mm, "end": v(-12.95, -18.56) * mm});
            skLineSegment(sketch, "E208.9.15.3", {"start": v(-12.95, -16.56) * mm, "end": v(-12.95, -18.56) * mm});
            skLineSegment(sketch, "E208.9.16.0", {"start": v(-14.95, -20.56) * mm, "end": v(-12.95, -20.56) * mm});
            skLineSegment(sketch, "E208.9.16.1", {"start": v(-14.95, -20.56) * mm, "end": v(-14.95, -22.56) * mm});
            skLineSegment(sketch, "E208.9.16.2", {"start": v(-14.95, -22.56) * mm, "end": v(-12.95, -22.56) * mm});
            skLineSegment(sketch, "E208.9.16.3", {"start": v(-12.95, -20.56) * mm, "end": v(-12.95, -22.56) * mm});
            skLineSegment(sketch, "E208.9.17.0", {"start": v(-14.95, -24.56) * mm, "end": v(-12.95, -24.56) * mm});
            skLineSegment(sketch, "E208.9.17.1", {"start": v(-14.95, -24.56) * mm, "end": v(-14.95, -26.56) * mm});
            skLineSegment(sketch, "E208.9.17.2", {"start": v(-14.95, -26.56) * mm, "end": v(-12.95, -26.56) * mm});
            skLineSegment(sketch, "E208.9.17.3", {"start": v(-12.95, -24.56) * mm, "end": v(-12.95, -26.56) * mm});
            skLineSegment(sketch, "E208.9.18.0", {"start": v(-14.95, -28.56) * mm, "end": v(-12.95, -28.56) * mm});
            skLineSegment(sketch, "E208.9.18.1", {"start": v(-14.95, -28.56) * mm, "end": v(-14.95, -30.56) * mm});
            skLineSegment(sketch, "E208.9.18.2", {"start": v(-14.95, -30.56) * mm, "end": v(-12.95, -30.56) * mm});
            skLineSegment(sketch, "E208.9.18.3", {"start": v(-12.95, -28.56) * mm, "end": v(-12.95, -30.56) * mm});
            skLineSegment(sketch, "E208.9.19.0", {"start": v(-14.95, -32.56) * mm, "end": v(-12.95, -32.56) * mm});
            skLineSegment(sketch, "E208.9.19.1", {"start": v(-14.95, -32.56) * mm, "end": v(-14.95, -34.56) * mm});
            skLineSegment(sketch, "E208.9.19.2", {"start": v(-14.95, -34.56) * mm, "end": v(-12.95, -34.56) * mm});
            skLineSegment(sketch, "E208.9.19.3", {"start": v(-12.95, -32.56) * mm, "end": v(-12.95, -34.56) * mm});
            skLineSegment(sketch, "E208.9.20.0", {"start": v(-14.95, -36.56) * mm, "end": v(-12.95, -36.56) * mm});
            skLineSegment(sketch, "E208.9.20.1", {"start": v(-14.95, -36.56) * mm, "end": v(-14.95, -38.56) * mm});
            skLineSegment(sketch, "E208.9.20.2", {"start": v(-14.95, -38.56) * mm, "end": v(-12.95, -38.56) * mm});
            skLineSegment(sketch, "E208.9.20.3", {"start": v(-12.95, -36.56) * mm, "end": v(-12.95, -38.56) * mm});
            skLineSegment(sketch, "E208.9.21.0", {"start": v(-14.95, -40.56) * mm, "end": v(-12.95, -40.56) * mm});
            skLineSegment(sketch, "E208.9.21.1", {"start": v(-14.95, -40.56) * mm, "end": v(-14.95, -42.56) * mm});
            skLineSegment(sketch, "E208.9.21.2", {"start": v(-14.95, -42.56) * mm, "end": v(-12.95, -42.56) * mm});
            skLineSegment(sketch, "E208.9.21.3", {"start": v(-12.95, -40.56) * mm, "end": v(-12.95, -42.56) * mm});
            skLineSegment(sketch, "E208.10.0.0", {"start": v(-10.95, 43.44) * mm, "end": v(-8.95, 43.44) * mm});
            skLineSegment(sketch, "E208.10.0.1", {"start": v(-10.95, 43.44) * mm, "end": v(-10.95, 41.44) * mm});
            skLineSegment(sketch, "E208.10.0.2", {"start": v(-10.95, 41.44) * mm, "end": v(-8.95, 41.44) * mm});
            skLineSegment(sketch, "E208.10.0.3", {"start": v(-8.95, 43.44) * mm, "end": v(-8.95, 41.44) * mm});
            skLineSegment(sketch, "E208.10.1.0", {"start": v(-10.95, 39.44) * mm, "end": v(-8.95, 39.44) * mm});
            skLineSegment(sketch, "E208.10.1.1", {"start": v(-10.95, 39.44) * mm, "end": v(-10.95, 37.44) * mm});
            skLineSegment(sketch, "E208.10.1.2", {"start": v(-10.95, 37.44) * mm, "end": v(-8.95, 37.44) * mm});
            skLineSegment(sketch, "E208.10.1.3", {"start": v(-8.95, 39.44) * mm, "end": v(-8.95, 37.44) * mm});
            skLineSegment(sketch, "E208.10.2.0", {"start": v(-10.95, 35.44) * mm, "end": v(-8.95, 35.44) * mm});
            skLineSegment(sketch, "E208.10.2.1", {"start": v(-10.95, 35.44) * mm, "end": v(-10.95, 33.44) * mm});
            skLineSegment(sketch, "E208.10.2.2", {"start": v(-10.95, 33.44) * mm, "end": v(-8.95, 33.44) * mm});
            skLineSegment(sketch, "E208.10.2.3", {"start": v(-8.95, 35.44) * mm, "end": v(-8.95, 33.44) * mm});
            skLineSegment(sketch, "E208.10.3.0", {"start": v(-10.95, 31.44) * mm, "end": v(-8.95, 31.44) * mm});
            skLineSegment(sketch, "E208.10.3.1", {"start": v(-10.95, 31.44) * mm, "end": v(-10.95, 29.44) * mm});
            skLineSegment(sketch, "E208.10.3.2", {"start": v(-10.95, 29.44) * mm, "end": v(-8.95, 29.44) * mm});
            skLineSegment(sketch, "E208.10.3.3", {"start": v(-8.95, 31.44) * mm, "end": v(-8.95, 29.44) * mm});
            skLineSegment(sketch, "E208.10.4.0", {"start": v(-10.95, 27.44) * mm, "end": v(-8.95, 27.44) * mm});
            skLineSegment(sketch, "E208.10.4.1", {"start": v(-10.95, 27.44) * mm, "end": v(-10.95, 25.44) * mm});
            skLineSegment(sketch, "E208.10.4.2", {"start": v(-10.95, 25.44) * mm, "end": v(-8.95, 25.44) * mm});
            skLineSegment(sketch, "E208.10.4.3", {"start": v(-8.95, 27.44) * mm, "end": v(-8.95, 25.44) * mm});
            skLineSegment(sketch, "E208.10.5.0", {"start": v(-10.95, 23.44) * mm, "end": v(-8.95, 23.44) * mm});
            skLineSegment(sketch, "E208.10.5.1", {"start": v(-10.95, 23.44) * mm, "end": v(-10.95, 21.44) * mm});
            skLineSegment(sketch, "E208.10.5.2", {"start": v(-10.95, 21.44) * mm, "end": v(-8.95, 21.44) * mm});
            skLineSegment(sketch, "E208.10.5.3", {"start": v(-8.95, 23.44) * mm, "end": v(-8.95, 21.44) * mm});
            skLineSegment(sketch, "E208.10.6.0", {"start": v(-10.95, 19.44) * mm, "end": v(-8.95, 19.44) * mm});
            skLineSegment(sketch, "E208.10.6.1", {"start": v(-10.95, 19.44) * mm, "end": v(-10.95, 17.44) * mm});
            skLineSegment(sketch, "E208.10.6.2", {"start": v(-10.95, 17.44) * mm, "end": v(-8.95, 17.44) * mm});
            skLineSegment(sketch, "E208.10.6.3", {"start": v(-8.95, 19.44) * mm, "end": v(-8.95, 17.44) * mm});
            skLineSegment(sketch, "E208.10.7.0", {"start": v(-10.95, 15.44) * mm, "end": v(-8.95, 15.44) * mm});
            skLineSegment(sketch, "E208.10.7.1", {"start": v(-10.95, 15.44) * mm, "end": v(-10.95, 13.44) * mm});
            skLineSegment(sketch, "E208.10.7.2", {"start": v(-10.95, 13.44) * mm, "end": v(-8.95, 13.44) * mm});
            skLineSegment(sketch, "E208.10.7.3", {"start": v(-8.95, 15.44) * mm, "end": v(-8.95, 13.44) * mm});
            skLineSegment(sketch, "E208.10.8.0", {"start": v(-10.95, 11.44) * mm, "end": v(-8.95, 11.44) * mm});
            skLineSegment(sketch, "E208.10.8.1", {"start": v(-10.95, 11.44) * mm, "end": v(-10.95, 9.44) * mm});
            skLineSegment(sketch, "E208.10.8.2", {"start": v(-10.95, 9.44) * mm, "end": v(-8.95, 9.44) * mm});
            skLineSegment(sketch, "E208.10.8.3", {"start": v(-8.95, 11.44) * mm, "end": v(-8.95, 9.44) * mm});
            skLineSegment(sketch, "E208.10.9.0", {"start": v(-10.95, 7.44) * mm, "end": v(-8.95, 7.44) * mm});
            skLineSegment(sketch, "E208.10.9.1", {"start": v(-10.95, 7.44) * mm, "end": v(-10.95, 5.44) * mm});
            skLineSegment(sketch, "E208.10.9.2", {"start": v(-10.95, 5.44) * mm, "end": v(-8.95, 5.44) * mm});
            skLineSegment(sketch, "E208.10.9.3", {"start": v(-8.95, 7.44) * mm, "end": v(-8.95, 5.44) * mm});
            skLineSegment(sketch, "E208.10.10.0", {"start": v(-10.95, 3.44) * mm, "end": v(-8.95, 3.44) * mm});
            skLineSegment(sketch, "E208.10.10.1", {"start": v(-10.95, 3.44) * mm, "end": v(-10.95, 1.44) * mm});
            skLineSegment(sketch, "E208.10.10.2", {"start": v(-10.95, 1.44) * mm, "end": v(-8.95, 1.44) * mm});
            skLineSegment(sketch, "E208.10.10.3", {"start": v(-8.95, 3.44) * mm, "end": v(-8.95, 1.44) * mm});
            skLineSegment(sketch, "E208.10.11.0", {"start": v(-10.95, -0.56) * mm, "end": v(-8.95, -0.56) * mm});
            skLineSegment(sketch, "E208.10.11.1", {"start": v(-10.95, -0.56) * mm, "end": v(-10.95, -2.56) * mm});
            skLineSegment(sketch, "E208.10.11.2", {"start": v(-10.95, -2.56) * mm, "end": v(-8.95, -2.56) * mm});
            skLineSegment(sketch, "E208.10.11.3", {"start": v(-8.95, -0.56) * mm, "end": v(-8.95, -2.56) * mm});
            skLineSegment(sketch, "E208.10.12.0", {"start": v(-10.95, -4.56) * mm, "end": v(-8.95, -4.56) * mm});
            skLineSegment(sketch, "E208.10.12.1", {"start": v(-10.95, -4.56) * mm, "end": v(-10.95, -6.56) * mm});
            skLineSegment(sketch, "E208.10.12.2", {"start": v(-10.95, -6.56) * mm, "end": v(-8.95, -6.56) * mm});
            skLineSegment(sketch, "E208.10.12.3", {"start": v(-8.95, -4.56) * mm, "end": v(-8.95, -6.56) * mm});
            skLineSegment(sketch, "E208.10.13.0", {"start": v(-10.95, -8.56) * mm, "end": v(-8.95, -8.56) * mm});
            skLineSegment(sketch, "E208.10.13.1", {"start": v(-10.95, -8.56) * mm, "end": v(-10.95, -10.56) * mm});
            skLineSegment(sketch, "E208.10.13.2", {"start": v(-10.95, -10.56) * mm, "end": v(-8.95, -10.56) * mm});
            skLineSegment(sketch, "E208.10.13.3", {"start": v(-8.95, -8.56) * mm, "end": v(-8.95, -10.56) * mm});
            skLineSegment(sketch, "E208.10.14.0", {"start": v(-10.95, -12.56) * mm, "end": v(-8.95, -12.56) * mm});
            skLineSegment(sketch, "E208.10.14.1", {"start": v(-10.95, -12.56) * mm, "end": v(-10.95, -14.56) * mm});
            skLineSegment(sketch, "E208.10.14.2", {"start": v(-10.95, -14.56) * mm, "end": v(-8.95, -14.56) * mm});
            skLineSegment(sketch, "E208.10.14.3", {"start": v(-8.95, -12.56) * mm, "end": v(-8.95, -14.56) * mm});
            skLineSegment(sketch, "E208.10.15.0", {"start": v(-10.95, -16.56) * mm, "end": v(-8.95, -16.56) * mm});
            skLineSegment(sketch, "E208.10.15.1", {"start": v(-10.95, -16.56) * mm, "end": v(-10.95, -18.56) * mm});
            skLineSegment(sketch, "E208.10.15.2", {"start": v(-10.95, -18.56) * mm, "end": v(-8.95, -18.56) * mm});
            skLineSegment(sketch, "E208.10.15.3", {"start": v(-8.95, -16.56) * mm, "end": v(-8.95, -18.56) * mm});
            skLineSegment(sketch, "E208.10.16.0", {"start": v(-10.95, -20.56) * mm, "end": v(-8.95, -20.56) * mm});
            skLineSegment(sketch, "E208.10.16.1", {"start": v(-10.95, -20.56) * mm, "end": v(-10.95, -22.56) * mm});
            skLineSegment(sketch, "E208.10.16.2", {"start": v(-10.95, -22.56) * mm, "end": v(-8.95, -22.56) * mm});
            skLineSegment(sketch, "E208.10.16.3", {"start": v(-8.95, -20.56) * mm, "end": v(-8.95, -22.56) * mm});
            skLineSegment(sketch, "E208.10.17.0", {"start": v(-10.95, -24.56) * mm, "end": v(-8.95, -24.56) * mm});
            skLineSegment(sketch, "E208.10.17.1", {"start": v(-10.95, -24.56) * mm, "end": v(-10.95, -26.56) * mm});
            skLineSegment(sketch, "E208.10.17.2", {"start": v(-10.95, -26.56) * mm, "end": v(-8.95, -26.56) * mm});
            skLineSegment(sketch, "E208.10.17.3", {"start": v(-8.95, -24.56) * mm, "end": v(-8.95, -26.56) * mm});
            skLineSegment(sketch, "E208.10.18.0", {"start": v(-10.95, -28.56) * mm, "end": v(-8.95, -28.56) * mm});
            skLineSegment(sketch, "E208.10.18.1", {"start": v(-10.95, -28.56) * mm, "end": v(-10.95, -30.56) * mm});
            skLineSegment(sketch, "E208.10.18.2", {"start": v(-10.95, -30.56) * mm, "end": v(-8.95, -30.56) * mm});
            skLineSegment(sketch, "E208.10.18.3", {"start": v(-8.95, -28.56) * mm, "end": v(-8.95, -30.56) * mm});
            skLineSegment(sketch, "E208.10.19.0", {"start": v(-10.95, -32.56) * mm, "end": v(-8.95, -32.56) * mm});
            skLineSegment(sketch, "E208.10.19.1", {"start": v(-10.95, -32.56) * mm, "end": v(-10.95, -34.56) * mm});
            skLineSegment(sketch, "E208.10.19.2", {"start": v(-10.95, -34.56) * mm, "end": v(-8.95, -34.56) * mm});
            skLineSegment(sketch, "E208.10.19.3", {"start": v(-8.95, -32.56) * mm, "end": v(-8.95, -34.56) * mm});
            skLineSegment(sketch, "E208.10.20.0", {"start": v(-10.95, -36.56) * mm, "end": v(-8.95, -36.56) * mm});
            skLineSegment(sketch, "E208.10.20.1", {"start": v(-10.95, -36.56) * mm, "end": v(-10.95, -38.56) * mm});
            skLineSegment(sketch, "E208.10.20.2", {"start": v(-10.95, -38.56) * mm, "end": v(-8.95, -38.56) * mm});
            skLineSegment(sketch, "E208.10.20.3", {"start": v(-8.95, -36.56) * mm, "end": v(-8.95, -38.56) * mm});
            skLineSegment(sketch, "E208.10.21.0", {"start": v(-10.95, -40.56) * mm, "end": v(-8.95, -40.56) * mm});
            skLineSegment(sketch, "E208.10.21.1", {"start": v(-10.95, -40.56) * mm, "end": v(-10.95, -42.56) * mm});
            skLineSegment(sketch, "E208.10.21.2", {"start": v(-10.95, -42.56) * mm, "end": v(-8.95, -42.56) * mm});
            skLineSegment(sketch, "E208.10.21.3", {"start": v(-8.95, -40.56) * mm, "end": v(-8.95, -42.56) * mm});
            skLineSegment(sketch, "E208.11.0.0", {"start": v(-6.95, 43.44) * mm, "end": v(-4.95, 43.44) * mm});
            skLineSegment(sketch, "E208.11.0.1", {"start": v(-6.95, 43.44) * mm, "end": v(-6.95, 41.44) * mm});
            skLineSegment(sketch, "E208.11.0.2", {"start": v(-6.95, 41.44) * mm, "end": v(-4.95, 41.44) * mm});
            skLineSegment(sketch, "E208.11.0.3", {"start": v(-4.95, 43.44) * mm, "end": v(-4.95, 41.44) * mm});
            skLineSegment(sketch, "E208.11.1.0", {"start": v(-6.95, 39.44) * mm, "end": v(-4.95, 39.44) * mm});
            skLineSegment(sketch, "E208.11.1.1", {"start": v(-6.95, 39.44) * mm, "end": v(-6.95, 37.44) * mm});
            skLineSegment(sketch, "E208.11.1.2", {"start": v(-6.95, 37.44) * mm, "end": v(-4.95, 37.44) * mm});
            skLineSegment(sketch, "E208.11.1.3", {"start": v(-4.95, 39.44) * mm, "end": v(-4.95, 37.44) * mm});
            skLineSegment(sketch, "E208.11.2.0", {"start": v(-6.95, 35.44) * mm, "end": v(-4.95, 35.44) * mm});
            skLineSegment(sketch, "E208.11.2.1", {"start": v(-6.95, 35.44) * mm, "end": v(-6.95, 33.44) * mm});
            skLineSegment(sketch, "E208.11.2.2", {"start": v(-6.95, 33.44) * mm, "end": v(-4.95, 33.44) * mm});
            skLineSegment(sketch, "E208.11.2.3", {"start": v(-4.95, 35.44) * mm, "end": v(-4.95, 33.44) * mm});
            skLineSegment(sketch, "E208.11.3.0", {"start": v(-6.95, 31.44) * mm, "end": v(-4.95, 31.44) * mm});
            skLineSegment(sketch, "E208.11.3.1", {"start": v(-6.95, 31.44) * mm, "end": v(-6.95, 29.44) * mm});
            skLineSegment(sketch, "E208.11.3.2", {"start": v(-6.95, 29.44) * mm, "end": v(-4.95, 29.44) * mm});
            skLineSegment(sketch, "E208.11.3.3", {"start": v(-4.95, 31.44) * mm, "end": v(-4.95, 29.44) * mm});
            skLineSegment(sketch, "E208.11.4.0", {"start": v(-6.95, 27.44) * mm, "end": v(-4.95, 27.44) * mm});
            skLineSegment(sketch, "E208.11.4.1", {"start": v(-6.95, 27.44) * mm, "end": v(-6.95, 25.44) * mm});
            skLineSegment(sketch, "E208.11.4.2", {"start": v(-6.95, 25.44) * mm, "end": v(-4.95, 25.44) * mm});
            skLineSegment(sketch, "E208.11.4.3", {"start": v(-4.95, 27.44) * mm, "end": v(-4.95, 25.44) * mm});
            skLineSegment(sketch, "E208.11.5.0", {"start": v(-6.95, 23.44) * mm, "end": v(-4.95, 23.44) * mm});
            skLineSegment(sketch, "E208.11.5.1", {"start": v(-6.95, 23.44) * mm, "end": v(-6.95, 21.44) * mm});
            skLineSegment(sketch, "E208.11.5.2", {"start": v(-6.95, 21.44) * mm, "end": v(-4.95, 21.44) * mm});
            skLineSegment(sketch, "E208.11.5.3", {"start": v(-4.95, 23.44) * mm, "end": v(-4.95, 21.44) * mm});
            skLineSegment(sketch, "E208.11.6.0", {"start": v(-6.95, 19.44) * mm, "end": v(-4.95, 19.44) * mm});
            skLineSegment(sketch, "E208.11.6.1", {"start": v(-6.95, 19.44) * mm, "end": v(-6.95, 17.44) * mm});
            skLineSegment(sketch, "E208.11.6.2", {"start": v(-6.95, 17.44) * mm, "end": v(-4.95, 17.44) * mm});
            skLineSegment(sketch, "E208.11.6.3", {"start": v(-4.95, 19.44) * mm, "end": v(-4.95, 17.44) * mm});
            skLineSegment(sketch, "E208.11.7.0", {"start": v(-6.95, 15.44) * mm, "end": v(-4.95, 15.44) * mm});
            skLineSegment(sketch, "E208.11.7.1", {"start": v(-6.95, 15.44) * mm, "end": v(-6.95, 13.44) * mm});
            skLineSegment(sketch, "E208.11.7.2", {"start": v(-6.95, 13.44) * mm, "end": v(-4.95, 13.44) * mm});
            skLineSegment(sketch, "E208.11.7.3", {"start": v(-4.95, 15.44) * mm, "end": v(-4.95, 13.44) * mm});
            skLineSegment(sketch, "E208.11.8.0", {"start": v(-6.95, 11.44) * mm, "end": v(-4.95, 11.44) * mm});
            skLineSegment(sketch, "E208.11.8.1", {"start": v(-6.95, 11.44) * mm, "end": v(-6.95, 9.44) * mm});
            skLineSegment(sketch, "E208.11.8.2", {"start": v(-6.95, 9.44) * mm, "end": v(-4.95, 9.44) * mm});
            skLineSegment(sketch, "E208.11.8.3", {"start": v(-4.95, 11.44) * mm, "end": v(-4.95, 9.44) * mm});
            skLineSegment(sketch, "E208.11.9.0", {"start": v(-6.95, 7.44) * mm, "end": v(-4.95, 7.44) * mm});
            skLineSegment(sketch, "E208.11.9.1", {"start": v(-6.95, 7.44) * mm, "end": v(-6.95, 5.44) * mm});
            skLineSegment(sketch, "E208.11.9.2", {"start": v(-6.95, 5.44) * mm, "end": v(-4.95, 5.44) * mm});
            skLineSegment(sketch, "E208.11.9.3", {"start": v(-4.95, 7.44) * mm, "end": v(-4.95, 5.44) * mm});
            skLineSegment(sketch, "E208.11.10.0", {"start": v(-6.95, 3.44) * mm, "end": v(-4.95, 3.44) * mm});
            skLineSegment(sketch, "E208.11.10.1", {"start": v(-6.95, 3.44) * mm, "end": v(-6.95, 1.44) * mm});
            skLineSegment(sketch, "E208.11.10.2", {"start": v(-6.95, 1.44) * mm, "end": v(-4.95, 1.44) * mm});
            skLineSegment(sketch, "E208.11.10.3", {"start": v(-4.95, 3.44) * mm, "end": v(-4.95, 1.44) * mm});
            skLineSegment(sketch, "E208.11.11.0", {"start": v(-6.95, -0.56) * mm, "end": v(-4.95, -0.56) * mm});
            skLineSegment(sketch, "E208.11.11.1", {"start": v(-6.95, -0.56) * mm, "end": v(-6.95, -2.56) * mm});
            skLineSegment(sketch, "E208.11.11.2", {"start": v(-6.95, -2.56) * mm, "end": v(-4.95, -2.56) * mm});
            skLineSegment(sketch, "E208.11.11.3", {"start": v(-4.95, -0.56) * mm, "end": v(-4.95, -2.56) * mm});
            skLineSegment(sketch, "E208.11.12.0", {"start": v(-6.95, -4.56) * mm, "end": v(-4.95, -4.56) * mm});
            skLineSegment(sketch, "E208.11.12.1", {"start": v(-6.95, -4.56) * mm, "end": v(-6.95, -6.56) * mm});
            skLineSegment(sketch, "E208.11.12.2", {"start": v(-6.95, -6.56) * mm, "end": v(-4.95, -6.56) * mm});
            skLineSegment(sketch, "E208.11.12.3", {"start": v(-4.95, -4.56) * mm, "end": v(-4.95, -6.56) * mm});
            skLineSegment(sketch, "E208.11.13.0", {"start": v(-6.95, -8.56) * mm, "end": v(-4.95, -8.56) * mm});
            skLineSegment(sketch, "E208.11.13.1", {"start": v(-6.95, -8.56) * mm, "end": v(-6.95, -10.56) * mm});
            skLineSegment(sketch, "E208.11.13.2", {"start": v(-6.95, -10.56) * mm, "end": v(-4.95, -10.56) * mm});
            skLineSegment(sketch, "E208.11.13.3", {"start": v(-4.95, -8.56) * mm, "end": v(-4.95, -10.56) * mm});
            skLineSegment(sketch, "E208.11.14.0", {"start": v(-6.95, -12.56) * mm, "end": v(-4.95, -12.56) * mm});
            skLineSegment(sketch, "E208.11.14.1", {"start": v(-6.95, -12.56) * mm, "end": v(-6.95, -14.56) * mm});
            skLineSegment(sketch, "E208.11.14.2", {"start": v(-6.95, -14.56) * mm, "end": v(-4.95, -14.56) * mm});
            skLineSegment(sketch, "E208.11.14.3", {"start": v(-4.95, -12.56) * mm, "end": v(-4.95, -14.56) * mm});
            skLineSegment(sketch, "E208.11.15.0", {"start": v(-6.95, -16.56) * mm, "end": v(-4.95, -16.56) * mm});
            skLineSegment(sketch, "E208.11.15.1", {"start": v(-6.95, -16.56) * mm, "end": v(-6.95, -18.56) * mm});
            skLineSegment(sketch, "E208.11.15.2", {"start": v(-6.95, -18.56) * mm, "end": v(-4.95, -18.56) * mm});
            skLineSegment(sketch, "E208.11.15.3", {"start": v(-4.95, -16.56) * mm, "end": v(-4.95, -18.56) * mm});
            skLineSegment(sketch, "E208.11.16.0", {"start": v(-6.95, -20.56) * mm, "end": v(-4.95, -20.56) * mm});
            skLineSegment(sketch, "E208.11.16.1", {"start": v(-6.95, -20.56) * mm, "end": v(-6.95, -22.56) * mm});
            skLineSegment(sketch, "E208.11.16.2", {"start": v(-6.95, -22.56) * mm, "end": v(-4.95, -22.56) * mm});
            skLineSegment(sketch, "E208.11.16.3", {"start": v(-4.95, -20.56) * mm, "end": v(-4.95, -22.56) * mm});
            skLineSegment(sketch, "E208.11.17.0", {"start": v(-6.95, -24.56) * mm, "end": v(-4.95, -24.56) * mm});
            skLineSegment(sketch, "E208.11.17.1", {"start": v(-6.95, -24.56) * mm, "end": v(-6.95, -26.56) * mm});
            skLineSegment(sketch, "E208.11.17.2", {"start": v(-6.95, -26.56) * mm, "end": v(-4.95, -26.56) * mm});
            skLineSegment(sketch, "E208.11.17.3", {"start": v(-4.95, -24.56) * mm, "end": v(-4.95, -26.56) * mm});
            skLineSegment(sketch, "E208.11.18.0", {"start": v(-6.95, -28.56) * mm, "end": v(-4.95, -28.56) * mm});
            skLineSegment(sketch, "E208.11.18.1", {"start": v(-6.95, -28.56) * mm, "end": v(-6.95, -30.56) * mm});
            skLineSegment(sketch, "E208.11.18.2", {"start": v(-6.95, -30.56) * mm, "end": v(-4.95, -30.56) * mm});
            skLineSegment(sketch, "E208.11.18.3", {"start": v(-4.95, -28.56) * mm, "end": v(-4.95, -30.56) * mm});
            skLineSegment(sketch, "E208.11.19.0", {"start": v(-6.95, -32.56) * mm, "end": v(-4.95, -32.56) * mm});
            skLineSegment(sketch, "E208.11.19.1", {"start": v(-6.95, -32.56) * mm, "end": v(-6.95, -34.56) * mm});
            skLineSegment(sketch, "E208.11.19.2", {"start": v(-6.95, -34.56) * mm, "end": v(-4.95, -34.56) * mm});
            skLineSegment(sketch, "E208.11.19.3", {"start": v(-4.95, -32.56) * mm, "end": v(-4.95, -34.56) * mm});
            skLineSegment(sketch, "E208.11.20.0", {"start": v(-6.95, -36.56) * mm, "end": v(-4.95, -36.56) * mm});
            skLineSegment(sketch, "E208.11.20.1", {"start": v(-6.95, -36.56) * mm, "end": v(-6.95, -38.56) * mm});
            skLineSegment(sketch, "E208.11.20.2", {"start": v(-6.95, -38.56) * mm, "end": v(-4.95, -38.56) * mm});
            skLineSegment(sketch, "E208.11.20.3", {"start": v(-4.95, -36.56) * mm, "end": v(-4.95, -38.56) * mm});
            skLineSegment(sketch, "E208.11.21.0", {"start": v(-6.95, -40.56) * mm, "end": v(-4.95, -40.56) * mm});
            skLineSegment(sketch, "E208.11.21.1", {"start": v(-6.95, -40.56) * mm, "end": v(-6.95, -42.56) * mm});
            skLineSegment(sketch, "E208.11.21.2", {"start": v(-6.95, -42.56) * mm, "end": v(-4.95, -42.56) * mm});
            skLineSegment(sketch, "E208.11.21.3", {"start": v(-4.95, -40.56) * mm, "end": v(-4.95, -42.56) * mm});
            skLineSegment(sketch, "E208.12.0.0", {"start": v(-2.95, 43.44) * mm, "end": v(-0.95, 43.44) * mm});
            skLineSegment(sketch, "E208.12.0.1", {"start": v(-2.95, 43.44) * mm, "end": v(-2.95, 41.44) * mm});
            skLineSegment(sketch, "E208.12.0.2", {"start": v(-2.95, 41.44) * mm, "end": v(-0.95, 41.44) * mm});
            skLineSegment(sketch, "E208.12.0.3", {"start": v(-0.95, 43.44) * mm, "end": v(-0.95, 41.44) * mm});
            skLineSegment(sketch, "E208.12.1.0", {"start": v(-2.95, 39.44) * mm, "end": v(-0.95, 39.44) * mm});
            skLineSegment(sketch, "E208.12.1.1", {"start": v(-2.95, 39.44) * mm, "end": v(-2.95, 37.44) * mm});
            skLineSegment(sketch, "E208.12.1.2", {"start": v(-2.95, 37.44) * mm, "end": v(-0.95, 37.44) * mm});
            skLineSegment(sketch, "E208.12.1.3", {"start": v(-0.95, 39.44) * mm, "end": v(-0.95, 37.44) * mm});
            skLineSegment(sketch, "E208.12.2.0", {"start": v(-2.95, 35.44) * mm, "end": v(-0.95, 35.44) * mm});
            skLineSegment(sketch, "E208.12.2.1", {"start": v(-2.95, 35.44) * mm, "end": v(-2.95, 33.44) * mm});
            skLineSegment(sketch, "E208.12.2.2", {"start": v(-2.95, 33.44) * mm, "end": v(-0.95, 33.44) * mm});
            skLineSegment(sketch, "E208.12.2.3", {"start": v(-0.95, 35.44) * mm, "end": v(-0.95, 33.44) * mm});
            skLineSegment(sketch, "E208.12.3.0", {"start": v(-2.95, 31.44) * mm, "end": v(-0.95, 31.44) * mm});
            skLineSegment(sketch, "E208.12.3.1", {"start": v(-2.95, 31.44) * mm, "end": v(-2.95, 29.44) * mm});
            skLineSegment(sketch, "E208.12.3.2", {"start": v(-2.95, 29.44) * mm, "end": v(-0.95, 29.44) * mm});
            skLineSegment(sketch, "E208.12.3.3", {"start": v(-0.95, 31.44) * mm, "end": v(-0.95, 29.44) * mm});
            skLineSegment(sketch, "E208.12.4.0", {"start": v(-2.95, 27.44) * mm, "end": v(-0.95, 27.44) * mm});
            skLineSegment(sketch, "E208.12.4.1", {"start": v(-2.95, 27.44) * mm, "end": v(-2.95, 25.44) * mm});
            skLineSegment(sketch, "E208.12.4.2", {"start": v(-2.95, 25.44) * mm, "end": v(-0.95, 25.44) * mm});
            skLineSegment(sketch, "E208.12.4.3", {"start": v(-0.95, 27.44) * mm, "end": v(-0.95, 25.44) * mm});
            skLineSegment(sketch, "E208.12.5.0", {"start": v(-2.95, 23.44) * mm, "end": v(-0.95, 23.44) * mm});
            skLineSegment(sketch, "E208.12.5.1", {"start": v(-2.95, 23.44) * mm, "end": v(-2.95, 21.44) * mm});
            skLineSegment(sketch, "E208.12.5.2", {"start": v(-2.95, 21.44) * mm, "end": v(-0.95, 21.44) * mm});
            skLineSegment(sketch, "E208.12.5.3", {"start": v(-0.95, 23.44) * mm, "end": v(-0.95, 21.44) * mm});
            skLineSegment(sketch, "E208.12.6.0", {"start": v(-2.95, 19.44) * mm, "end": v(-0.95, 19.44) * mm});
            skLineSegment(sketch, "E208.12.6.1", {"start": v(-2.95, 19.44) * mm, "end": v(-2.95, 17.44) * mm});
            skLineSegment(sketch, "E208.12.6.2", {"start": v(-2.95, 17.44) * mm, "end": v(-0.95, 17.44) * mm});
            skLineSegment(sketch, "E208.12.6.3", {"start": v(-0.95, 19.44) * mm, "end": v(-0.95, 17.44) * mm});
            skLineSegment(sketch, "E208.12.7.0", {"start": v(-2.95, 15.44) * mm, "end": v(-0.95, 15.44) * mm});
            skLineSegment(sketch, "E208.12.7.1", {"start": v(-2.95, 15.44) * mm, "end": v(-2.95, 13.44) * mm});
            skLineSegment(sketch, "E208.12.7.2", {"start": v(-2.95, 13.44) * mm, "end": v(-0.95, 13.44) * mm});
            skLineSegment(sketch, "E208.12.7.3", {"start": v(-0.95, 15.44) * mm, "end": v(-0.95, 13.44) * mm});
            skLineSegment(sketch, "E208.12.8.0", {"start": v(-2.95, 11.44) * mm, "end": v(-0.95, 11.44) * mm});
            skLineSegment(sketch, "E208.12.8.1", {"start": v(-2.95, 11.44) * mm, "end": v(-2.95, 9.44) * mm});
            skLineSegment(sketch, "E208.12.8.2", {"start": v(-2.95, 9.44) * mm, "end": v(-0.95, 9.44) * mm});
            skLineSegment(sketch, "E208.12.8.3", {"start": v(-0.95, 11.44) * mm, "end": v(-0.95, 9.44) * mm});
            skLineSegment(sketch, "E208.12.9.0", {"start": v(-2.95, 7.44) * mm, "end": v(-0.95, 7.44) * mm});
            skLineSegment(sketch, "E208.12.9.1", {"start": v(-2.95, 7.44) * mm, "end": v(-2.95, 5.44) * mm});
            skLineSegment(sketch, "E208.12.9.2", {"start": v(-2.95, 5.44) * mm, "end": v(-0.95, 5.44) * mm});
            skLineSegment(sketch, "E208.12.9.3", {"start": v(-0.95, 7.44) * mm, "end": v(-0.95, 5.44) * mm});
            skLineSegment(sketch, "E208.12.10.0", {"start": v(-2.95, 3.44) * mm, "end": v(-0.95, 3.44) * mm});
            skLineSegment(sketch, "E208.12.10.1", {"start": v(-2.95, 3.44) * mm, "end": v(-2.95, 1.44) * mm});
            skLineSegment(sketch, "E208.12.10.2", {"start": v(-2.95, 1.44) * mm, "end": v(-0.95, 1.44) * mm});
            skLineSegment(sketch, "E208.12.10.3", {"start": v(-0.95, 3.44) * mm, "end": v(-0.95, 1.44) * mm});
            skLineSegment(sketch, "E208.12.11.0", {"start": v(-2.95, -0.56) * mm, "end": v(-0.95, -0.56) * mm});
            skLineSegment(sketch, "E208.12.11.1", {"start": v(-2.95, -0.56) * mm, "end": v(-2.95, -2.56) * mm});
            skLineSegment(sketch, "E208.12.11.2", {"start": v(-2.95, -2.56) * mm, "end": v(-0.95, -2.56) * mm});
            skLineSegment(sketch, "E208.12.11.3", {"start": v(-0.95, -0.56) * mm, "end": v(-0.95, -2.56) * mm});
            skLineSegment(sketch, "E208.12.12.0", {"start": v(-2.95, -4.56) * mm, "end": v(-0.95, -4.56) * mm});
            skLineSegment(sketch, "E208.12.12.1", {"start": v(-2.95, -4.56) * mm, "end": v(-2.95, -6.56) * mm});
            skLineSegment(sketch, "E208.12.12.2", {"start": v(-2.95, -6.56) * mm, "end": v(-0.95, -6.56) * mm});
            skLineSegment(sketch, "E208.12.12.3", {"start": v(-0.95, -4.56) * mm, "end": v(-0.95, -6.56) * mm});
            skLineSegment(sketch, "E208.12.13.0", {"start": v(-2.95, -8.56) * mm, "end": v(-0.95, -8.56) * mm});
            skLineSegment(sketch, "E208.12.13.1", {"start": v(-2.95, -8.56) * mm, "end": v(-2.95, -10.56) * mm});
            skLineSegment(sketch, "E208.12.13.2", {"start": v(-2.95, -10.56) * mm, "end": v(-0.95, -10.56) * mm});
            skLineSegment(sketch, "E208.12.13.3", {"start": v(-0.95, -8.56) * mm, "end": v(-0.95, -10.56) * mm});
            skLineSegment(sketch, "E208.12.14.0", {"start": v(-2.95, -12.56) * mm, "end": v(-0.95, -12.56) * mm});
            skLineSegment(sketch, "E208.12.14.1", {"start": v(-2.95, -12.56) * mm, "end": v(-2.95, -14.56) * mm});
            skLineSegment(sketch, "E208.12.14.2", {"start": v(-2.95, -14.56) * mm, "end": v(-0.95, -14.56) * mm});
            skLineSegment(sketch, "E208.12.14.3", {"start": v(-0.95, -12.56) * mm, "end": v(-0.95, -14.56) * mm});
            skLineSegment(sketch, "E208.12.15.0", {"start": v(-2.95, -16.56) * mm, "end": v(-0.95, -16.56) * mm});
            skLineSegment(sketch, "E208.12.15.1", {"start": v(-2.95, -16.56) * mm, "end": v(-2.95, -18.56) * mm});
            skLineSegment(sketch, "E208.12.15.2", {"start": v(-2.95, -18.56) * mm, "end": v(-0.95, -18.56) * mm});
            skLineSegment(sketch, "E208.12.15.3", {"start": v(-0.95, -16.56) * mm, "end": v(-0.95, -18.56) * mm});
            skLineSegment(sketch, "E208.12.16.0", {"start": v(-2.95, -20.56) * mm, "end": v(-0.95, -20.56) * mm});
            skLineSegment(sketch, "E208.12.16.1", {"start": v(-2.95, -20.56) * mm, "end": v(-2.95, -22.56) * mm});
            skLineSegment(sketch, "E208.12.16.2", {"start": v(-2.95, -22.56) * mm, "end": v(-0.95, -22.56) * mm});
            skLineSegment(sketch, "E208.12.16.3", {"start": v(-0.95, -20.56) * mm, "end": v(-0.95, -22.56) * mm});
            skLineSegment(sketch, "E208.12.17.0", {"start": v(-2.95, -24.56) * mm, "end": v(-0.95, -24.56) * mm});
            skLineSegment(sketch, "E208.12.17.1", {"start": v(-2.95, -24.56) * mm, "end": v(-2.95, -26.56) * mm});
            skLineSegment(sketch, "E208.12.17.2", {"start": v(-2.95, -26.56) * mm, "end": v(-0.95, -26.56) * mm});
            skLineSegment(sketch, "E208.12.17.3", {"start": v(-0.95, -24.56) * mm, "end": v(-0.95, -26.56) * mm});
            skLineSegment(sketch, "E208.12.18.0", {"start": v(-2.95, -28.56) * mm, "end": v(-0.95, -28.56) * mm});
            skLineSegment(sketch, "E208.12.18.1", {"start": v(-2.95, -28.56) * mm, "end": v(-2.95, -30.56) * mm});
            skLineSegment(sketch, "E208.12.18.2", {"start": v(-2.95, -30.56) * mm, "end": v(-0.95, -30.56) * mm});
            skLineSegment(sketch, "E208.12.18.3", {"start": v(-0.95, -28.56) * mm, "end": v(-0.95, -30.56) * mm});
            skLineSegment(sketch, "E208.12.19.0", {"start": v(-2.95, -32.56) * mm, "end": v(-0.95, -32.56) * mm});
            skLineSegment(sketch, "E208.12.19.1", {"start": v(-2.95, -32.56) * mm, "end": v(-2.95, -34.56) * mm});
            skLineSegment(sketch, "E208.12.19.2", {"start": v(-2.95, -34.56) * mm, "end": v(-0.95, -34.56) * mm});
            skLineSegment(sketch, "E208.12.19.3", {"start": v(-0.95, -32.56) * mm, "end": v(-0.95, -34.56) * mm});
            skLineSegment(sketch, "E208.12.20.0", {"start": v(-2.95, -36.56) * mm, "end": v(-0.95, -36.56) * mm});
            skLineSegment(sketch, "E208.12.20.1", {"start": v(-2.95, -36.56) * mm, "end": v(-2.95, -38.56) * mm});
            skLineSegment(sketch, "E208.12.20.2", {"start": v(-2.95, -38.56) * mm, "end": v(-0.95, -38.56) * mm});
            skLineSegment(sketch, "E208.12.20.3", {"start": v(-0.95, -36.56) * mm, "end": v(-0.95, -38.56) * mm});
            skLineSegment(sketch, "E208.12.21.0", {"start": v(-2.95, -40.56) * mm, "end": v(-0.95, -40.56) * mm});
            skLineSegment(sketch, "E208.12.21.1", {"start": v(-2.95, -40.56) * mm, "end": v(-2.95, -42.56) * mm});
            skLineSegment(sketch, "E208.12.21.2", {"start": v(-2.95, -42.56) * mm, "end": v(-0.95, -42.56) * mm});
            skLineSegment(sketch, "E208.12.21.3", {"start": v(-0.95, -40.56) * mm, "end": v(-0.95, -42.56) * mm});
            skLineSegment(sketch, "E208.13.0.0", {"start": v(1.05, 43.44) * mm, "end": v(3.05, 43.44) * mm});
            skLineSegment(sketch, "E208.13.0.1", {"start": v(1.05, 43.44) * mm, "end": v(1.05, 41.44) * mm});
            skLineSegment(sketch, "E208.13.0.2", {"start": v(1.05, 41.44) * mm, "end": v(3.05, 41.44) * mm});
            skLineSegment(sketch, "E208.13.0.3", {"start": v(3.05, 43.44) * mm, "end": v(3.05, 41.44) * mm});
            skLineSegment(sketch, "E208.13.1.0", {"start": v(1.05, 39.44) * mm, "end": v(3.05, 39.44) * mm});
            skLineSegment(sketch, "E208.13.1.1", {"start": v(1.05, 39.44) * mm, "end": v(1.05, 37.44) * mm});
            skLineSegment(sketch, "E208.13.1.2", {"start": v(1.05, 37.44) * mm, "end": v(3.05, 37.44) * mm});
            skLineSegment(sketch, "E208.13.1.3", {"start": v(3.05, 39.44) * mm, "end": v(3.05, 37.44) * mm});
            skLineSegment(sketch, "E208.13.2.0", {"start": v(1.05, 35.44) * mm, "end": v(3.05, 35.44) * mm});
            skLineSegment(sketch, "E208.13.2.1", {"start": v(1.05, 35.44) * mm, "end": v(1.05, 33.44) * mm});
            skLineSegment(sketch, "E208.13.2.2", {"start": v(1.05, 33.44) * mm, "end": v(3.05, 33.44) * mm});
            skLineSegment(sketch, "E208.13.2.3", {"start": v(3.05, 35.44) * mm, "end": v(3.05, 33.44) * mm});
            skLineSegment(sketch, "E208.13.3.0", {"start": v(1.05, 31.44) * mm, "end": v(3.05, 31.44) * mm});
            skLineSegment(sketch, "E208.13.3.1", {"start": v(1.05, 31.44) * mm, "end": v(1.05, 29.44) * mm});
            skLineSegment(sketch, "E208.13.3.2", {"start": v(1.05, 29.44) * mm, "end": v(3.05, 29.44) * mm});
            skLineSegment(sketch, "E208.13.3.3", {"start": v(3.05, 31.44) * mm, "end": v(3.05, 29.44) * mm});
            skLineSegment(sketch, "E208.13.4.0", {"start": v(1.05, 27.44) * mm, "end": v(3.05, 27.44) * mm});
            skLineSegment(sketch, "E208.13.4.1", {"start": v(1.05, 27.44) * mm, "end": v(1.05, 25.44) * mm});
            skLineSegment(sketch, "E208.13.4.2", {"start": v(1.05, 25.44) * mm, "end": v(3.05, 25.44) * mm});
            skLineSegment(sketch, "E208.13.4.3", {"start": v(3.05, 27.44) * mm, "end": v(3.05, 25.44) * mm});
            skLineSegment(sketch, "E208.13.5.0", {"start": v(1.05, 23.44) * mm, "end": v(3.05, 23.44) * mm});
            skLineSegment(sketch, "E208.13.5.1", {"start": v(1.05, 23.44) * mm, "end": v(1.05, 21.44) * mm});
            skLineSegment(sketch, "E208.13.5.2", {"start": v(1.05, 21.44) * mm, "end": v(3.05, 21.44) * mm});
            skLineSegment(sketch, "E208.13.5.3", {"start": v(3.05, 23.44) * mm, "end": v(3.05, 21.44) * mm});
            skLineSegment(sketch, "E208.13.6.0", {"start": v(1.05, 19.44) * mm, "end": v(3.05, 19.44) * mm});
            skLineSegment(sketch, "E208.13.6.1", {"start": v(1.05, 19.44) * mm, "end": v(1.05, 17.44) * mm});
            skLineSegment(sketch, "E208.13.6.2", {"start": v(1.05, 17.44) * mm, "end": v(3.05, 17.44) * mm});
            skLineSegment(sketch, "E208.13.6.3", {"start": v(3.05, 19.44) * mm, "end": v(3.05, 17.44) * mm});
            skLineSegment(sketch, "E208.13.7.0", {"start": v(1.05, 15.44) * mm, "end": v(3.05, 15.44) * mm});
            skLineSegment(sketch, "E208.13.7.1", {"start": v(1.05, 15.44) * mm, "end": v(1.05, 13.44) * mm});
            skLineSegment(sketch, "E208.13.7.2", {"start": v(1.05, 13.44) * mm, "end": v(3.05, 13.44) * mm});
            skLineSegment(sketch, "E208.13.7.3", {"start": v(3.05, 15.44) * mm, "end": v(3.05, 13.44) * mm});
            skLineSegment(sketch, "E208.13.8.0", {"start": v(1.05, 11.44) * mm, "end": v(3.05, 11.44) * mm});
            skLineSegment(sketch, "E208.13.8.1", {"start": v(1.05, 11.44) * mm, "end": v(1.05, 9.44) * mm});
            skLineSegment(sketch, "E208.13.8.2", {"start": v(1.05, 9.44) * mm, "end": v(3.05, 9.44) * mm});
            skLineSegment(sketch, "E208.13.8.3", {"start": v(3.05, 11.44) * mm, "end": v(3.05, 9.44) * mm});
            skLineSegment(sketch, "E208.13.9.0", {"start": v(1.05, 7.44) * mm, "end": v(3.05, 7.44) * mm});
            skLineSegment(sketch, "E208.13.9.1", {"start": v(1.05, 7.44) * mm, "end": v(1.05, 5.44) * mm});
            skLineSegment(sketch, "E208.13.9.2", {"start": v(1.05, 5.44) * mm, "end": v(3.05, 5.44) * mm});
            skLineSegment(sketch, "E208.13.9.3", {"start": v(3.05, 7.44) * mm, "end": v(3.05, 5.44) * mm});
            skLineSegment(sketch, "E208.13.10.0", {"start": v(1.05, 3.44) * mm, "end": v(3.05, 3.44) * mm});
            skLineSegment(sketch, "E208.13.10.1", {"start": v(1.05, 3.44) * mm, "end": v(1.05, 1.44) * mm});
            skLineSegment(sketch, "E208.13.10.2", {"start": v(1.05, 1.44) * mm, "end": v(3.05, 1.44) * mm});
            skLineSegment(sketch, "E208.13.10.3", {"start": v(3.05, 3.44) * mm, "end": v(3.05, 1.44) * mm});
            skLineSegment(sketch, "E208.13.11.0", {"start": v(1.05, -0.56) * mm, "end": v(3.05, -0.56) * mm});
            skLineSegment(sketch, "E208.13.11.1", {"start": v(1.05, -0.56) * mm, "end": v(1.05, -2.56) * mm});
            skLineSegment(sketch, "E208.13.11.2", {"start": v(1.05, -2.56) * mm, "end": v(3.05, -2.56) * mm});
            skLineSegment(sketch, "E208.13.11.3", {"start": v(3.05, -0.56) * mm, "end": v(3.05, -2.56) * mm});
            skLineSegment(sketch, "E208.13.12.0", {"start": v(1.05, -4.56) * mm, "end": v(3.05, -4.56) * mm});
            skLineSegment(sketch, "E208.13.12.1", {"start": v(1.05, -4.56) * mm, "end": v(1.05, -6.56) * mm});
            skLineSegment(sketch, "E208.13.12.2", {"start": v(1.05, -6.56) * mm, "end": v(3.05, -6.56) * mm});
            skLineSegment(sketch, "E208.13.12.3", {"start": v(3.05, -4.56) * mm, "end": v(3.05, -6.56) * mm});
            skLineSegment(sketch, "E208.13.13.0", {"start": v(1.05, -8.56) * mm, "end": v(3.05, -8.56) * mm});
            skLineSegment(sketch, "E208.13.13.1", {"start": v(1.05, -8.56) * mm, "end": v(1.05, -10.56) * mm});
            skLineSegment(sketch, "E208.13.13.2", {"start": v(1.05, -10.56) * mm, "end": v(3.05, -10.56) * mm});
            skLineSegment(sketch, "E208.13.13.3", {"start": v(3.05, -8.56) * mm, "end": v(3.05, -10.56) * mm});
            skLineSegment(sketch, "E208.13.14.0", {"start": v(1.05, -12.56) * mm, "end": v(3.05, -12.56) * mm});
            skLineSegment(sketch, "E208.13.14.1", {"start": v(1.05, -12.56) * mm, "end": v(1.05, -14.56) * mm});
            skLineSegment(sketch, "E208.13.14.2", {"start": v(1.05, -14.56) * mm, "end": v(3.05, -14.56) * mm});
            skLineSegment(sketch, "E208.13.14.3", {"start": v(3.05, -12.56) * mm, "end": v(3.05, -14.56) * mm});
            skLineSegment(sketch, "E208.13.15.0", {"start": v(1.05, -16.56) * mm, "end": v(3.05, -16.56) * mm});
            skLineSegment(sketch, "E208.13.15.1", {"start": v(1.05, -16.56) * mm, "end": v(1.05, -18.56) * mm});
            skLineSegment(sketch, "E208.13.15.2", {"start": v(1.05, -18.56) * mm, "end": v(3.05, -18.56) * mm});
            skLineSegment(sketch, "E208.13.15.3", {"start": v(3.05, -16.56) * mm, "end": v(3.05, -18.56) * mm});
            skLineSegment(sketch, "E208.13.16.0", {"start": v(1.05, -20.56) * mm, "end": v(3.05, -20.56) * mm});
            skLineSegment(sketch, "E208.13.16.1", {"start": v(1.05, -20.56) * mm, "end": v(1.05, -22.56) * mm});
            skLineSegment(sketch, "E208.13.16.2", {"start": v(1.05, -22.56) * mm, "end": v(3.05, -22.56) * mm});
            skLineSegment(sketch, "E208.13.16.3", {"start": v(3.05, -20.56) * mm, "end": v(3.05, -22.56) * mm});
            skLineSegment(sketch, "E208.13.17.0", {"start": v(1.05, -24.56) * mm, "end": v(3.05, -24.56) * mm});
            skLineSegment(sketch, "E208.13.17.1", {"start": v(1.05, -24.56) * mm, "end": v(1.05, -26.56) * mm});
            skLineSegment(sketch, "E208.13.17.2", {"start": v(1.05, -26.56) * mm, "end": v(3.05, -26.56) * mm});
            skLineSegment(sketch, "E208.13.17.3", {"start": v(3.05, -24.56) * mm, "end": v(3.05, -26.56) * mm});
            skLineSegment(sketch, "E208.13.18.0", {"start": v(1.05, -28.56) * mm, "end": v(3.05, -28.56) * mm});
            skLineSegment(sketch, "E208.13.18.1", {"start": v(1.05, -28.56) * mm, "end": v(1.05, -30.56) * mm});
            skLineSegment(sketch, "E208.13.18.2", {"start": v(1.05, -30.56) * mm, "end": v(3.05, -30.56) * mm});
            skLineSegment(sketch, "E208.13.18.3", {"start": v(3.05, -28.56) * mm, "end": v(3.05, -30.56) * mm});
            skLineSegment(sketch, "E208.13.19.0", {"start": v(1.05, -32.56) * mm, "end": v(3.05, -32.56) * mm});
            skLineSegment(sketch, "E208.13.19.1", {"start": v(1.05, -32.56) * mm, "end": v(1.05, -34.56) * mm});
            skLineSegment(sketch, "E208.13.19.2", {"start": v(1.05, -34.56) * mm, "end": v(3.05, -34.56) * mm});
            skLineSegment(sketch, "E208.13.19.3", {"start": v(3.05, -32.56) * mm, "end": v(3.05, -34.56) * mm});
            skLineSegment(sketch, "E208.13.20.0", {"start": v(1.05, -36.56) * mm, "end": v(3.05, -36.56) * mm});
            skLineSegment(sketch, "E208.13.20.1", {"start": v(1.05, -36.56) * mm, "end": v(1.05, -38.56) * mm});
            skLineSegment(sketch, "E208.13.20.2", {"start": v(1.05, -38.56) * mm, "end": v(3.05, -38.56) * mm});
            skLineSegment(sketch, "E208.13.20.3", {"start": v(3.05, -36.56) * mm, "end": v(3.05, -38.56) * mm});
            skLineSegment(sketch, "E208.13.21.0", {"start": v(1.05, -40.56) * mm, "end": v(3.05, -40.56) * mm});
            skLineSegment(sketch, "E208.13.21.1", {"start": v(1.05, -40.56) * mm, "end": v(1.05, -42.56) * mm});
            skLineSegment(sketch, "E208.13.21.2", {"start": v(1.05, -42.56) * mm, "end": v(3.05, -42.56) * mm});
            skLineSegment(sketch, "E208.13.21.3", {"start": v(3.05, -40.56) * mm, "end": v(3.05, -42.56) * mm});
            skLineSegment(sketch, "E208.14.0.0", {"start": v(5.05, 43.44) * mm, "end": v(7.05, 43.44) * mm});
            skLineSegment(sketch, "E208.14.0.1", {"start": v(5.05, 43.44) * mm, "end": v(5.05, 41.44) * mm});
            skLineSegment(sketch, "E208.14.0.2", {"start": v(5.05, 41.44) * mm, "end": v(7.05, 41.44) * mm});
            skLineSegment(sketch, "E208.14.0.3", {"start": v(7.05, 43.44) * mm, "end": v(7.05, 41.44) * mm});
            skLineSegment(sketch, "E208.14.1.0", {"start": v(5.05, 39.44) * mm, "end": v(7.05, 39.44) * mm});
            skLineSegment(sketch, "E208.14.1.1", {"start": v(5.05, 39.44) * mm, "end": v(5.05, 37.44) * mm});
            skLineSegment(sketch, "E208.14.1.2", {"start": v(5.05, 37.44) * mm, "end": v(7.05, 37.44) * mm});
            skLineSegment(sketch, "E208.14.1.3", {"start": v(7.05, 39.44) * mm, "end": v(7.05, 37.44) * mm});
            skLineSegment(sketch, "E208.14.2.0", {"start": v(5.05, 35.44) * mm, "end": v(7.05, 35.44) * mm});
            skLineSegment(sketch, "E208.14.2.1", {"start": v(5.05, 35.44) * mm, "end": v(5.05, 33.44) * mm});
            skLineSegment(sketch, "E208.14.2.2", {"start": v(5.05, 33.44) * mm, "end": v(7.05, 33.44) * mm});
            skLineSegment(sketch, "E208.14.2.3", {"start": v(7.05, 35.44) * mm, "end": v(7.05, 33.44) * mm});
            skLineSegment(sketch, "E208.14.3.0", {"start": v(5.05, 31.44) * mm, "end": v(7.05, 31.44) * mm});
            skLineSegment(sketch, "E208.14.3.1", {"start": v(5.05, 31.44) * mm, "end": v(5.05, 29.44) * mm});
            skLineSegment(sketch, "E208.14.3.2", {"start": v(5.05, 29.44) * mm, "end": v(7.05, 29.44) * mm});
            skLineSegment(sketch, "E208.14.3.3", {"start": v(7.05, 31.44) * mm, "end": v(7.05, 29.44) * mm});
            skLineSegment(sketch, "E208.14.4.0", {"start": v(5.05, 27.44) * mm, "end": v(7.05, 27.44) * mm});
            skLineSegment(sketch, "E208.14.4.1", {"start": v(5.05, 27.44) * mm, "end": v(5.05, 25.44) * mm});
            skLineSegment(sketch, "E208.14.4.2", {"start": v(5.05, 25.44) * mm, "end": v(7.05, 25.44) * mm});
            skLineSegment(sketch, "E208.14.4.3", {"start": v(7.05, 27.44) * mm, "end": v(7.05, 25.44) * mm});
            skLineSegment(sketch, "E208.14.5.0", {"start": v(5.05, 23.44) * mm, "end": v(7.05, 23.44) * mm});
            skLineSegment(sketch, "E208.14.5.1", {"start": v(5.05, 23.44) * mm, "end": v(5.05, 21.44) * mm});
            skLineSegment(sketch, "E208.14.5.2", {"start": v(5.05, 21.44) * mm, "end": v(7.05, 21.44) * mm});
            skLineSegment(sketch, "E208.14.5.3", {"start": v(7.05, 23.44) * mm, "end": v(7.05, 21.44) * mm});
            skLineSegment(sketch, "E208.14.6.0", {"start": v(5.05, 19.44) * mm, "end": v(7.05, 19.44) * mm});
            skLineSegment(sketch, "E208.14.6.1", {"start": v(5.05, 19.44) * mm, "end": v(5.05, 17.44) * mm});
            skLineSegment(sketch, "E208.14.6.2", {"start": v(5.05, 17.44) * mm, "end": v(7.05, 17.44) * mm});
            skLineSegment(sketch, "E208.14.6.3", {"start": v(7.05, 19.44) * mm, "end": v(7.05, 17.44) * mm});
            skLineSegment(sketch, "E208.14.7.0", {"start": v(5.05, 15.44) * mm, "end": v(7.05, 15.44) * mm});
            skLineSegment(sketch, "E208.14.7.1", {"start": v(5.05, 15.44) * mm, "end": v(5.05, 13.44) * mm});
            skLineSegment(sketch, "E208.14.7.2", {"start": v(5.05, 13.44) * mm, "end": v(7.05, 13.44) * mm});
            skLineSegment(sketch, "E208.14.7.3", {"start": v(7.05, 15.44) * mm, "end": v(7.05, 13.44) * mm});
            skLineSegment(sketch, "E208.14.8.0", {"start": v(5.05, 11.44) * mm, "end": v(7.05, 11.44) * mm});
            skLineSegment(sketch, "E208.14.8.1", {"start": v(5.05, 11.44) * mm, "end": v(5.05, 9.44) * mm});
            skLineSegment(sketch, "E208.14.8.2", {"start": v(5.05, 9.44) * mm, "end": v(7.05, 9.44) * mm});
            skLineSegment(sketch, "E208.14.8.3", {"start": v(7.05, 11.44) * mm, "end": v(7.05, 9.44) * mm});
            skLineSegment(sketch, "E208.14.9.0", {"start": v(5.05, 7.44) * mm, "end": v(7.05, 7.44) * mm});
            skLineSegment(sketch, "E208.14.9.1", {"start": v(5.05, 7.44) * mm, "end": v(5.05, 5.44) * mm});
            skLineSegment(sketch, "E208.14.9.2", {"start": v(5.05, 5.44) * mm, "end": v(7.05, 5.44) * mm});
            skLineSegment(sketch, "E208.14.9.3", {"start": v(7.05, 7.44) * mm, "end": v(7.05, 5.44) * mm});
            skLineSegment(sketch, "E208.14.10.0", {"start": v(5.05, 3.44) * mm, "end": v(7.05, 3.44) * mm});
            skLineSegment(sketch, "E208.14.10.1", {"start": v(5.05, 3.44) * mm, "end": v(5.05, 1.44) * mm});
            skLineSegment(sketch, "E208.14.10.2", {"start": v(5.05, 1.44) * mm, "end": v(7.05, 1.44) * mm});
            skLineSegment(sketch, "E208.14.10.3", {"start": v(7.05, 3.44) * mm, "end": v(7.05, 1.44) * mm});
            skLineSegment(sketch, "E208.14.11.0", {"start": v(5.05, -0.56) * mm, "end": v(7.05, -0.56) * mm});
            skLineSegment(sketch, "E208.14.11.1", {"start": v(5.05, -0.56) * mm, "end": v(5.05, -2.56) * mm});
            skLineSegment(sketch, "E208.14.11.2", {"start": v(5.05, -2.56) * mm, "end": v(7.05, -2.56) * mm});
            skLineSegment(sketch, "E208.14.11.3", {"start": v(7.05, -0.56) * mm, "end": v(7.05, -2.56) * mm});
            skLineSegment(sketch, "E208.14.12.0", {"start": v(5.05, -4.56) * mm, "end": v(7.05, -4.56) * mm});
            skLineSegment(sketch, "E208.14.12.1", {"start": v(5.05, -4.56) * mm, "end": v(5.05, -6.56) * mm});
            skLineSegment(sketch, "E208.14.12.2", {"start": v(5.05, -6.56) * mm, "end": v(7.05, -6.56) * mm});
            skLineSegment(sketch, "E208.14.12.3", {"start": v(7.05, -4.56) * mm, "end": v(7.05, -6.56) * mm});
            skLineSegment(sketch, "E208.14.13.0", {"start": v(5.05, -8.56) * mm, "end": v(7.05, -8.56) * mm});
            skLineSegment(sketch, "E208.14.13.1", {"start": v(5.05, -8.56) * mm, "end": v(5.05, -10.56) * mm});
            skLineSegment(sketch, "E208.14.13.2", {"start": v(5.05, -10.56) * mm, "end": v(7.05, -10.56) * mm});
            skLineSegment(sketch, "E208.14.13.3", {"start": v(7.05, -8.56) * mm, "end": v(7.05, -10.56) * mm});
            skLineSegment(sketch, "E208.14.14.0", {"start": v(5.05, -12.56) * mm, "end": v(7.05, -12.56) * mm});
            skLineSegment(sketch, "E208.14.14.1", {"start": v(5.05, -12.56) * mm, "end": v(5.05, -14.56) * mm});
            skLineSegment(sketch, "E208.14.14.2", {"start": v(5.05, -14.56) * mm, "end": v(7.05, -14.56) * mm});
            skLineSegment(sketch, "E208.14.14.3", {"start": v(7.05, -12.56) * mm, "end": v(7.05, -14.56) * mm});
            skLineSegment(sketch, "E208.14.15.0", {"start": v(5.05, -16.56) * mm, "end": v(7.05, -16.56) * mm});
            skLineSegment(sketch, "E208.14.15.1", {"start": v(5.05, -16.56) * mm, "end": v(5.05, -18.56) * mm});
            skLineSegment(sketch, "E208.14.15.2", {"start": v(5.05, -18.56) * mm, "end": v(7.05, -18.56) * mm});
            skLineSegment(sketch, "E208.14.15.3", {"start": v(7.05, -16.56) * mm, "end": v(7.05, -18.56) * mm});
            skLineSegment(sketch, "E208.14.16.0", {"start": v(5.05, -20.56) * mm, "end": v(7.05, -20.56) * mm});
            skLineSegment(sketch, "E208.14.16.1", {"start": v(5.05, -20.56) * mm, "end": v(5.05, -22.56) * mm});
            skLineSegment(sketch, "E208.14.16.2", {"start": v(5.05, -22.56) * mm, "end": v(7.05, -22.56) * mm});
            skLineSegment(sketch, "E208.14.16.3", {"start": v(7.05, -20.56) * mm, "end": v(7.05, -22.56) * mm});
            skLineSegment(sketch, "E208.14.17.0", {"start": v(5.05, -24.56) * mm, "end": v(7.05, -24.56) * mm});
            skLineSegment(sketch, "E208.14.17.1", {"start": v(5.05, -24.56) * mm, "end": v(5.05, -26.56) * mm});
            skLineSegment(sketch, "E208.14.17.2", {"start": v(5.05, -26.56) * mm, "end": v(7.05, -26.56) * mm});
            skLineSegment(sketch, "E208.14.17.3", {"start": v(7.05, -24.56) * mm, "end": v(7.05, -26.56) * mm});
            skLineSegment(sketch, "E208.14.18.0", {"start": v(5.05, -28.56) * mm, "end": v(7.05, -28.56) * mm});
            skLineSegment(sketch, "E208.14.18.1", {"start": v(5.05, -28.56) * mm, "end": v(5.05, -30.56) * mm});
            skLineSegment(sketch, "E208.14.18.2", {"start": v(5.05, -30.56) * mm, "end": v(7.05, -30.56) * mm});
            skLineSegment(sketch, "E208.14.18.3", {"start": v(7.05, -28.56) * mm, "end": v(7.05, -30.56) * mm});
            skLineSegment(sketch, "E208.14.19.0", {"start": v(5.05, -32.56) * mm, "end": v(7.05, -32.56) * mm});
            skLineSegment(sketch, "E208.14.19.1", {"start": v(5.05, -32.56) * mm, "end": v(5.05, -34.56) * mm});
            skLineSegment(sketch, "E208.14.19.2", {"start": v(5.05, -34.56) * mm, "end": v(7.05, -34.56) * mm});
            skLineSegment(sketch, "E208.14.19.3", {"start": v(7.05, -32.56) * mm, "end": v(7.05, -34.56) * mm});
            skLineSegment(sketch, "E208.14.20.0", {"start": v(5.05, -36.56) * mm, "end": v(7.05, -36.56) * mm});
            skLineSegment(sketch, "E208.14.20.1", {"start": v(5.05, -36.56) * mm, "end": v(5.05, -38.56) * mm});
            skLineSegment(sketch, "E208.14.20.2", {"start": v(5.05, -38.56) * mm, "end": v(7.05, -38.56) * mm});
            skLineSegment(sketch, "E208.14.20.3", {"start": v(7.05, -36.56) * mm, "end": v(7.05, -38.56) * mm});
            skLineSegment(sketch, "E208.14.21.0", {"start": v(5.05, -40.56) * mm, "end": v(7.05, -40.56) * mm});
            skLineSegment(sketch, "E208.14.21.1", {"start": v(5.05, -40.56) * mm, "end": v(5.05, -42.56) * mm});
            skLineSegment(sketch, "E208.14.21.2", {"start": v(5.05, -42.56) * mm, "end": v(7.05, -42.56) * mm});
            skLineSegment(sketch, "E208.14.21.3", {"start": v(7.05, -40.56) * mm, "end": v(7.05, -42.56) * mm});
            skLineSegment(sketch, "E208.15.0.0", {"start": v(9.05, 43.44) * mm, "end": v(11.05, 43.44) * mm});
            skLineSegment(sketch, "E208.15.0.1", {"start": v(9.05, 43.44) * mm, "end": v(9.05, 41.44) * mm});
            skLineSegment(sketch, "E208.15.0.2", {"start": v(9.05, 41.44) * mm, "end": v(11.05, 41.44) * mm});
            skLineSegment(sketch, "E208.15.0.3", {"start": v(11.05, 43.44) * mm, "end": v(11.05, 41.44) * mm});
            skLineSegment(sketch, "E208.15.1.0", {"start": v(9.05, 39.44) * mm, "end": v(11.05, 39.44) * mm});
            skLineSegment(sketch, "E208.15.1.1", {"start": v(9.05, 39.44) * mm, "end": v(9.05, 37.44) * mm});
            skLineSegment(sketch, "E208.15.1.2", {"start": v(9.05, 37.44) * mm, "end": v(11.05, 37.44) * mm});
            skLineSegment(sketch, "E208.15.1.3", {"start": v(11.05, 39.44) * mm, "end": v(11.05, 37.44) * mm});
            skLineSegment(sketch, "E208.15.2.0", {"start": v(9.05, 35.44) * mm, "end": v(11.05, 35.44) * mm});
            skLineSegment(sketch, "E208.15.2.1", {"start": v(9.05, 35.44) * mm, "end": v(9.05, 33.44) * mm});
            skLineSegment(sketch, "E208.15.2.2", {"start": v(9.05, 33.44) * mm, "end": v(11.05, 33.44) * mm});
            skLineSegment(sketch, "E208.15.2.3", {"start": v(11.05, 35.44) * mm, "end": v(11.05, 33.44) * mm});
            skLineSegment(sketch, "E208.15.3.0", {"start": v(9.05, 31.44) * mm, "end": v(11.05, 31.44) * mm});
            skLineSegment(sketch, "E208.15.3.1", {"start": v(9.05, 31.44) * mm, "end": v(9.05, 29.44) * mm});
            skLineSegment(sketch, "E208.15.3.2", {"start": v(9.05, 29.44) * mm, "end": v(11.05, 29.44) * mm});
            skLineSegment(sketch, "E208.15.3.3", {"start": v(11.05, 31.44) * mm, "end": v(11.05, 29.44) * mm});
            skLineSegment(sketch, "E208.15.4.0", {"start": v(9.05, 27.44) * mm, "end": v(11.05, 27.44) * mm});
            skLineSegment(sketch, "E208.15.4.1", {"start": v(9.05, 27.44) * mm, "end": v(9.05, 25.44) * mm});
            skLineSegment(sketch, "E208.15.4.2", {"start": v(9.05, 25.44) * mm, "end": v(11.05, 25.44) * mm});
            skLineSegment(sketch, "E208.15.4.3", {"start": v(11.05, 27.44) * mm, "end": v(11.05, 25.44) * mm});
            skLineSegment(sketch, "E208.15.5.0", {"start": v(9.05, 23.44) * mm, "end": v(11.05, 23.44) * mm});
            skLineSegment(sketch, "E208.15.5.1", {"start": v(9.05, 23.44) * mm, "end": v(9.05, 21.44) * mm});
            skLineSegment(sketch, "E208.15.5.2", {"start": v(9.05, 21.44) * mm, "end": v(11.05, 21.44) * mm});
            skLineSegment(sketch, "E208.15.5.3", {"start": v(11.05, 23.44) * mm, "end": v(11.05, 21.44) * mm});
            skLineSegment(sketch, "E208.15.6.0", {"start": v(9.05, 19.44) * mm, "end": v(11.05, 19.44) * mm});
            skLineSegment(sketch, "E208.15.6.1", {"start": v(9.05, 19.44) * mm, "end": v(9.05, 17.44) * mm});
            skLineSegment(sketch, "E208.15.6.2", {"start": v(9.05, 17.44) * mm, "end": v(11.05, 17.44) * mm});
            skLineSegment(sketch, "E208.15.6.3", {"start": v(11.05, 19.44) * mm, "end": v(11.05, 17.44) * mm});
            skLineSegment(sketch, "E208.15.7.0", {"start": v(9.05, 15.44) * mm, "end": v(11.05, 15.44) * mm});
            skLineSegment(sketch, "E208.15.7.1", {"start": v(9.05, 15.44) * mm, "end": v(9.05, 13.44) * mm});
            skLineSegment(sketch, "E208.15.7.2", {"start": v(9.05, 13.44) * mm, "end": v(11.05, 13.44) * mm});
            skLineSegment(sketch, "E208.15.7.3", {"start": v(11.05, 15.44) * mm, "end": v(11.05, 13.44) * mm});
            skLineSegment(sketch, "E208.15.8.0", {"start": v(9.05, 11.44) * mm, "end": v(11.05, 11.44) * mm});
            skLineSegment(sketch, "E208.15.8.1", {"start": v(9.05, 11.44) * mm, "end": v(9.05, 9.44) * mm});
            skLineSegment(sketch, "E208.15.8.2", {"start": v(9.05, 9.44) * mm, "end": v(11.05, 9.44) * mm});
            skLineSegment(sketch, "E208.15.8.3", {"start": v(11.05, 11.44) * mm, "end": v(11.05, 9.44) * mm});
            skLineSegment(sketch, "E208.15.9.0", {"start": v(9.05, 7.44) * mm, "end": v(11.05, 7.44) * mm});
            skLineSegment(sketch, "E208.15.9.1", {"start": v(9.05, 7.44) * mm, "end": v(9.05, 5.44) * mm});
            skLineSegment(sketch, "E208.15.9.2", {"start": v(9.05, 5.44) * mm, "end": v(11.05, 5.44) * mm});
            skLineSegment(sketch, "E208.15.9.3", {"start": v(11.05, 7.44) * mm, "end": v(11.05, 5.44) * mm});
            skLineSegment(sketch, "E208.15.10.0", {"start": v(9.05, 3.44) * mm, "end": v(11.05, 3.44) * mm});
            skLineSegment(sketch, "E208.15.10.1", {"start": v(9.05, 3.44) * mm, "end": v(9.05, 1.44) * mm});
            skLineSegment(sketch, "E208.15.10.2", {"start": v(9.05, 1.44) * mm, "end": v(11.05, 1.44) * mm});
            skLineSegment(sketch, "E208.15.10.3", {"start": v(11.05, 3.44) * mm, "end": v(11.05, 1.44) * mm});
            skLineSegment(sketch, "E208.15.11.0", {"start": v(9.05, -0.56) * mm, "end": v(11.05, -0.56) * mm});
            skLineSegment(sketch, "E208.15.11.1", {"start": v(9.05, -0.56) * mm, "end": v(9.05, -2.56) * mm});
            skLineSegment(sketch, "E208.15.11.2", {"start": v(9.05, -2.56) * mm, "end": v(11.05, -2.56) * mm});
            skLineSegment(sketch, "E208.15.11.3", {"start": v(11.05, -0.56) * mm, "end": v(11.05, -2.56) * mm});
            skLineSegment(sketch, "E208.15.12.0", {"start": v(9.05, -4.56) * mm, "end": v(11.05, -4.56) * mm});
            skLineSegment(sketch, "E208.15.12.1", {"start": v(9.05, -4.56) * mm, "end": v(9.05, -6.56) * mm});
            skLineSegment(sketch, "E208.15.12.2", {"start": v(9.05, -6.56) * mm, "end": v(11.05, -6.56) * mm});
            skLineSegment(sketch, "E208.15.12.3", {"start": v(11.05, -4.56) * mm, "end": v(11.05, -6.56) * mm});
            skLineSegment(sketch, "E208.15.13.0", {"start": v(9.05, -8.56) * mm, "end": v(11.05, -8.56) * mm});
            skLineSegment(sketch, "E208.15.13.1", {"start": v(9.05, -8.56) * mm, "end": v(9.05, -10.56) * mm});
            skLineSegment(sketch, "E208.15.13.2", {"start": v(9.05, -10.56) * mm, "end": v(11.05, -10.56) * mm});
            skLineSegment(sketch, "E208.15.13.3", {"start": v(11.05, -8.56) * mm, "end": v(11.05, -10.56) * mm});
            skLineSegment(sketch, "E208.15.14.0", {"start": v(9.05, -12.56) * mm, "end": v(11.05, -12.56) * mm});
            skLineSegment(sketch, "E208.15.14.1", {"start": v(9.05, -12.56) * mm, "end": v(9.05, -14.56) * mm});
            skLineSegment(sketch, "E208.15.14.2", {"start": v(9.05, -14.56) * mm, "end": v(11.05, -14.56) * mm});
            skLineSegment(sketch, "E208.15.14.3", {"start": v(11.05, -12.56) * mm, "end": v(11.05, -14.56) * mm});
            skLineSegment(sketch, "E208.15.15.0", {"start": v(9.05, -16.56) * mm, "end": v(11.05, -16.56) * mm});
            skLineSegment(sketch, "E208.15.15.1", {"start": v(9.05, -16.56) * mm, "end": v(9.05, -18.56) * mm});
            skLineSegment(sketch, "E208.15.15.2", {"start": v(9.05, -18.56) * mm, "end": v(11.05, -18.56) * mm});
            skLineSegment(sketch, "E208.15.15.3", {"start": v(11.05, -16.56) * mm, "end": v(11.05, -18.56) * mm});
            skLineSegment(sketch, "E208.15.16.0", {"start": v(9.05, -20.56) * mm, "end": v(11.05, -20.56) * mm});
            skLineSegment(sketch, "E208.15.16.1", {"start": v(9.05, -20.56) * mm, "end": v(9.05, -22.56) * mm});
            skLineSegment(sketch, "E208.15.16.2", {"start": v(9.05, -22.56) * mm, "end": v(11.05, -22.56) * mm});
            skLineSegment(sketch, "E208.15.16.3", {"start": v(11.05, -20.56) * mm, "end": v(11.05, -22.56) * mm});
            skLineSegment(sketch, "E208.15.17.0", {"start": v(9.05, -24.56) * mm, "end": v(11.05, -24.56) * mm});
            skLineSegment(sketch, "E208.15.17.1", {"start": v(9.05, -24.56) * mm, "end": v(9.05, -26.56) * mm});
            skLineSegment(sketch, "E208.15.17.2", {"start": v(9.05, -26.56) * mm, "end": v(11.05, -26.56) * mm});
            skLineSegment(sketch, "E208.15.17.3", {"start": v(11.05, -24.56) * mm, "end": v(11.05, -26.56) * mm});
            skLineSegment(sketch, "E208.15.18.0", {"start": v(9.05, -28.56) * mm, "end": v(11.05, -28.56) * mm});
            skLineSegment(sketch, "E208.15.18.1", {"start": v(9.05, -28.56) * mm, "end": v(9.05, -30.56) * mm});
            skLineSegment(sketch, "E208.15.18.2", {"start": v(9.05, -30.56) * mm, "end": v(11.05, -30.56) * mm});
            skLineSegment(sketch, "E208.15.18.3", {"start": v(11.05, -28.56) * mm, "end": v(11.05, -30.56) * mm});
            skLineSegment(sketch, "E208.15.19.0", {"start": v(9.05, -32.56) * mm, "end": v(11.05, -32.56) * mm});
            skLineSegment(sketch, "E208.15.19.1", {"start": v(9.05, -32.56) * mm, "end": v(9.05, -34.56) * mm});
            skLineSegment(sketch, "E208.15.19.2", {"start": v(9.05, -34.56) * mm, "end": v(11.05, -34.56) * mm});
            skLineSegment(sketch, "E208.15.19.3", {"start": v(11.05, -32.56) * mm, "end": v(11.05, -34.56) * mm});
            skLineSegment(sketch, "E208.15.20.0", {"start": v(9.05, -36.56) * mm, "end": v(11.05, -36.56) * mm});
            skLineSegment(sketch, "E208.15.20.1", {"start": v(9.05, -36.56) * mm, "end": v(9.05, -38.56) * mm});
            skLineSegment(sketch, "E208.15.20.2", {"start": v(9.05, -38.56) * mm, "end": v(11.05, -38.56) * mm});
            skLineSegment(sketch, "E208.15.20.3", {"start": v(11.05, -36.56) * mm, "end": v(11.05, -38.56) * mm});
            skLineSegment(sketch, "E208.15.21.0", {"start": v(9.05, -40.56) * mm, "end": v(11.05, -40.56) * mm});
            skLineSegment(sketch, "E208.15.21.1", {"start": v(9.05, -40.56) * mm, "end": v(9.05, -42.56) * mm});
            skLineSegment(sketch, "E208.15.21.2", {"start": v(9.05, -42.56) * mm, "end": v(11.05, -42.56) * mm});
            skLineSegment(sketch, "E208.15.21.3", {"start": v(11.05, -40.56) * mm, "end": v(11.05, -42.56) * mm});
            skLineSegment(sketch, "E208.16.0.0", {"start": v(13.05, 43.44) * mm, "end": v(15.05, 43.44) * mm});
            skLineSegment(sketch, "E208.16.0.1", {"start": v(13.05, 43.44) * mm, "end": v(13.05, 41.44) * mm});
            skLineSegment(sketch, "E208.16.0.2", {"start": v(13.05, 41.44) * mm, "end": v(15.05, 41.44) * mm});
            skLineSegment(sketch, "E208.16.0.3", {"start": v(15.05, 43.44) * mm, "end": v(15.05, 41.44) * mm});
            skLineSegment(sketch, "E208.16.1.0", {"start": v(13.05, 39.44) * mm, "end": v(15.05, 39.44) * mm});
            skLineSegment(sketch, "E208.16.1.1", {"start": v(13.05, 39.44) * mm, "end": v(13.05, 37.44) * mm});
            skLineSegment(sketch, "E208.16.1.2", {"start": v(13.05, 37.44) * mm, "end": v(15.05, 37.44) * mm});
            skLineSegment(sketch, "E208.16.1.3", {"start": v(15.05, 39.44) * mm, "end": v(15.05, 37.44) * mm});
            skLineSegment(sketch, "E208.16.2.0", {"start": v(13.05, 35.44) * mm, "end": v(15.05, 35.44) * mm});
            skLineSegment(sketch, "E208.16.2.1", {"start": v(13.05, 35.44) * mm, "end": v(13.05, 33.44) * mm});
            skLineSegment(sketch, "E208.16.2.2", {"start": v(13.05, 33.44) * mm, "end": v(15.05, 33.44) * mm});
            skLineSegment(sketch, "E208.16.2.3", {"start": v(15.05, 35.44) * mm, "end": v(15.05, 33.44) * mm});
            skLineSegment(sketch, "E208.16.3.0", {"start": v(13.05, 31.44) * mm, "end": v(15.05, 31.44) * mm});
            skLineSegment(sketch, "E208.16.3.1", {"start": v(13.05, 31.44) * mm, "end": v(13.05, 29.44) * mm});
            skLineSegment(sketch, "E208.16.3.2", {"start": v(13.05, 29.44) * mm, "end": v(15.05, 29.44) * mm});
            skLineSegment(sketch, "E208.16.3.3", {"start": v(15.05, 31.44) * mm, "end": v(15.05, 29.44) * mm});
            skLineSegment(sketch, "E208.16.4.0", {"start": v(13.05, 27.44) * mm, "end": v(15.05, 27.44) * mm});
            skLineSegment(sketch, "E208.16.4.1", {"start": v(13.05, 27.44) * mm, "end": v(13.05, 25.44) * mm});
            skLineSegment(sketch, "E208.16.4.2", {"start": v(13.05, 25.44) * mm, "end": v(15.05, 25.44) * mm});
            skLineSegment(sketch, "E208.16.4.3", {"start": v(15.05, 27.44) * mm, "end": v(15.05, 25.44) * mm});
            skLineSegment(sketch, "E208.16.5.0", {"start": v(13.05, 23.44) * mm, "end": v(15.05, 23.44) * mm});
            skLineSegment(sketch, "E208.16.5.1", {"start": v(13.05, 23.44) * mm, "end": v(13.05, 21.44) * mm});
            skLineSegment(sketch, "E208.16.5.2", {"start": v(13.05, 21.44) * mm, "end": v(15.05, 21.44) * mm});
            skLineSegment(sketch, "E208.16.5.3", {"start": v(15.05, 23.44) * mm, "end": v(15.05, 21.44) * mm});
            skLineSegment(sketch, "E208.16.6.0", {"start": v(13.05, 19.44) * mm, "end": v(15.05, 19.44) * mm});
            skLineSegment(sketch, "E208.16.6.1", {"start": v(13.05, 19.44) * mm, "end": v(13.05, 17.44) * mm});
            skLineSegment(sketch, "E208.16.6.2", {"start": v(13.05, 17.44) * mm, "end": v(15.05, 17.44) * mm});
            skLineSegment(sketch, "E208.16.6.3", {"start": v(15.05, 19.44) * mm, "end": v(15.05, 17.44) * mm});
            skLineSegment(sketch, "E208.16.7.0", {"start": v(13.05, 15.44) * mm, "end": v(15.05, 15.44) * mm});
            skLineSegment(sketch, "E208.16.7.1", {"start": v(13.05, 15.44) * mm, "end": v(13.05, 13.44) * mm});
            skLineSegment(sketch, "E208.16.7.2", {"start": v(13.05, 13.44) * mm, "end": v(15.05, 13.44) * mm});
            skLineSegment(sketch, "E208.16.7.3", {"start": v(15.05, 15.44) * mm, "end": v(15.05, 13.44) * mm});
            skLineSegment(sketch, "E208.16.8.0", {"start": v(13.05, 11.44) * mm, "end": v(15.05, 11.44) * mm});
            skLineSegment(sketch, "E208.16.8.1", {"start": v(13.05, 11.44) * mm, "end": v(13.05, 9.44) * mm});
            skLineSegment(sketch, "E208.16.8.2", {"start": v(13.05, 9.44) * mm, "end": v(15.05, 9.44) * mm});
            skLineSegment(sketch, "E208.16.8.3", {"start": v(15.05, 11.44) * mm, "end": v(15.05, 9.44) * mm});
            skLineSegment(sketch, "E208.16.9.0", {"start": v(13.05, 7.44) * mm, "end": v(15.05, 7.44) * mm});
            skLineSegment(sketch, "E208.16.9.1", {"start": v(13.05, 7.44) * mm, "end": v(13.05, 5.44) * mm});
            skLineSegment(sketch, "E208.16.9.2", {"start": v(13.05, 5.44) * mm, "end": v(15.05, 5.44) * mm});
            skLineSegment(sketch, "E208.16.9.3", {"start": v(15.05, 7.44) * mm, "end": v(15.05, 5.44) * mm});
            skLineSegment(sketch, "E208.16.10.0", {"start": v(13.05, 3.44) * mm, "end": v(15.05, 3.44) * mm});
            skLineSegment(sketch, "E208.16.10.1", {"start": v(13.05, 3.44) * mm, "end": v(13.05, 1.44) * mm});
            skLineSegment(sketch, "E208.16.10.2", {"start": v(13.05, 1.44) * mm, "end": v(15.05, 1.44) * mm});
            skLineSegment(sketch, "E208.16.10.3", {"start": v(15.05, 3.44) * mm, "end": v(15.05, 1.44) * mm});
            skLineSegment(sketch, "E208.16.11.0", {"start": v(13.05, -0.56) * mm, "end": v(15.05, -0.56) * mm});
            skLineSegment(sketch, "E208.16.11.1", {"start": v(13.05, -0.56) * mm, "end": v(13.05, -2.56) * mm});
            skLineSegment(sketch, "E208.16.11.2", {"start": v(13.05, -2.56) * mm, "end": v(15.05, -2.56) * mm});
            skLineSegment(sketch, "E208.16.11.3", {"start": v(15.05, -0.56) * mm, "end": v(15.05, -2.56) * mm});
            skLineSegment(sketch, "E208.16.12.0", {"start": v(13.05, -4.56) * mm, "end": v(15.05, -4.56) * mm});
            skLineSegment(sketch, "E208.16.12.1", {"start": v(13.05, -4.56) * mm, "end": v(13.05, -6.56) * mm});
            skLineSegment(sketch, "E208.16.12.2", {"start": v(13.05, -6.56) * mm, "end": v(15.05, -6.56) * mm});
            skLineSegment(sketch, "E208.16.12.3", {"start": v(15.05, -4.56) * mm, "end": v(15.05, -6.56) * mm});
            skLineSegment(sketch, "E208.16.13.0", {"start": v(13.05, -8.56) * mm, "end": v(15.05, -8.56) * mm});
            skLineSegment(sketch, "E208.16.13.1", {"start": v(13.05, -8.56) * mm, "end": v(13.05, -10.56) * mm});
            skLineSegment(sketch, "E208.16.13.2", {"start": v(13.05, -10.56) * mm, "end": v(15.05, -10.56) * mm});
            skLineSegment(sketch, "E208.16.13.3", {"start": v(15.05, -8.56) * mm, "end": v(15.05, -10.56) * mm});
            skLineSegment(sketch, "E208.16.14.0", {"start": v(13.05, -12.56) * mm, "end": v(15.05, -12.56) * mm});
            skLineSegment(sketch, "E208.16.14.1", {"start": v(13.05, -12.56) * mm, "end": v(13.05, -14.56) * mm});
            skLineSegment(sketch, "E208.16.14.2", {"start": v(13.05, -14.56) * mm, "end": v(15.05, -14.56) * mm});
            skLineSegment(sketch, "E208.16.14.3", {"start": v(15.05, -12.56) * mm, "end": v(15.05, -14.56) * mm});
            skLineSegment(sketch, "E208.16.15.0", {"start": v(13.05, -16.56) * mm, "end": v(15.05, -16.56) * mm});
            skLineSegment(sketch, "E208.16.15.1", {"start": v(13.05, -16.56) * mm, "end": v(13.05, -18.56) * mm});
            skLineSegment(sketch, "E208.16.15.2", {"start": v(13.05, -18.56) * mm, "end": v(15.05, -18.56) * mm});
            skLineSegment(sketch, "E208.16.15.3", {"start": v(15.05, -16.56) * mm, "end": v(15.05, -18.56) * mm});
            skLineSegment(sketch, "E208.16.16.0", {"start": v(13.05, -20.56) * mm, "end": v(15.05, -20.56) * mm});
            skLineSegment(sketch, "E208.16.16.1", {"start": v(13.05, -20.56) * mm, "end": v(13.05, -22.56) * mm});
            skLineSegment(sketch, "E208.16.16.2", {"start": v(13.05, -22.56) * mm, "end": v(15.05, -22.56) * mm});
            skLineSegment(sketch, "E208.16.16.3", {"start": v(15.05, -20.56) * mm, "end": v(15.05, -22.56) * mm});
            skLineSegment(sketch, "E208.16.17.0", {"start": v(13.05, -24.56) * mm, "end": v(15.05, -24.56) * mm});
            skLineSegment(sketch, "E208.16.17.1", {"start": v(13.05, -24.56) * mm, "end": v(13.05, -26.56) * mm});
            skLineSegment(sketch, "E208.16.17.2", {"start": v(13.05, -26.56) * mm, "end": v(15.05, -26.56) * mm});
            skLineSegment(sketch, "E208.16.17.3", {"start": v(15.05, -24.56) * mm, "end": v(15.05, -26.56) * mm});
            skLineSegment(sketch, "E208.16.18.0", {"start": v(13.05, -28.56) * mm, "end": v(15.05, -28.56) * mm});
            skLineSegment(sketch, "E208.16.18.1", {"start": v(13.05, -28.56) * mm, "end": v(13.05, -30.56) * mm});
            skLineSegment(sketch, "E208.16.18.2", {"start": v(13.05, -30.56) * mm, "end": v(15.05, -30.56) * mm});
            skLineSegment(sketch, "E208.16.18.3", {"start": v(15.05, -28.56) * mm, "end": v(15.05, -30.56) * mm});
            skLineSegment(sketch, "E208.16.19.0", {"start": v(13.05, -32.56) * mm, "end": v(15.05, -32.56) * mm});
            skLineSegment(sketch, "E208.16.19.1", {"start": v(13.05, -32.56) * mm, "end": v(13.05, -34.56) * mm});
            skLineSegment(sketch, "E208.16.19.2", {"start": v(13.05, -34.56) * mm, "end": v(15.05, -34.56) * mm});
            skLineSegment(sketch, "E208.16.19.3", {"start": v(15.05, -32.56) * mm, "end": v(15.05, -34.56) * mm});
            skLineSegment(sketch, "E208.16.20.0", {"start": v(13.05, -36.56) * mm, "end": v(15.05, -36.56) * mm});
            skLineSegment(sketch, "E208.16.20.1", {"start": v(13.05, -36.56) * mm, "end": v(13.05, -38.56) * mm});
            skLineSegment(sketch, "E208.16.20.2", {"start": v(13.05, -38.56) * mm, "end": v(15.05, -38.56) * mm});
            skLineSegment(sketch, "E208.16.20.3", {"start": v(15.05, -36.56) * mm, "end": v(15.05, -38.56) * mm});
            skLineSegment(sketch, "E208.16.21.0", {"start": v(13.05, -40.56) * mm, "end": v(15.05, -40.56) * mm});
            skLineSegment(sketch, "E208.16.21.1", {"start": v(13.05, -40.56) * mm, "end": v(13.05, -42.56) * mm});
            skLineSegment(sketch, "E208.16.21.2", {"start": v(13.05, -42.56) * mm, "end": v(15.05, -42.56) * mm});
            skLineSegment(sketch, "E208.16.21.3", {"start": v(15.05, -40.56) * mm, "end": v(15.05, -42.56) * mm});
            skLineSegment(sketch, "E208.17.0.0", {"start": v(17.05, 43.44) * mm, "end": v(19.05, 43.44) * mm});
            skLineSegment(sketch, "E208.17.0.1", {"start": v(17.05, 43.44) * mm, "end": v(17.05, 41.44) * mm});
            skLineSegment(sketch, "E208.17.0.2", {"start": v(17.05, 41.44) * mm, "end": v(19.05, 41.44) * mm});
            skLineSegment(sketch, "E208.17.0.3", {"start": v(19.05, 43.44) * mm, "end": v(19.05, 41.44) * mm});
            skLineSegment(sketch, "E208.17.1.0", {"start": v(17.05, 39.44) * mm, "end": v(19.05, 39.44) * mm});
            skLineSegment(sketch, "E208.17.1.1", {"start": v(17.05, 39.44) * mm, "end": v(17.05, 37.44) * mm});
            skLineSegment(sketch, "E208.17.1.2", {"start": v(17.05, 37.44) * mm, "end": v(19.05, 37.44) * mm});
            skLineSegment(sketch, "E208.17.1.3", {"start": v(19.05, 39.44) * mm, "end": v(19.05, 37.44) * mm});
            skLineSegment(sketch, "E208.17.2.0", {"start": v(17.05, 35.44) * mm, "end": v(19.05, 35.44) * mm});
            skLineSegment(sketch, "E208.17.2.1", {"start": v(17.05, 35.44) * mm, "end": v(17.05, 33.44) * mm});
            skLineSegment(sketch, "E208.17.2.2", {"start": v(17.05, 33.44) * mm, "end": v(19.05, 33.44) * mm});
            skLineSegment(sketch, "E208.17.2.3", {"start": v(19.05, 35.44) * mm, "end": v(19.05, 33.44) * mm});
            skLineSegment(sketch, "E208.17.3.0", {"start": v(17.05, 31.44) * mm, "end": v(19.05, 31.44) * mm});
            skLineSegment(sketch, "E208.17.3.1", {"start": v(17.05, 31.44) * mm, "end": v(17.05, 29.44) * mm});
            skLineSegment(sketch, "E208.17.3.2", {"start": v(17.05, 29.44) * mm, "end": v(19.05, 29.44) * mm});
            skLineSegment(sketch, "E208.17.3.3", {"start": v(19.05, 31.44) * mm, "end": v(19.05, 29.44) * mm});
            skLineSegment(sketch, "E208.17.4.0", {"start": v(17.05, 27.44) * mm, "end": v(19.05, 27.44) * mm});
            skLineSegment(sketch, "E208.17.4.1", {"start": v(17.05, 27.44) * mm, "end": v(17.05, 25.44) * mm});
            skLineSegment(sketch, "E208.17.4.2", {"start": v(17.05, 25.44) * mm, "end": v(19.05, 25.44) * mm});
            skLineSegment(sketch, "E208.17.4.3", {"start": v(19.05, 27.44) * mm, "end": v(19.05, 25.44) * mm});
            skLineSegment(sketch, "E208.17.5.0", {"start": v(17.05, 23.44) * mm, "end": v(19.05, 23.44) * mm});
            skLineSegment(sketch, "E208.17.5.1", {"start": v(17.05, 23.44) * mm, "end": v(17.05, 21.44) * mm});
            skLineSegment(sketch, "E208.17.5.2", {"start": v(17.05, 21.44) * mm, "end": v(19.05, 21.44) * mm});
            skLineSegment(sketch, "E208.17.5.3", {"start": v(19.05, 23.44) * mm, "end": v(19.05, 21.44) * mm});
            skLineSegment(sketch, "E208.17.6.0", {"start": v(17.05, 19.44) * mm, "end": v(19.05, 19.44) * mm});
            skLineSegment(sketch, "E208.17.6.1", {"start": v(17.05, 19.44) * mm, "end": v(17.05, 17.44) * mm});
            skLineSegment(sketch, "E208.17.6.2", {"start": v(17.05, 17.44) * mm, "end": v(19.05, 17.44) * mm});
            skLineSegment(sketch, "E208.17.6.3", {"start": v(19.05, 19.44) * mm, "end": v(19.05, 17.44) * mm});
            skLineSegment(sketch, "E208.17.7.0", {"start": v(17.05, 15.44) * mm, "end": v(19.05, 15.44) * mm});
            skLineSegment(sketch, "E208.17.7.1", {"start": v(17.05, 15.44) * mm, "end": v(17.05, 13.44) * mm});
            skLineSegment(sketch, "E208.17.7.2", {"start": v(17.05, 13.44) * mm, "end": v(19.05, 13.44) * mm});
            skLineSegment(sketch, "E208.17.7.3", {"start": v(19.05, 15.44) * mm, "end": v(19.05, 13.44) * mm});
            skLineSegment(sketch, "E208.17.8.0", {"start": v(17.05, 11.44) * mm, "end": v(19.05, 11.44) * mm});
            skLineSegment(sketch, "E208.17.8.1", {"start": v(17.05, 11.44) * mm, "end": v(17.05, 9.44) * mm});
            skLineSegment(sketch, "E208.17.8.2", {"start": v(17.05, 9.44) * mm, "end": v(19.05, 9.44) * mm});
            skLineSegment(sketch, "E208.17.8.3", {"start": v(19.05, 11.44) * mm, "end": v(19.05, 9.44) * mm});
            skLineSegment(sketch, "E208.17.9.0", {"start": v(17.05, 7.44) * mm, "end": v(19.05, 7.44) * mm});
            skLineSegment(sketch, "E208.17.9.1", {"start": v(17.05, 7.44) * mm, "end": v(17.05, 5.44) * mm});
            skLineSegment(sketch, "E208.17.9.2", {"start": v(17.05, 5.44) * mm, "end": v(19.05, 5.44) * mm});
            skLineSegment(sketch, "E208.17.9.3", {"start": v(19.05, 7.44) * mm, "end": v(19.05, 5.44) * mm});
            skLineSegment(sketch, "E208.17.10.0", {"start": v(17.05, 3.44) * mm, "end": v(19.05, 3.44) * mm});
            skLineSegment(sketch, "E208.17.10.1", {"start": v(17.05, 3.44) * mm, "end": v(17.05, 1.44) * mm});
            skLineSegment(sketch, "E208.17.10.2", {"start": v(17.05, 1.44) * mm, "end": v(19.05, 1.44) * mm});
            skLineSegment(sketch, "E208.17.10.3", {"start": v(19.05, 3.44) * mm, "end": v(19.05, 1.44) * mm});
            skLineSegment(sketch, "E208.17.11.0", {"start": v(17.05, -0.56) * mm, "end": v(19.05, -0.56) * mm});
            skLineSegment(sketch, "E208.17.11.1", {"start": v(17.05, -0.56) * mm, "end": v(17.05, -2.56) * mm});
            skLineSegment(sketch, "E208.17.11.2", {"start": v(17.05, -2.56) * mm, "end": v(19.05, -2.56) * mm});
            skLineSegment(sketch, "E208.17.11.3", {"start": v(19.05, -0.56) * mm, "end": v(19.05, -2.56) * mm});
            skLineSegment(sketch, "E208.17.12.0", {"start": v(17.05, -4.56) * mm, "end": v(19.05, -4.56) * mm});
            skLineSegment(sketch, "E208.17.12.1", {"start": v(17.05, -4.56) * mm, "end": v(17.05, -6.56) * mm});
            skLineSegment(sketch, "E208.17.12.2", {"start": v(17.05, -6.56) * mm, "end": v(19.05, -6.56) * mm});
            skLineSegment(sketch, "E208.17.12.3", {"start": v(19.05, -4.56) * mm, "end": v(19.05, -6.56) * mm});
            skLineSegment(sketch, "E208.17.13.0", {"start": v(17.05, -8.56) * mm, "end": v(19.05, -8.56) * mm});
            skLineSegment(sketch, "E208.17.13.1", {"start": v(17.05, -8.56) * mm, "end": v(17.05, -10.56) * mm});
            skLineSegment(sketch, "E208.17.13.2", {"start": v(17.05, -10.56) * mm, "end": v(19.05, -10.56) * mm});
            skLineSegment(sketch, "E208.17.13.3", {"start": v(19.05, -8.56) * mm, "end": v(19.05, -10.56) * mm});
            skLineSegment(sketch, "E208.17.14.0", {"start": v(17.05, -12.56) * mm, "end": v(19.05, -12.56) * mm});
            skLineSegment(sketch, "E208.17.14.1", {"start": v(17.05, -12.56) * mm, "end": v(17.05, -14.56) * mm});
            skLineSegment(sketch, "E208.17.14.2", {"start": v(17.05, -14.56) * mm, "end": v(19.05, -14.56) * mm});
            skLineSegment(sketch, "E208.17.14.3", {"start": v(19.05, -12.56) * mm, "end": v(19.05, -14.56) * mm});
            skLineSegment(sketch, "E208.17.15.0", {"start": v(17.05, -16.56) * mm, "end": v(19.05, -16.56) * mm});
            skLineSegment(sketch, "E208.17.15.1", {"start": v(17.05, -16.56) * mm, "end": v(17.05, -18.56) * mm});
            skLineSegment(sketch, "E208.17.15.2", {"start": v(17.05, -18.56) * mm, "end": v(19.05, -18.56) * mm});
            skLineSegment(sketch, "E208.17.15.3", {"start": v(19.05, -16.56) * mm, "end": v(19.05, -18.56) * mm});
            skLineSegment(sketch, "E208.17.16.0", {"start": v(17.05, -20.56) * mm, "end": v(19.05, -20.56) * mm});
            skLineSegment(sketch, "E208.17.16.1", {"start": v(17.05, -20.56) * mm, "end": v(17.05, -22.56) * mm});
            skLineSegment(sketch, "E208.17.16.2", {"start": v(17.05, -22.56) * mm, "end": v(19.05, -22.56) * mm});
            skLineSegment(sketch, "E208.17.16.3", {"start": v(19.05, -20.56) * mm, "end": v(19.05, -22.56) * mm});
            skLineSegment(sketch, "E208.17.17.0", {"start": v(17.05, -24.56) * mm, "end": v(19.05, -24.56) * mm});
            skLineSegment(sketch, "E208.17.17.1", {"start": v(17.05, -24.56) * mm, "end": v(17.05, -26.56) * mm});
            skLineSegment(sketch, "E208.17.17.2", {"start": v(17.05, -26.56) * mm, "end": v(19.05, -26.56) * mm});
            skLineSegment(sketch, "E208.17.17.3", {"start": v(19.05, -24.56) * mm, "end": v(19.05, -26.56) * mm});
            skLineSegment(sketch, "E208.17.18.0", {"start": v(17.05, -28.56) * mm, "end": v(19.05, -28.56) * mm});
            skLineSegment(sketch, "E208.17.18.1", {"start": v(17.05, -28.56) * mm, "end": v(17.05, -30.56) * mm});
            skLineSegment(sketch, "E208.17.18.2", {"start": v(17.05, -30.56) * mm, "end": v(19.05, -30.56) * mm});
            skLineSegment(sketch, "E208.17.18.3", {"start": v(19.05, -28.56) * mm, "end": v(19.05, -30.56) * mm});
            skLineSegment(sketch, "E208.17.19.0", {"start": v(17.05, -32.56) * mm, "end": v(19.05, -32.56) * mm});
            skLineSegment(sketch, "E208.17.19.1", {"start": v(17.05, -32.56) * mm, "end": v(17.05, -34.56) * mm});
            skLineSegment(sketch, "E208.17.19.2", {"start": v(17.05, -34.56) * mm, "end": v(19.05, -34.56) * mm});
            skLineSegment(sketch, "E208.17.19.3", {"start": v(19.05, -32.56) * mm, "end": v(19.05, -34.56) * mm});
            skLineSegment(sketch, "E208.17.20.0", {"start": v(17.05, -36.56) * mm, "end": v(19.05, -36.56) * mm});
            skLineSegment(sketch, "E208.17.20.1", {"start": v(17.05, -36.56) * mm, "end": v(17.05, -38.56) * mm});
            skLineSegment(sketch, "E208.17.20.2", {"start": v(17.05, -38.56) * mm, "end": v(19.05, -38.56) * mm});
            skLineSegment(sketch, "E208.17.20.3", {"start": v(19.05, -36.56) * mm, "end": v(19.05, -38.56) * mm});
            skLineSegment(sketch, "E208.17.21.0", {"start": v(17.05, -40.56) * mm, "end": v(19.05, -40.56) * mm});
            skLineSegment(sketch, "E208.17.21.1", {"start": v(17.05, -40.56) * mm, "end": v(17.05, -42.56) * mm});
            skLineSegment(sketch, "E208.17.21.2", {"start": v(17.05, -42.56) * mm, "end": v(19.05, -42.56) * mm});
            skLineSegment(sketch, "E208.17.21.3", {"start": v(19.05, -40.56) * mm, "end": v(19.05, -42.56) * mm});
            skLineSegment(sketch, "E208.18.0.0", {"start": v(21.05, 43.44) * mm, "end": v(23.05, 43.44) * mm});
            skLineSegment(sketch, "E208.18.0.1", {"start": v(21.05, 43.44) * mm, "end": v(21.05, 41.44) * mm});
            skLineSegment(sketch, "E208.18.0.2", {"start": v(21.05, 41.44) * mm, "end": v(23.05, 41.44) * mm});
            skLineSegment(sketch, "E208.18.0.3", {"start": v(23.05, 43.44) * mm, "end": v(23.05, 41.44) * mm});
            skLineSegment(sketch, "E208.18.1.0", {"start": v(21.05, 39.44) * mm, "end": v(23.05, 39.44) * mm});
            skLineSegment(sketch, "E208.18.1.1", {"start": v(21.05, 39.44) * mm, "end": v(21.05, 37.44) * mm});
            skLineSegment(sketch, "E208.18.1.2", {"start": v(21.05, 37.44) * mm, "end": v(23.05, 37.44) * mm});
            skLineSegment(sketch, "E208.18.1.3", {"start": v(23.05, 39.44) * mm, "end": v(23.05, 37.44) * mm});
            skLineSegment(sketch, "E208.18.2.0", {"start": v(21.05, 35.44) * mm, "end": v(23.05, 35.44) * mm});
            skLineSegment(sketch, "E208.18.2.1", {"start": v(21.05, 35.44) * mm, "end": v(21.05, 33.44) * mm});
            skLineSegment(sketch, "E208.18.2.2", {"start": v(21.05, 33.44) * mm, "end": v(23.05, 33.44) * mm});
            skLineSegment(sketch, "E208.18.2.3", {"start": v(23.05, 35.44) * mm, "end": v(23.05, 33.44) * mm});
            skLineSegment(sketch, "E208.18.3.0", {"start": v(21.05, 31.44) * mm, "end": v(23.05, 31.44) * mm});
            skLineSegment(sketch, "E208.18.3.1", {"start": v(21.05, 31.44) * mm, "end": v(21.05, 29.44) * mm});
            skLineSegment(sketch, "E208.18.3.2", {"start": v(21.05, 29.44) * mm, "end": v(23.05, 29.44) * mm});
            skLineSegment(sketch, "E208.18.3.3", {"start": v(23.05, 31.44) * mm, "end": v(23.05, 29.44) * mm});
            skLineSegment(sketch, "E208.18.4.0", {"start": v(21.05, 27.44) * mm, "end": v(23.05, 27.44) * mm});
            skLineSegment(sketch, "E208.18.4.1", {"start": v(21.05, 27.44) * mm, "end": v(21.05, 25.44) * mm});
            skLineSegment(sketch, "E208.18.4.2", {"start": v(21.05, 25.44) * mm, "end": v(23.05, 25.44) * mm});
            skLineSegment(sketch, "E208.18.4.3", {"start": v(23.05, 27.44) * mm, "end": v(23.05, 25.44) * mm});
            skLineSegment(sketch, "E208.18.5.0", {"start": v(21.05, 23.44) * mm, "end": v(23.05, 23.44) * mm});
            skLineSegment(sketch, "E208.18.5.1", {"start": v(21.05, 23.44) * mm, "end": v(21.05, 21.44) * mm});
            skLineSegment(sketch, "E208.18.5.2", {"start": v(21.05, 21.44) * mm, "end": v(23.05, 21.44) * mm});
            skLineSegment(sketch, "E208.18.5.3", {"start": v(23.05, 23.44) * mm, "end": v(23.05, 21.44) * mm});
            skLineSegment(sketch, "E208.18.6.0", {"start": v(21.05, 19.44) * mm, "end": v(23.05, 19.44) * mm});
            skLineSegment(sketch, "E208.18.6.1", {"start": v(21.05, 19.44) * mm, "end": v(21.05, 17.44) * mm});
            skLineSegment(sketch, "E208.18.6.2", {"start": v(21.05, 17.44) * mm, "end": v(23.05, 17.44) * mm});
            skLineSegment(sketch, "E208.18.6.3", {"start": v(23.05, 19.44) * mm, "end": v(23.05, 17.44) * mm});
            skLineSegment(sketch, "E208.18.7.0", {"start": v(21.05, 15.44) * mm, "end": v(23.05, 15.44) * mm});
            skLineSegment(sketch, "E208.18.7.1", {"start": v(21.05, 15.44) * mm, "end": v(21.05, 13.44) * mm});
            skLineSegment(sketch, "E208.18.7.2", {"start": v(21.05, 13.44) * mm, "end": v(23.05, 13.44) * mm});
            skLineSegment(sketch, "E208.18.7.3", {"start": v(23.05, 15.44) * mm, "end": v(23.05, 13.44) * mm});
            skLineSegment(sketch, "E208.18.8.0", {"start": v(21.05, 11.44) * mm, "end": v(23.05, 11.44) * mm});
            skLineSegment(sketch, "E208.18.8.1", {"start": v(21.05, 11.44) * mm, "end": v(21.05, 9.44) * mm});
            skLineSegment(sketch, "E208.18.8.2", {"start": v(21.05, 9.44) * mm, "end": v(23.05, 9.44) * mm});
            skLineSegment(sketch, "E208.18.8.3", {"start": v(23.05, 11.44) * mm, "end": v(23.05, 9.44) * mm});
            skLineSegment(sketch, "E208.18.9.0", {"start": v(21.05, 7.44) * mm, "end": v(23.05, 7.44) * mm});
            skLineSegment(sketch, "E208.18.9.1", {"start": v(21.05, 7.44) * mm, "end": v(21.05, 5.44) * mm});
            skLineSegment(sketch, "E208.18.9.2", {"start": v(21.05, 5.44) * mm, "end": v(23.05, 5.44) * mm});
            skLineSegment(sketch, "E208.18.9.3", {"start": v(23.05, 7.44) * mm, "end": v(23.05, 5.44) * mm});
            skLineSegment(sketch, "E208.18.10.0", {"start": v(21.05, 3.44) * mm, "end": v(23.05, 3.44) * mm});
            skLineSegment(sketch, "E208.18.10.1", {"start": v(21.05, 3.44) * mm, "end": v(21.05, 1.44) * mm});
            skLineSegment(sketch, "E208.18.10.2", {"start": v(21.05, 1.44) * mm, "end": v(23.05, 1.44) * mm});
            skLineSegment(sketch, "E208.18.10.3", {"start": v(23.05, 3.44) * mm, "end": v(23.05, 1.44) * mm});
            skLineSegment(sketch, "E208.18.11.0", {"start": v(21.05, -0.56) * mm, "end": v(23.05, -0.56) * mm});
            skLineSegment(sketch, "E208.18.11.1", {"start": v(21.05, -0.56) * mm, "end": v(21.05, -2.56) * mm});
            skLineSegment(sketch, "E208.18.11.2", {"start": v(21.05, -2.56) * mm, "end": v(23.05, -2.56) * mm});
            skLineSegment(sketch, "E208.18.11.3", {"start": v(23.05, -0.56) * mm, "end": v(23.05, -2.56) * mm});
            skLineSegment(sketch, "E208.18.12.0", {"start": v(21.05, -4.56) * mm, "end": v(23.05, -4.56) * mm});
            skLineSegment(sketch, "E208.18.12.1", {"start": v(21.05, -4.56) * mm, "end": v(21.05, -6.56) * mm});
            skLineSegment(sketch, "E208.18.12.2", {"start": v(21.05, -6.56) * mm, "end": v(23.05, -6.56) * mm});
            skLineSegment(sketch, "E208.18.12.3", {"start": v(23.05, -4.56) * mm, "end": v(23.05, -6.56) * mm});
            skLineSegment(sketch, "E208.18.13.0", {"start": v(21.05, -8.56) * mm, "end": v(23.05, -8.56) * mm});
            skLineSegment(sketch, "E208.18.13.1", {"start": v(21.05, -8.56) * mm, "end": v(21.05, -10.56) * mm});
            skLineSegment(sketch, "E208.18.13.2", {"start": v(21.05, -10.56) * mm, "end": v(23.05, -10.56) * mm});
            skLineSegment(sketch, "E208.18.13.3", {"start": v(23.05, -8.56) * mm, "end": v(23.05, -10.56) * mm});
            skLineSegment(sketch, "E208.18.14.0", {"start": v(21.05, -12.56) * mm, "end": v(23.05, -12.56) * mm});
            skLineSegment(sketch, "E208.18.14.1", {"start": v(21.05, -12.56) * mm, "end": v(21.05, -14.56) * mm});
            skLineSegment(sketch, "E208.18.14.2", {"start": v(21.05, -14.56) * mm, "end": v(23.05, -14.56) * mm});
            skLineSegment(sketch, "E208.18.14.3", {"start": v(23.05, -12.56) * mm, "end": v(23.05, -14.56) * mm});
            skLineSegment(sketch, "E208.18.15.0", {"start": v(21.05, -16.56) * mm, "end": v(23.05, -16.56) * mm});
            skLineSegment(sketch, "E208.18.15.1", {"start": v(21.05, -16.56) * mm, "end": v(21.05, -18.56) * mm});
            skLineSegment(sketch, "E208.18.15.2", {"start": v(21.05, -18.56) * mm, "end": v(23.05, -18.56) * mm});
            skLineSegment(sketch, "E208.18.15.3", {"start": v(23.05, -16.56) * mm, "end": v(23.05, -18.56) * mm});
            skLineSegment(sketch, "E208.18.16.0", {"start": v(21.05, -20.56) * mm, "end": v(23.05, -20.56) * mm});
            skLineSegment(sketch, "E208.18.16.1", {"start": v(21.05, -20.56) * mm, "end": v(21.05, -22.56) * mm});
            skLineSegment(sketch, "E208.18.16.2", {"start": v(21.05, -22.56) * mm, "end": v(23.05, -22.56) * mm});
            skLineSegment(sketch, "E208.18.16.3", {"start": v(23.05, -20.56) * mm, "end": v(23.05, -22.56) * mm});
            skLineSegment(sketch, "E208.18.17.0", {"start": v(21.05, -24.56) * mm, "end": v(23.05, -24.56) * mm});
            skLineSegment(sketch, "E208.18.17.1", {"start": v(21.05, -24.56) * mm, "end": v(21.05, -26.56) * mm});
            skLineSegment(sketch, "E208.18.17.2", {"start": v(21.05, -26.56) * mm, "end": v(23.05, -26.56) * mm});
            skLineSegment(sketch, "E208.18.17.3", {"start": v(23.05, -24.56) * mm, "end": v(23.05, -26.56) * mm});
            skLineSegment(sketch, "E208.18.18.0", {"start": v(21.05, -28.56) * mm, "end": v(23.05, -28.56) * mm});
            skLineSegment(sketch, "E208.18.18.1", {"start": v(21.05, -28.56) * mm, "end": v(21.05, -30.56) * mm});
            skLineSegment(sketch, "E208.18.18.2", {"start": v(21.05, -30.56) * mm, "end": v(23.05, -30.56) * mm});
            skLineSegment(sketch, "E208.18.18.3", {"start": v(23.05, -28.56) * mm, "end": v(23.05, -30.56) * mm});
            skLineSegment(sketch, "E208.18.19.0", {"start": v(21.05, -32.56) * mm, "end": v(23.05, -32.56) * mm});
            skLineSegment(sketch, "E208.18.19.1", {"start": v(21.05, -32.56) * mm, "end": v(21.05, -34.56) * mm});
            skLineSegment(sketch, "E208.18.19.2", {"start": v(21.05, -34.56) * mm, "end": v(23.05, -34.56) * mm});
            skLineSegment(sketch, "E208.18.19.3", {"start": v(23.05, -32.56) * mm, "end": v(23.05, -34.56) * mm});
            skLineSegment(sketch, "E208.18.20.0", {"start": v(21.05, -36.56) * mm, "end": v(23.05, -36.56) * mm});
            skLineSegment(sketch, "E208.18.20.1", {"start": v(21.05, -36.56) * mm, "end": v(21.05, -38.56) * mm});
            skLineSegment(sketch, "E208.18.20.2", {"start": v(21.05, -38.56) * mm, "end": v(23.05, -38.56) * mm});
            skLineSegment(sketch, "E208.18.20.3", {"start": v(23.05, -36.56) * mm, "end": v(23.05, -38.56) * mm});
            skLineSegment(sketch, "E208.18.21.0", {"start": v(21.05, -40.56) * mm, "end": v(23.05, -40.56) * mm});
            skLineSegment(sketch, "E208.18.21.1", {"start": v(21.05, -40.56) * mm, "end": v(21.05, -42.56) * mm});
            skLineSegment(sketch, "E208.18.21.2", {"start": v(21.05, -42.56) * mm, "end": v(23.05, -42.56) * mm});
            skLineSegment(sketch, "E208.18.21.3", {"start": v(23.05, -40.56) * mm, "end": v(23.05, -42.56) * mm});
            skLineSegment(sketch, "E208.19.0.0", {"start": v(25.05, 43.44) * mm, "end": v(27.05, 43.44) * mm});
            skLineSegment(sketch, "E208.19.0.1", {"start": v(25.05, 43.44) * mm, "end": v(25.05, 41.44) * mm});
            skLineSegment(sketch, "E208.19.0.2", {"start": v(25.05, 41.44) * mm, "end": v(27.05, 41.44) * mm});
            skLineSegment(sketch, "E208.19.0.3", {"start": v(27.05, 43.44) * mm, "end": v(27.05, 41.44) * mm});
            skLineSegment(sketch, "E208.19.1.0", {"start": v(25.05, 39.44) * mm, "end": v(27.05, 39.44) * mm});
            skLineSegment(sketch, "E208.19.1.1", {"start": v(25.05, 39.44) * mm, "end": v(25.05, 37.44) * mm});
            skLineSegment(sketch, "E208.19.1.2", {"start": v(25.05, 37.44) * mm, "end": v(27.05, 37.44) * mm});
            skLineSegment(sketch, "E208.19.1.3", {"start": v(27.05, 39.44) * mm, "end": v(27.05, 37.44) * mm});
            skLineSegment(sketch, "E208.19.2.0", {"start": v(25.05, 35.44) * mm, "end": v(27.05, 35.44) * mm});
            skLineSegment(sketch, "E208.19.2.1", {"start": v(25.05, 35.44) * mm, "end": v(25.05, 33.44) * mm});
            skLineSegment(sketch, "E208.19.2.2", {"start": v(25.05, 33.44) * mm, "end": v(27.05, 33.44) * mm});
            skLineSegment(sketch, "E208.19.2.3", {"start": v(27.05, 35.44) * mm, "end": v(27.05, 33.44) * mm});
            skLineSegment(sketch, "E208.19.3.0", {"start": v(25.05, 31.44) * mm, "end": v(27.05, 31.44) * mm});
            skLineSegment(sketch, "E208.19.3.1", {"start": v(25.05, 31.44) * mm, "end": v(25.05, 29.44) * mm});
            skLineSegment(sketch, "E208.19.3.2", {"start": v(25.05, 29.44) * mm, "end": v(27.05, 29.44) * mm});
            skLineSegment(sketch, "E208.19.3.3", {"start": v(27.05, 31.44) * mm, "end": v(27.05, 29.44) * mm});
            skLineSegment(sketch, "E208.19.4.0", {"start": v(25.05, 27.44) * mm, "end": v(27.05, 27.44) * mm});
            skLineSegment(sketch, "E208.19.4.1", {"start": v(25.05, 27.44) * mm, "end": v(25.05, 25.44) * mm});
            skLineSegment(sketch, "E208.19.4.2", {"start": v(25.05, 25.44) * mm, "end": v(27.05, 25.44) * mm});
            skLineSegment(sketch, "E208.19.4.3", {"start": v(27.05, 27.44) * mm, "end": v(27.05, 25.44) * mm});
            skLineSegment(sketch, "E208.19.5.0", {"start": v(25.05, 23.44) * mm, "end": v(27.05, 23.44) * mm});
            skLineSegment(sketch, "E208.19.5.1", {"start": v(25.05, 23.44) * mm, "end": v(25.05, 21.44) * mm});
            skLineSegment(sketch, "E208.19.5.2", {"start": v(25.05, 21.44) * mm, "end": v(27.05, 21.44) * mm});
            skLineSegment(sketch, "E208.19.5.3", {"start": v(27.05, 23.44) * mm, "end": v(27.05, 21.44) * mm});
            skLineSegment(sketch, "E208.19.6.0", {"start": v(25.05, 19.44) * mm, "end": v(27.05, 19.44) * mm});
            skLineSegment(sketch, "E208.19.6.1", {"start": v(25.05, 19.44) * mm, "end": v(25.05, 17.44) * mm});
            skLineSegment(sketch, "E208.19.6.2", {"start": v(25.05, 17.44) * mm, "end": v(27.05, 17.44) * mm});
            skLineSegment(sketch, "E208.19.6.3", {"start": v(27.05, 19.44) * mm, "end": v(27.05, 17.44) * mm});
            skLineSegment(sketch, "E208.19.7.0", {"start": v(25.05, 15.44) * mm, "end": v(27.05, 15.44) * mm});
            skLineSegment(sketch, "E208.19.7.1", {"start": v(25.05, 15.44) * mm, "end": v(25.05, 13.44) * mm});
            skLineSegment(sketch, "E208.19.7.2", {"start": v(25.05, 13.44) * mm, "end": v(27.05, 13.44) * mm});
            skLineSegment(sketch, "E208.19.7.3", {"start": v(27.05, 15.44) * mm, "end": v(27.05, 13.44) * mm});
            skLineSegment(sketch, "E208.19.8.0", {"start": v(25.05, 11.44) * mm, "end": v(27.05, 11.44) * mm});
            skLineSegment(sketch, "E208.19.8.1", {"start": v(25.05, 11.44) * mm, "end": v(25.05, 9.44) * mm});
            skLineSegment(sketch, "E208.19.8.2", {"start": v(25.05, 9.44) * mm, "end": v(27.05, 9.44) * mm});
            skLineSegment(sketch, "E208.19.8.3", {"start": v(27.05, 11.44) * mm, "end": v(27.05, 9.44) * mm});
            skLineSegment(sketch, "E208.19.9.0", {"start": v(25.05, 7.44) * mm, "end": v(27.05, 7.44) * mm});
            skLineSegment(sketch, "E208.19.9.1", {"start": v(25.05, 7.44) * mm, "end": v(25.05, 5.44) * mm});
            skLineSegment(sketch, "E208.19.9.2", {"start": v(25.05, 5.44) * mm, "end": v(27.05, 5.44) * mm});
            skLineSegment(sketch, "E208.19.9.3", {"start": v(27.05, 7.44) * mm, "end": v(27.05, 5.44) * mm});
            skLineSegment(sketch, "E208.19.10.0", {"start": v(25.05, 3.44) * mm, "end": v(27.05, 3.44) * mm});
            skLineSegment(sketch, "E208.19.10.1", {"start": v(25.05, 3.44) * mm, "end": v(25.05, 1.44) * mm});
            skLineSegment(sketch, "E208.19.10.2", {"start": v(25.05, 1.44) * mm, "end": v(27.05, 1.44) * mm});
            skLineSegment(sketch, "E208.19.10.3", {"start": v(27.05, 3.44) * mm, "end": v(27.05, 1.44) * mm});
            skLineSegment(sketch, "E208.19.11.0", {"start": v(25.05, -0.56) * mm, "end": v(27.05, -0.56) * mm});
            skLineSegment(sketch, "E208.19.11.1", {"start": v(25.05, -0.56) * mm, "end": v(25.05, -2.56) * mm});
            skLineSegment(sketch, "E208.19.11.2", {"start": v(25.05, -2.56) * mm, "end": v(27.05, -2.56) * mm});
            skLineSegment(sketch, "E208.19.11.3", {"start": v(27.05, -0.56) * mm, "end": v(27.05, -2.56) * mm});
            skLineSegment(sketch, "E208.19.12.0", {"start": v(25.05, -4.56) * mm, "end": v(27.05, -4.56) * mm});
            skLineSegment(sketch, "E208.19.12.1", {"start": v(25.05, -4.56) * mm, "end": v(25.05, -6.56) * mm});
            skLineSegment(sketch, "E208.19.12.2", {"start": v(25.05, -6.56) * mm, "end": v(27.05, -6.56) * mm});
            skLineSegment(sketch, "E208.19.12.3", {"start": v(27.05, -4.56) * mm, "end": v(27.05, -6.56) * mm});
            skLineSegment(sketch, "E208.19.13.0", {"start": v(25.05, -8.56) * mm, "end": v(27.05, -8.56) * mm});
            skLineSegment(sketch, "E208.19.13.1", {"start": v(25.05, -8.56) * mm, "end": v(25.05, -10.56) * mm});
            skLineSegment(sketch, "E208.19.13.2", {"start": v(25.05, -10.56) * mm, "end": v(27.05, -10.56) * mm});
            skLineSegment(sketch, "E208.19.13.3", {"start": v(27.05, -8.56) * mm, "end": v(27.05, -10.56) * mm});
            skLineSegment(sketch, "E208.19.14.0", {"start": v(25.05, -12.56) * mm, "end": v(27.05, -12.56) * mm});
            skLineSegment(sketch, "E208.19.14.1", {"start": v(25.05, -12.56) * mm, "end": v(25.05, -14.56) * mm});
            skLineSegment(sketch, "E208.19.14.2", {"start": v(25.05, -14.56) * mm, "end": v(27.05, -14.56) * mm});
            skLineSegment(sketch, "E208.19.14.3", {"start": v(27.05, -12.56) * mm, "end": v(27.05, -14.56) * mm});
            skLineSegment(sketch, "E208.19.15.0", {"start": v(25.05, -16.56) * mm, "end": v(27.05, -16.56) * mm});
            skLineSegment(sketch, "E208.19.15.1", {"start": v(25.05, -16.56) * mm, "end": v(25.05, -18.56) * mm});
            skLineSegment(sketch, "E208.19.15.2", {"start": v(25.05, -18.56) * mm, "end": v(27.05, -18.56) * mm});
            skLineSegment(sketch, "E208.19.15.3", {"start": v(27.05, -16.56) * mm, "end": v(27.05, -18.56) * mm});
            skLineSegment(sketch, "E208.19.16.0", {"start": v(25.05, -20.56) * mm, "end": v(27.05, -20.56) * mm});
            skLineSegment(sketch, "E208.19.16.1", {"start": v(25.05, -20.56) * mm, "end": v(25.05, -22.56) * mm});
            skLineSegment(sketch, "E208.19.16.2", {"start": v(25.05, -22.56) * mm, "end": v(27.05, -22.56) * mm});
            skLineSegment(sketch, "E208.19.16.3", {"start": v(27.05, -20.56) * mm, "end": v(27.05, -22.56) * mm});
            skLineSegment(sketch, "E208.19.17.0", {"start": v(25.05, -24.56) * mm, "end": v(27.05, -24.56) * mm});
            skLineSegment(sketch, "E208.19.17.1", {"start": v(25.05, -24.56) * mm, "end": v(25.05, -26.56) * mm});
            skLineSegment(sketch, "E208.19.17.2", {"start": v(25.05, -26.56) * mm, "end": v(27.05, -26.56) * mm});
            skLineSegment(sketch, "E208.19.17.3", {"start": v(27.05, -24.56) * mm, "end": v(27.05, -26.56) * mm});
            skLineSegment(sketch, "E208.19.18.0", {"start": v(25.05, -28.56) * mm, "end": v(27.05, -28.56) * mm});
            skLineSegment(sketch, "E208.19.18.1", {"start": v(25.05, -28.56) * mm, "end": v(25.05, -30.56) * mm});
            skLineSegment(sketch, "E208.19.18.2", {"start": v(25.05, -30.56) * mm, "end": v(27.05, -30.56) * mm});
            skLineSegment(sketch, "E208.19.18.3", {"start": v(27.05, -28.56) * mm, "end": v(27.05, -30.56) * mm});
            skLineSegment(sketch, "E208.19.19.0", {"start": v(25.05, -32.56) * mm, "end": v(27.05, -32.56) * mm});
            skLineSegment(sketch, "E208.19.19.1", {"start": v(25.05, -32.56) * mm, "end": v(25.05, -34.56) * mm});
            skLineSegment(sketch, "E208.19.19.2", {"start": v(25.05, -34.56) * mm, "end": v(27.05, -34.56) * mm});
            skLineSegment(sketch, "E208.19.19.3", {"start": v(27.05, -32.56) * mm, "end": v(27.05, -34.56) * mm});
            skLineSegment(sketch, "E208.19.20.0", {"start": v(25.05, -36.56) * mm, "end": v(27.05, -36.56) * mm});
            skLineSegment(sketch, "E208.19.20.1", {"start": v(25.05, -36.56) * mm, "end": v(25.05, -38.56) * mm});
            skLineSegment(sketch, "E208.19.20.2", {"start": v(25.05, -38.56) * mm, "end": v(27.05, -38.56) * mm});
            skLineSegment(sketch, "E208.19.20.3", {"start": v(27.05, -36.56) * mm, "end": v(27.05, -38.56) * mm});
            skLineSegment(sketch, "E208.19.21.0", {"start": v(25.05, -40.56) * mm, "end": v(27.05, -40.56) * mm});
            skLineSegment(sketch, "E208.19.21.1", {"start": v(25.05, -40.56) * mm, "end": v(25.05, -42.56) * mm});
            skLineSegment(sketch, "E208.19.21.2", {"start": v(25.05, -42.56) * mm, "end": v(27.05, -42.56) * mm});
            skLineSegment(sketch, "E208.19.21.3", {"start": v(27.05, -40.56) * mm, "end": v(27.05, -42.56) * mm});
            skLineSegment(sketch, "E208.20.0.0", {"start": v(29.05, 43.44) * mm, "end": v(31.05, 43.44) * mm});
            skLineSegment(sketch, "E208.20.0.1", {"start": v(29.05, 43.44) * mm, "end": v(29.05, 41.44) * mm});
            skLineSegment(sketch, "E208.20.0.2", {"start": v(29.05, 41.44) * mm, "end": v(31.05, 41.44) * mm});
            skLineSegment(sketch, "E208.20.0.3", {"start": v(31.05, 43.44) * mm, "end": v(31.05, 41.44) * mm});
            skLineSegment(sketch, "E208.20.1.0", {"start": v(29.05, 39.44) * mm, "end": v(31.05, 39.44) * mm});
            skLineSegment(sketch, "E208.20.1.1", {"start": v(29.05, 39.44) * mm, "end": v(29.05, 37.44) * mm});
            skLineSegment(sketch, "E208.20.1.2", {"start": v(29.05, 37.44) * mm, "end": v(31.05, 37.44) * mm});
            skLineSegment(sketch, "E208.20.1.3", {"start": v(31.05, 39.44) * mm, "end": v(31.05, 37.44) * mm});
            skLineSegment(sketch, "E208.20.2.0", {"start": v(29.05, 35.44) * mm, "end": v(31.05, 35.44) * mm});
            skLineSegment(sketch, "E208.20.2.1", {"start": v(29.05, 35.44) * mm, "end": v(29.05, 33.44) * mm});
            skLineSegment(sketch, "E208.20.2.2", {"start": v(29.05, 33.44) * mm, "end": v(31.05, 33.44) * mm});
            skLineSegment(sketch, "E208.20.2.3", {"start": v(31.05, 35.44) * mm, "end": v(31.05, 33.44) * mm});
            skLineSegment(sketch, "E208.20.3.0", {"start": v(29.05, 31.44) * mm, "end": v(31.05, 31.44) * mm});
            skLineSegment(sketch, "E208.20.3.1", {"start": v(29.05, 31.44) * mm, "end": v(29.05, 29.44) * mm});
            skLineSegment(sketch, "E208.20.3.2", {"start": v(29.05, 29.44) * mm, "end": v(31.05, 29.44) * mm});
            skLineSegment(sketch, "E208.20.3.3", {"start": v(31.05, 31.44) * mm, "end": v(31.05, 29.44) * mm});
            skLineSegment(sketch, "E208.20.4.0", {"start": v(29.05, 27.44) * mm, "end": v(31.05, 27.44) * mm});
            skLineSegment(sketch, "E208.20.4.1", {"start": v(29.05, 27.44) * mm, "end": v(29.05, 25.44) * mm});
            skLineSegment(sketch, "E208.20.4.2", {"start": v(29.05, 25.44) * mm, "end": v(31.05, 25.44) * mm});
            skLineSegment(sketch, "E208.20.4.3", {"start": v(31.05, 27.44) * mm, "end": v(31.05, 25.44) * mm});
            skLineSegment(sketch, "E208.20.5.0", {"start": v(29.05, 23.44) * mm, "end": v(31.05, 23.44) * mm});
            skLineSegment(sketch, "E208.20.5.1", {"start": v(29.05, 23.44) * mm, "end": v(29.05, 21.44) * mm});
            skLineSegment(sketch, "E208.20.5.2", {"start": v(29.05, 21.44) * mm, "end": v(31.05, 21.44) * mm});
            skLineSegment(sketch, "E208.20.5.3", {"start": v(31.05, 23.44) * mm, "end": v(31.05, 21.44) * mm});
            skLineSegment(sketch, "E208.20.6.0", {"start": v(29.05, 19.44) * mm, "end": v(31.05, 19.44) * mm});
            skLineSegment(sketch, "E208.20.6.1", {"start": v(29.05, 19.44) * mm, "end": v(29.05, 17.44) * mm});
            skLineSegment(sketch, "E208.20.6.2", {"start": v(29.05, 17.44) * mm, "end": v(31.05, 17.44) * mm});
            skLineSegment(sketch, "E208.20.6.3", {"start": v(31.05, 19.44) * mm, "end": v(31.05, 17.44) * mm});
            skLineSegment(sketch, "E208.20.7.0", {"start": v(29.05, 15.44) * mm, "end": v(31.05, 15.44) * mm});
            skLineSegment(sketch, "E208.20.7.1", {"start": v(29.05, 15.44) * mm, "end": v(29.05, 13.44) * mm});
            skLineSegment(sketch, "E208.20.7.2", {"start": v(29.05, 13.44) * mm, "end": v(31.05, 13.44) * mm});
            skLineSegment(sketch, "E208.20.7.3", {"start": v(31.05, 15.44) * mm, "end": v(31.05, 13.44) * mm});
            skLineSegment(sketch, "E208.20.8.0", {"start": v(29.05, 11.44) * mm, "end": v(31.05, 11.44) * mm});
            skLineSegment(sketch, "E208.20.8.1", {"start": v(29.05, 11.44) * mm, "end": v(29.05, 9.44) * mm});
            skLineSegment(sketch, "E208.20.8.2", {"start": v(29.05, 9.44) * mm, "end": v(31.05, 9.44) * mm});
            skLineSegment(sketch, "E208.20.8.3", {"start": v(31.05, 11.44) * mm, "end": v(31.05, 9.44) * mm});
            skLineSegment(sketch, "E208.20.9.0", {"start": v(29.05, 7.44) * mm, "end": v(31.05, 7.44) * mm});
            skLineSegment(sketch, "E208.20.9.1", {"start": v(29.05, 7.44) * mm, "end": v(29.05, 5.44) * mm});
            skLineSegment(sketch, "E208.20.9.2", {"start": v(29.05, 5.44) * mm, "end": v(31.05, 5.44) * mm});
            skLineSegment(sketch, "E208.20.9.3", {"start": v(31.05, 7.44) * mm, "end": v(31.05, 5.44) * mm});
            skLineSegment(sketch, "E208.20.10.0", {"start": v(29.05, 3.44) * mm, "end": v(31.05, 3.44) * mm});
            skLineSegment(sketch, "E208.20.10.1", {"start": v(29.05, 3.44) * mm, "end": v(29.05, 1.44) * mm});
            skLineSegment(sketch, "E208.20.10.2", {"start": v(29.05, 1.44) * mm, "end": v(31.05, 1.44) * mm});
            skLineSegment(sketch, "E208.20.10.3", {"start": v(31.05, 3.44) * mm, "end": v(31.05, 1.44) * mm});
            skLineSegment(sketch, "E208.20.11.0", {"start": v(29.05, -0.56) * mm, "end": v(31.05, -0.56) * mm});
            skLineSegment(sketch, "E208.20.11.1", {"start": v(29.05, -0.56) * mm, "end": v(29.05, -2.56) * mm});
            skLineSegment(sketch, "E208.20.11.2", {"start": v(29.05, -2.56) * mm, "end": v(31.05, -2.56) * mm});
            skLineSegment(sketch, "E208.20.11.3", {"start": v(31.05, -0.56) * mm, "end": v(31.05, -2.56) * mm});
            skLineSegment(sketch, "E208.20.12.0", {"start": v(29.05, -4.56) * mm, "end": v(31.05, -4.56) * mm});
            skLineSegment(sketch, "E208.20.12.1", {"start": v(29.05, -4.56) * mm, "end": v(29.05, -6.56) * mm});
            skLineSegment(sketch, "E208.20.12.2", {"start": v(29.05, -6.56) * mm, "end": v(31.05, -6.56) * mm});
            skLineSegment(sketch, "E208.20.12.3", {"start": v(31.05, -4.56) * mm, "end": v(31.05, -6.56) * mm});
            skLineSegment(sketch, "E208.20.13.0", {"start": v(29.05, -8.56) * mm, "end": v(31.05, -8.56) * mm});
            skLineSegment(sketch, "E208.20.13.1", {"start": v(29.05, -8.56) * mm, "end": v(29.05, -10.56) * mm});
            skLineSegment(sketch, "E208.20.13.2", {"start": v(29.05, -10.56) * mm, "end": v(31.05, -10.56) * mm});
            skLineSegment(sketch, "E208.20.13.3", {"start": v(31.05, -8.56) * mm, "end": v(31.05, -10.56) * mm});
            skLineSegment(sketch, "E208.20.14.0", {"start": v(29.05, -12.56) * mm, "end": v(31.05, -12.56) * mm});
            skLineSegment(sketch, "E208.20.14.1", {"start": v(29.05, -12.56) * mm, "end": v(29.05, -14.56) * mm});
            skLineSegment(sketch, "E208.20.14.2", {"start": v(29.05, -14.56) * mm, "end": v(31.05, -14.56) * mm});
            skLineSegment(sketch, "E208.20.14.3", {"start": v(31.05, -12.56) * mm, "end": v(31.05, -14.56) * mm});
            skLineSegment(sketch, "E208.20.15.0", {"start": v(29.05, -16.56) * mm, "end": v(31.05, -16.56) * mm});
            skLineSegment(sketch, "E208.20.15.1", {"start": v(29.05, -16.56) * mm, "end": v(29.05, -18.56) * mm});
            skLineSegment(sketch, "E208.20.15.2", {"start": v(29.05, -18.56) * mm, "end": v(31.05, -18.56) * mm});
            skLineSegment(sketch, "E208.20.15.3", {"start": v(31.05, -16.56) * mm, "end": v(31.05, -18.56) * mm});
            skLineSegment(sketch, "E208.20.16.0", {"start": v(29.05, -20.56) * mm, "end": v(31.05, -20.56) * mm});
            skLineSegment(sketch, "E208.20.16.1", {"start": v(29.05, -20.56) * mm, "end": v(29.05, -22.56) * mm});
            skLineSegment(sketch, "E208.20.16.2", {"start": v(29.05, -22.56) * mm, "end": v(31.05, -22.56) * mm});
            skLineSegment(sketch, "E208.20.16.3", {"start": v(31.05, -20.56) * mm, "end": v(31.05, -22.56) * mm});
            skLineSegment(sketch, "E208.20.17.0", {"start": v(29.05, -24.56) * mm, "end": v(31.05, -24.56) * mm});
            skLineSegment(sketch, "E208.20.17.1", {"start": v(29.05, -24.56) * mm, "end": v(29.05, -26.56) * mm});
            skLineSegment(sketch, "E208.20.17.2", {"start": v(29.05, -26.56) * mm, "end": v(31.05, -26.56) * mm});
            skLineSegment(sketch, "E208.20.17.3", {"start": v(31.05, -24.56) * mm, "end": v(31.05, -26.56) * mm});
            skLineSegment(sketch, "E208.20.18.0", {"start": v(29.05, -28.56) * mm, "end": v(31.05, -28.56) * mm});
            skLineSegment(sketch, "E208.20.18.1", {"start": v(29.05, -28.56) * mm, "end": v(29.05, -30.56) * mm});
            skLineSegment(sketch, "E208.20.18.2", {"start": v(29.05, -30.56) * mm, "end": v(31.05, -30.56) * mm});
            skLineSegment(sketch, "E208.20.18.3", {"start": v(31.05, -28.56) * mm, "end": v(31.05, -30.56) * mm});
            skLineSegment(sketch, "E208.20.19.0", {"start": v(29.05, -32.56) * mm, "end": v(31.05, -32.56) * mm});
            skLineSegment(sketch, "E208.20.19.1", {"start": v(29.05, -32.56) * mm, "end": v(29.05, -34.56) * mm});
            skLineSegment(sketch, "E208.20.19.2", {"start": v(29.05, -34.56) * mm, "end": v(31.05, -34.56) * mm});
            skLineSegment(sketch, "E208.20.19.3", {"start": v(31.05, -32.56) * mm, "end": v(31.05, -34.56) * mm});
            skLineSegment(sketch, "E208.20.20.0", {"start": v(29.05, -36.56) * mm, "end": v(31.05, -36.56) * mm});
            skLineSegment(sketch, "E208.20.20.1", {"start": v(29.05, -36.56) * mm, "end": v(29.05, -38.56) * mm});
            skLineSegment(sketch, "E208.20.20.2", {"start": v(29.05, -38.56) * mm, "end": v(31.05, -38.56) * mm});
            skLineSegment(sketch, "E208.20.20.3", {"start": v(31.05, -36.56) * mm, "end": v(31.05, -38.56) * mm});
            skLineSegment(sketch, "E208.20.21.0", {"start": v(29.05, -40.56) * mm, "end": v(31.05, -40.56) * mm});
            skLineSegment(sketch, "E208.20.21.1", {"start": v(29.05, -40.56) * mm, "end": v(29.05, -42.56) * mm});
            skLineSegment(sketch, "E208.20.21.2", {"start": v(29.05, -42.56) * mm, "end": v(31.05, -42.56) * mm});
            skLineSegment(sketch, "E208.20.21.3", {"start": v(31.05, -40.56) * mm, "end": v(31.05, -42.56) * mm});
            skLineSegment(sketch, "E208.21.0.0", {"start": v(33.05, 43.44) * mm, "end": v(35.05, 43.44) * mm});
            skLineSegment(sketch, "E208.21.0.1", {"start": v(33.05, 43.44) * mm, "end": v(33.05, 41.44) * mm});
            skLineSegment(sketch, "E208.21.0.2", {"start": v(33.05, 41.44) * mm, "end": v(35.05, 41.44) * mm});
            skLineSegment(sketch, "E208.21.0.3", {"start": v(35.05, 43.44) * mm, "end": v(35.05, 41.44) * mm});
            skLineSegment(sketch, "E208.21.1.0", {"start": v(33.05, 39.44) * mm, "end": v(35.05, 39.44) * mm});
            skLineSegment(sketch, "E208.21.1.1", {"start": v(33.05, 39.44) * mm, "end": v(33.05, 37.44) * mm});
            skLineSegment(sketch, "E208.21.1.2", {"start": v(33.05, 37.44) * mm, "end": v(35.05, 37.44) * mm});
            skLineSegment(sketch, "E208.21.1.3", {"start": v(35.05, 39.44) * mm, "end": v(35.05, 37.44) * mm});
            skLineSegment(sketch, "E208.21.2.0", {"start": v(33.05, 35.44) * mm, "end": v(35.05, 35.44) * mm});
            skLineSegment(sketch, "E208.21.2.1", {"start": v(33.05, 35.44) * mm, "end": v(33.05, 33.44) * mm});
            skLineSegment(sketch, "E208.21.2.2", {"start": v(33.05, 33.44) * mm, "end": v(35.05, 33.44) * mm});
            skLineSegment(sketch, "E208.21.2.3", {"start": v(35.05, 35.44) * mm, "end": v(35.05, 33.44) * mm});
            skLineSegment(sketch, "E208.21.3.0", {"start": v(33.05, 31.44) * mm, "end": v(35.05, 31.44) * mm});
            skLineSegment(sketch, "E208.21.3.1", {"start": v(33.05, 31.44) * mm, "end": v(33.05, 29.44) * mm});
            skLineSegment(sketch, "E208.21.3.2", {"start": v(33.05, 29.44) * mm, "end": v(35.05, 29.44) * mm});
            skLineSegment(sketch, "E208.21.3.3", {"start": v(35.05, 31.44) * mm, "end": v(35.05, 29.44) * mm});
            skLineSegment(sketch, "E208.21.4.0", {"start": v(33.05, 27.44) * mm, "end": v(35.05, 27.44) * mm});
            skLineSegment(sketch, "E208.21.4.1", {"start": v(33.05, 27.44) * mm, "end": v(33.05, 25.44) * mm});
            skLineSegment(sketch, "E208.21.4.2", {"start": v(33.05, 25.44) * mm, "end": v(35.05, 25.44) * mm});
            skLineSegment(sketch, "E208.21.4.3", {"start": v(35.05, 27.44) * mm, "end": v(35.05, 25.44) * mm});
            skLineSegment(sketch, "E208.21.5.0", {"start": v(33.05, 23.44) * mm, "end": v(35.05, 23.44) * mm});
            skLineSegment(sketch, "E208.21.5.1", {"start": v(33.05, 23.44) * mm, "end": v(33.05, 21.44) * mm});
            skLineSegment(sketch, "E208.21.5.2", {"start": v(33.05, 21.44) * mm, "end": v(35.05, 21.44) * mm});
            skLineSegment(sketch, "E208.21.5.3", {"start": v(35.05, 23.44) * mm, "end": v(35.05, 21.44) * mm});
            skLineSegment(sketch, "E208.21.6.0", {"start": v(33.05, 19.44) * mm, "end": v(35.05, 19.44) * mm});
            skLineSegment(sketch, "E208.21.6.1", {"start": v(33.05, 19.44) * mm, "end": v(33.05, 17.44) * mm});
            skLineSegment(sketch, "E208.21.6.2", {"start": v(33.05, 17.44) * mm, "end": v(35.05, 17.44) * mm});
            skLineSegment(sketch, "E208.21.6.3", {"start": v(35.05, 19.44) * mm, "end": v(35.05, 17.44) * mm});
            skLineSegment(sketch, "E208.21.7.0", {"start": v(33.05, 15.44) * mm, "end": v(35.05, 15.44) * mm});
            skLineSegment(sketch, "E208.21.7.1", {"start": v(33.05, 15.44) * mm, "end": v(33.05, 13.44) * mm});
            skLineSegment(sketch, "E208.21.7.2", {"start": v(33.05, 13.44) * mm, "end": v(35.05, 13.44) * mm});
            skLineSegment(sketch, "E208.21.7.3", {"start": v(35.05, 15.44) * mm, "end": v(35.05, 13.44) * mm});
            skLineSegment(sketch, "E208.21.8.0", {"start": v(33.05, 11.44) * mm, "end": v(35.05, 11.44) * mm});
            skLineSegment(sketch, "E208.21.8.1", {"start": v(33.05, 11.44) * mm, "end": v(33.05, 9.44) * mm});
            skLineSegment(sketch, "E208.21.8.2", {"start": v(33.05, 9.44) * mm, "end": v(35.05, 9.44) * mm});
            skLineSegment(sketch, "E208.21.8.3", {"start": v(35.05, 11.44) * mm, "end": v(35.05, 9.44) * mm});
            skLineSegment(sketch, "E208.21.9.0", {"start": v(33.05, 7.44) * mm, "end": v(35.05, 7.44) * mm});
            skLineSegment(sketch, "E208.21.9.1", {"start": v(33.05, 7.44) * mm, "end": v(33.05, 5.44) * mm});
            skLineSegment(sketch, "E208.21.9.2", {"start": v(33.05, 5.44) * mm, "end": v(35.05, 5.44) * mm});
            skLineSegment(sketch, "E208.21.9.3", {"start": v(35.05, 7.44) * mm, "end": v(35.05, 5.44) * mm});
            skLineSegment(sketch, "E208.21.10.0", {"start": v(33.05, 3.44) * mm, "end": v(35.05, 3.44) * mm});
            skLineSegment(sketch, "E208.21.10.1", {"start": v(33.05, 3.44) * mm, "end": v(33.05, 1.44) * mm});
            skLineSegment(sketch, "E208.21.10.2", {"start": v(33.05, 1.44) * mm, "end": v(35.05, 1.44) * mm});
            skLineSegment(sketch, "E208.21.10.3", {"start": v(35.05, 3.44) * mm, "end": v(35.05, 1.44) * mm});
            skLineSegment(sketch, "E208.21.11.0", {"start": v(33.05, -0.56) * mm, "end": v(35.05, -0.56) * mm});
            skLineSegment(sketch, "E208.21.11.1", {"start": v(33.05, -0.56) * mm, "end": v(33.05, -2.56) * mm});
            skLineSegment(sketch, "E208.21.11.2", {"start": v(33.05, -2.56) * mm, "end": v(35.05, -2.56) * mm});
            skLineSegment(sketch, "E208.21.11.3", {"start": v(35.05, -0.56) * mm, "end": v(35.05, -2.56) * mm});
            skLineSegment(sketch, "E208.21.12.0", {"start": v(33.05, -4.56) * mm, "end": v(35.05, -4.56) * mm});
            skLineSegment(sketch, "E208.21.12.1", {"start": v(33.05, -4.56) * mm, "end": v(33.05, -6.56) * mm});
            skLineSegment(sketch, "E208.21.12.2", {"start": v(33.05, -6.56) * mm, "end": v(35.05, -6.56) * mm});
            skLineSegment(sketch, "E208.21.12.3", {"start": v(35.05, -4.56) * mm, "end": v(35.05, -6.56) * mm});
            skLineSegment(sketch, "E208.21.13.0", {"start": v(33.05, -8.56) * mm, "end": v(35.05, -8.56) * mm});
            skLineSegment(sketch, "E208.21.13.1", {"start": v(33.05, -8.56) * mm, "end": v(33.05, -10.56) * mm});
            skLineSegment(sketch, "E208.21.13.2", {"start": v(33.05, -10.56) * mm, "end": v(35.05, -10.56) * mm});
            skLineSegment(sketch, "E208.21.13.3", {"start": v(35.05, -8.56) * mm, "end": v(35.05, -10.56) * mm});
            skLineSegment(sketch, "E208.21.14.0", {"start": v(33.05, -12.56) * mm, "end": v(35.05, -12.56) * mm});
            skLineSegment(sketch, "E208.21.14.1", {"start": v(33.05, -12.56) * mm, "end": v(33.05, -14.56) * mm});
            skLineSegment(sketch, "E208.21.14.2", {"start": v(33.05, -14.56) * mm, "end": v(35.05, -14.56) * mm});
            skLineSegment(sketch, "E208.21.14.3", {"start": v(35.05, -12.56) * mm, "end": v(35.05, -14.56) * mm});
            skLineSegment(sketch, "E208.21.15.0", {"start": v(33.05, -16.56) * mm, "end": v(35.05, -16.56) * mm});
            skLineSegment(sketch, "E208.21.15.1", {"start": v(33.05, -16.56) * mm, "end": v(33.05, -18.56) * mm});
            skLineSegment(sketch, "E208.21.15.2", {"start": v(33.05, -18.56) * mm, "end": v(35.05, -18.56) * mm});
            skLineSegment(sketch, "E208.21.15.3", {"start": v(35.05, -16.56) * mm, "end": v(35.05, -18.56) * mm});
            skLineSegment(sketch, "E208.21.16.0", {"start": v(33.05, -20.56) * mm, "end": v(35.05, -20.56) * mm});
            skLineSegment(sketch, "E208.21.16.1", {"start": v(33.05, -20.56) * mm, "end": v(33.05, -22.56) * mm});
            skLineSegment(sketch, "E208.21.16.2", {"start": v(33.05, -22.56) * mm, "end": v(35.05, -22.56) * mm});
            skLineSegment(sketch, "E208.21.16.3", {"start": v(35.05, -20.56) * mm, "end": v(35.05, -22.56) * mm});
            skLineSegment(sketch, "E208.21.17.0", {"start": v(33.05, -24.56) * mm, "end": v(35.05, -24.56) * mm});
            skLineSegment(sketch, "E208.21.17.1", {"start": v(33.05, -24.56) * mm, "end": v(33.05, -26.56) * mm});
            skLineSegment(sketch, "E208.21.17.2", {"start": v(33.05, -26.56) * mm, "end": v(35.05, -26.56) * mm});
            skLineSegment(sketch, "E208.21.17.3", {"start": v(35.05, -24.56) * mm, "end": v(35.05, -26.56) * mm});
            skLineSegment(sketch, "E208.21.18.0", {"start": v(33.05, -28.56) * mm, "end": v(35.05, -28.56) * mm});
            skLineSegment(sketch, "E208.21.18.1", {"start": v(33.05, -28.56) * mm, "end": v(33.05, -30.56) * mm});
            skLineSegment(sketch, "E208.21.18.2", {"start": v(33.05, -30.56) * mm, "end": v(35.05, -30.56) * mm});
            skLineSegment(sketch, "E208.21.18.3", {"start": v(35.05, -28.56) * mm, "end": v(35.05, -30.56) * mm});
            skLineSegment(sketch, "E208.21.19.0", {"start": v(33.05, -32.56) * mm, "end": v(35.05, -32.56) * mm});
            skLineSegment(sketch, "E208.21.19.1", {"start": v(33.05, -32.56) * mm, "end": v(33.05, -34.56) * mm});
            skLineSegment(sketch, "E208.21.19.2", {"start": v(33.05, -34.56) * mm, "end": v(35.05, -34.56) * mm});
            skLineSegment(sketch, "E208.21.19.3", {"start": v(35.05, -32.56) * mm, "end": v(35.05, -34.56) * mm});
            skLineSegment(sketch, "E208.21.20.0", {"start": v(33.05, -36.56) * mm, "end": v(35.05, -36.56) * mm});
            skLineSegment(sketch, "E208.21.20.1", {"start": v(33.05, -36.56) * mm, "end": v(33.05, -38.56) * mm});
            skLineSegment(sketch, "E208.21.20.2", {"start": v(33.05, -38.56) * mm, "end": v(35.05, -38.56) * mm});
            skLineSegment(sketch, "E208.21.20.3", {"start": v(35.05, -36.56) * mm, "end": v(35.05, -38.56) * mm});
            skLineSegment(sketch, "E208.21.21.0", {"start": v(33.05, -40.56) * mm, "end": v(35.05, -40.56) * mm});
            skLineSegment(sketch, "E208.21.21.1", {"start": v(33.05, -40.56) * mm, "end": v(33.05, -42.56) * mm});
            skLineSegment(sketch, "E208.21.21.2", {"start": v(33.05, -42.56) * mm, "end": v(35.05, -42.56) * mm});
            skLineSegment(sketch, "E208.21.21.3", {"start": v(35.05, -40.56) * mm, "end": v(35.05, -42.56) * mm});
            skLineSegment(sketch, "E208.direction1", {"start": v(-50.95, 43.44) * mm, "end": v(-46.95, 43.44) * mm, "construction": true});
            skLineSegment(sketch, "E208.direction2", {"start": v(-50.95, 43.44) * mm, "end": v(-50.95, 39.44) * mm, "construction": true});
            skSolve(sketch);
        }
        {
            var Q0;
            {var subQ278=sQuery(id+"F23.wireOp",EDGE,"E171.0");Q0=makeQuery(id+"F23.imprint","IMPRINT",FACE,{"disambiguationData":[TD([[makeQuery(id+"F23.imprint","IMPRINT",EDGE,{"derivedFrom":subQ278}),-1.0]])]});}
            extrude(context, id + "F24", {"entities" : qUnion([Q0]), "operationType" : NewBodyOperationType.REMOVE, "oppositeDirection" : true, "depth" : 0.5 * mm});
        }
        {
            var Q0;
            Q0=makeQuery(id+"F6.opRevolve","SWEPT_FACE",FACE,{"disambiguationData":[OSD([sQuery(id+"F0.wireOp",EDGE,"E37")])]});
            var sketch = newSketch(context, id + "F25", { "sketchPlane" : qUnion([Q0])});
            skPoint(sketch, "E209", {"position": v(-7.53, 0) * mm});
            skCircle(sketch, "E210", {"center": v(-7.53, 0) * mm, "radius": 23 * mm});
            skLineSegment(sketch, "E211", {"start": v(-7.53, 0) * mm, "end": v(-35.11, 0) * mm, "construction": true});
            skLineSegment(sketch, "E212", {"start": v(-7.53, 0) * mm, "end": v(-7.53, 27.58) * mm, "construction": true});
            skCircle(sketch, "E213", {"center": v(-7.53, 27.58) * mm, "radius": 1.15 * mm});
            skCircle(sketch, "E214", {"center": v(-35.11, 0) * mm, "radius": 1.15 * mm});
            skCircle(sketch, "E215.MirrorC", {"center": v(-7.53, -27.58) * mm, "radius": 1.15 * mm});
            skCircle(sketch, "E216.MirrorC", {"center": v(20.04, 0) * mm, "radius": 1.15 * mm});
            skSolve(sketch);
        }
        {
            var Q0;
            Q0 = qSketchRegion(id + "F25", true);
            extrude(context, id + "F26", {"entities" : qUnion([Q0]), "operationType" : NewBodyOperationType.REMOVE, "endBound" : BoundingType.UP_TO_NEXT, "oppositeDirection" : true, "depth" : 25 * mm});
        }
    });
